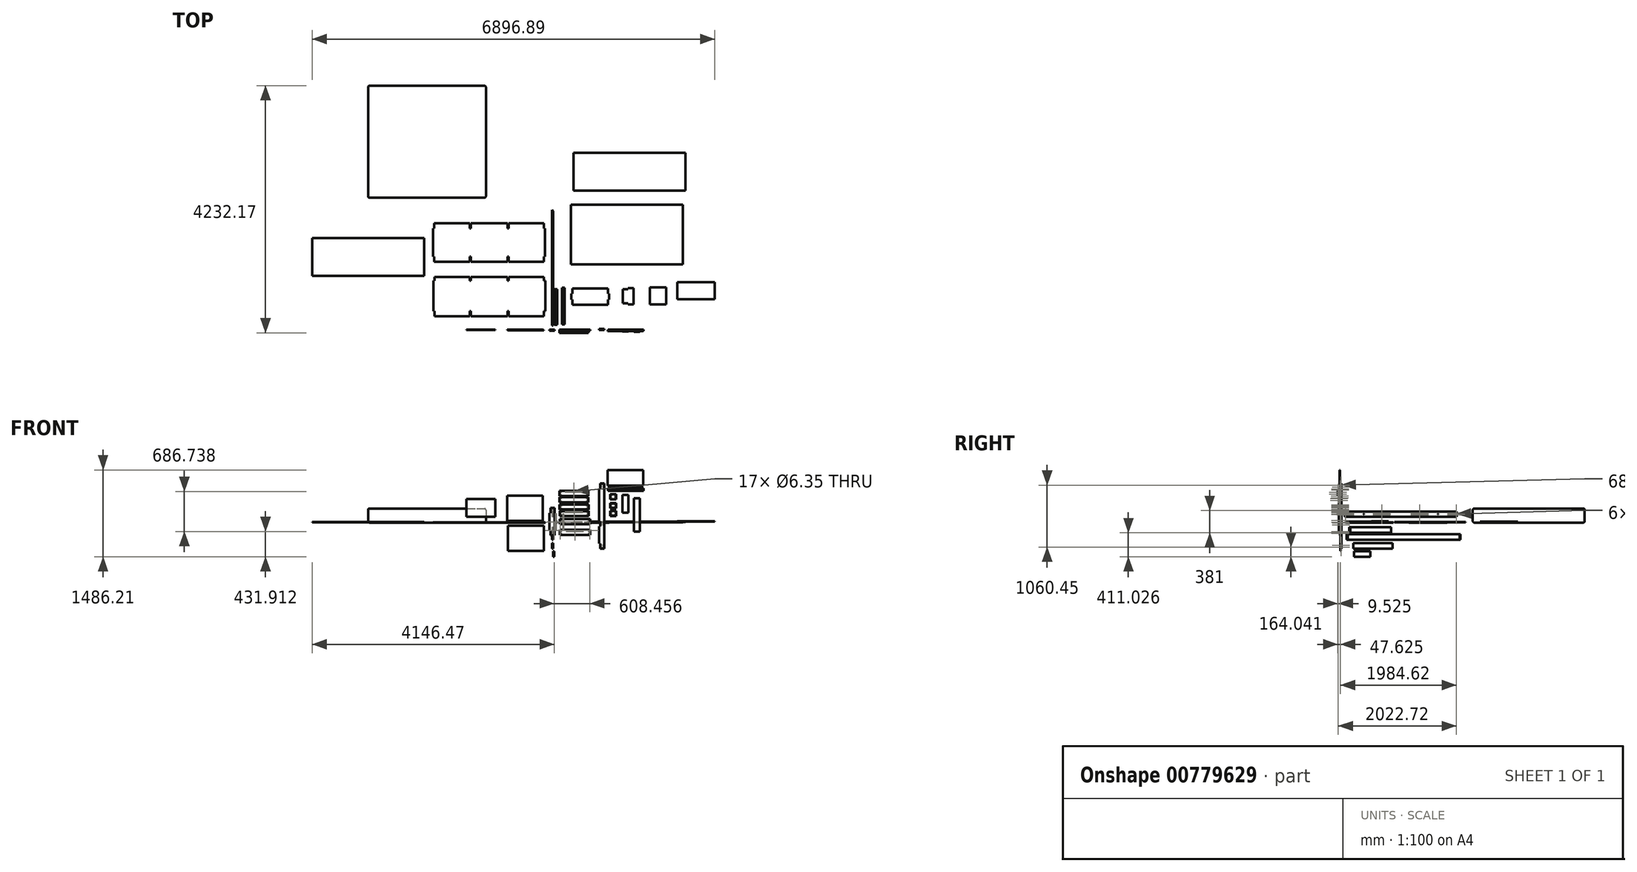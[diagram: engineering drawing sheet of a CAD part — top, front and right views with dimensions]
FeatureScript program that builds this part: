
annotation { "Feature Type Name" : "Feature", "Feature Type Description" : "" }
export const myFeature = defineFeature(function(context is Context, id is Id, definition is map)
    precondition{}
    {
        {
            var Q0;
            Q0=qCreatedBy(makeId("Front.planeOp"),FACE);
            var sketch = newSketch(context, id + "F0", { "sketchPlane" : qUnion([Q0])});
            skLineSegment(sketch, "E0", {"start": v(44.1, 252.24) * mm, "end": v(44.1, -217.66) * mm});
            skLineSegment(sketch, "E1", {"start": v(44.1, -217.66) * mm, "end": v(-25.75, -217.66) * mm});
            skLineSegment(sketch, "E2", {"start": v(-25.75, -217.66) * mm, "end": v(-25.75, -128.76) * mm});
            skLineSegment(sketch, "E3", {"start": v(-25.75, -128.76) * mm, "end": v(-44.8, -128.76) * mm});
            skLineSegment(sketch, "E4", {"start": v(-44.8, -128.76) * mm, "end": v(-44.8, 163.34) * mm});
            skLineSegment(sketch, "E5", {"start": v(-44.8, 163.34) * mm, "end": v(-25.75, 163.34) * mm});
            skLineSegment(sketch, "E6", {"start": v(-25.75, 163.34) * mm, "end": v(-25.75, 252.24) * mm});
            skLineSegment(sketch, "E7", {"start": v(-25.75, 252.24) * mm, "end": v(44.1, 252.24) * mm});
            skPoint(sketch, "E8", {"position": v(36.16, -138.29) * mm});
            skSolve(sketch);
        }
        {
            var Q0;
            Q0=makeQuery(id+"F0.imprint","IMPRINT",FACE,{"disambiguationData":[TD([[makeQuery(id+"F0.imprint","IMPRINT",EDGE,{"derivedFrom":sQuery(id+"F0.wireOp",EDGE,"E0")}),-1.0]])]});
            extrude(context, id + "F1", {"entities" : qUnion([Q0]), "depth" : 19.05 * mm, "offsetDistance" : 25.4 * mm});
        }
        {
            var Q0;
            Q0=sQuery(id+"F0.wireOp",VERTEX,"E8");
            var Q1;
            Q1=makeQuery(id+"F1.opExtrude","SWEPT_BODY",BODY,{"disambiguationData":[OSD([sQuery(id+"F0.wireOp",EDGE,"E0"),sQuery(id+"F0.wireOp",EDGE,"E1"),sQuery(id+"F0.wireOp",EDGE,"E2"),sQuery(id+"F0.wireOp",EDGE,"E3"),sQuery(id+"F0.wireOp",EDGE,"E4"),sQuery(id+"F0.wireOp",EDGE,"E5"),sQuery(id+"F0.wireOp",EDGE,"E6"),sQuery(id+"F0.wireOp",EDGE,"E7")])]});
            hole(context, id + "F2", {"style" : HoleStyle.SIMPLE, "endStyle" : HoleEndStyle.THROUGH, "oppositeDirection" : true, "holeDiameter" : 6.35 * mm, "majorDiameter" : 6.35 * mm, "isTappedThrough" : true, "tappedDepth" : 12.7 * mm, "tapClearance" : 3, "locations" : qUnion([Q0]), "scope" : qUnion([Q1])});
        }
        {
            var Q0;
            Q0=makeQuery(id+"F1.opExtrude","SWEPT_FACE",FACE,{"disambiguationData":[OSD([sQuery(id+"F0.wireOp",EDGE,"E0")])]});
            var sketch = newSketch(context, id + "F3", { "sketchPlane" : qUnion([Q0])});
            skLineSegment(sketch, "E9.0.0", {"start": v(0, -217.66) * mm, "end": v(0, 252.24) * mm});
            skLineSegment(sketch, "E9.0.1", {"start": v(0, 252.24) * mm, "end": v(-19.05, 252.24) * mm});
            skLineSegment(sketch, "E9.0.2", {"start": v(-19.05, 252.24) * mm, "end": v(-19.05, -217.66) * mm});
            skLineSegment(sketch, "E9.0.3", {"start": v(-19.05, -217.66) * mm, "end": v(0, -217.66) * mm});
            skPoint(sketch, "E10", {"position": v(-9.53, -189.09) * mm});
            skPoint(sketch, "E10.positionSnap0", {"position": v(-9.53, -217.66) * mm});
            skPoint(sketch, "E11", {"position": v(-9.53, -157.34) * mm});
            skPoint(sketch, "E12", {"position": v(-9.53, 223.66) * mm});
            skPoint(sketch, "E12.positionSnap0", {"position": v(-9.53, 252.24) * mm});
            skPoint(sketch, "E13", {"position": v(-9.53, 191.91) * mm});
            skSolve(sketch);
        }
        {
            var Q0;
            Q0=sQuery(id+"F3.wireOp",VERTEX,"E10");
            var Q1;
            Q1=makeQuery(id+"F1.opExtrude","SWEPT_BODY",BODY,{"disambiguationData":[OSD([sQuery(id+"F0.wireOp",EDGE,"E0"),sQuery(id+"F0.wireOp",EDGE,"E1"),sQuery(id+"F0.wireOp",EDGE,"E2"),sQuery(id+"F0.wireOp",EDGE,"E3"),sQuery(id+"F0.wireOp",EDGE,"E4"),sQuery(id+"F0.wireOp",EDGE,"E5"),sQuery(id+"F0.wireOp",EDGE,"E6"),sQuery(id+"F0.wireOp",EDGE,"E7")])]});
            hole(context, id + "F4", {"style" : HoleStyle.SIMPLE, "endStyle" : HoleEndStyle.BLIND, "holeDiameter" : 6.35 * mm, "majorDiameter" : 6.35 * mm, "holeDepth" : 25.4 * mm, "isTappedThrough" : true, "tappedDepth" : 12.7 * mm, "tapClearance" : 3, "locations" : qUnion([Q0]), "scope" : qUnion([Q1])});
        }
        {
            var Q0;
            Q0=sQuery(id+"F3.wireOp",VERTEX,"E11");
            var Q1;
            Q1=makeQuery(id+"F1.opExtrude","SWEPT_BODY",BODY,{"disambiguationData":[OSD([sQuery(id+"F0.wireOp",EDGE,"E0"),sQuery(id+"F0.wireOp",EDGE,"E1"),sQuery(id+"F0.wireOp",EDGE,"E2"),sQuery(id+"F0.wireOp",EDGE,"E3"),sQuery(id+"F0.wireOp",EDGE,"E4"),sQuery(id+"F0.wireOp",EDGE,"E5"),sQuery(id+"F0.wireOp",EDGE,"E6"),sQuery(id+"F0.wireOp",EDGE,"E7")])]});
            hole(context, id + "F5", {"style" : HoleStyle.SIMPLE, "endStyle" : HoleEndStyle.BLIND, "holeDiameter" : 6.35 * mm, "majorDiameter" : 6.35 * mm, "holeDepth" : 25.4 * mm, "isTappedThrough" : true, "tappedDepth" : 12.7 * mm, "tapClearance" : 3, "locations" : qUnion([Q0]), "scope" : qUnion([Q1])});
        }
        {
            var Q0;
            Q0=sQuery(id+"F3.wireOp",VERTEX,"E12");
            var Q1;
            Q1=makeQuery(id+"F1.opExtrude","SWEPT_BODY",BODY,{"disambiguationData":[OSD([sQuery(id+"F0.wireOp",EDGE,"E0"),sQuery(id+"F0.wireOp",EDGE,"E1"),sQuery(id+"F0.wireOp",EDGE,"E2"),sQuery(id+"F0.wireOp",EDGE,"E3"),sQuery(id+"F0.wireOp",EDGE,"E4"),sQuery(id+"F0.wireOp",EDGE,"E5"),sQuery(id+"F0.wireOp",EDGE,"E6"),sQuery(id+"F0.wireOp",EDGE,"E7")])]});
            hole(context, id + "F6", {"style" : HoleStyle.SIMPLE, "endStyle" : HoleEndStyle.BLIND, "holeDiameter" : 6.35 * mm, "majorDiameter" : 6.35 * mm, "holeDepth" : 25.4 * mm, "isTappedThrough" : true, "tappedDepth" : 12.7 * mm, "tapClearance" : 3, "locations" : qUnion([Q0]), "scope" : qUnion([Q1])});
        }
        {
            var Q0;
            Q0=sQuery(id+"F3.wireOp",VERTEX,"E13");
            var Q1;
            Q1=makeQuery(id+"F1.opExtrude","SWEPT_BODY",BODY,{"disambiguationData":[OSD([sQuery(id+"F0.wireOp",EDGE,"E0"),sQuery(id+"F0.wireOp",EDGE,"E1"),sQuery(id+"F0.wireOp",EDGE,"E2"),sQuery(id+"F0.wireOp",EDGE,"E3"),sQuery(id+"F0.wireOp",EDGE,"E4"),sQuery(id+"F0.wireOp",EDGE,"E5"),sQuery(id+"F0.wireOp",EDGE,"E6"),sQuery(id+"F0.wireOp",EDGE,"E7")])]});
            hole(context, id + "F7", {"style" : HoleStyle.SIMPLE, "endStyle" : HoleEndStyle.BLIND, "holeDiameter" : 6.35 * mm, "majorDiameter" : 6.35 * mm, "holeDepth" : 25.4 * mm, "isTappedThrough" : true, "tappedDepth" : 12.7 * mm, "tapClearance" : 3, "locations" : qUnion([Q0]), "scope" : qUnion([Q1])});
        }
        {
            var Q0;
            Q0=makeQuery(id+"F1.opExtrude","SWEPT_FACE",FACE,{"disambiguationData":[OSD([sQuery(id+"F0.wireOp",EDGE,"E6")])]});
            var sketch = newSketch(context, id + "F8", { "sketchPlane" : qUnion([Q0])});
            skLineSegment(sketch, "E14.0.0", {"start": v(0, 252.24) * mm, "end": v(0, 163.34) * mm});
            skLineSegment(sketch, "E14.0.1", {"start": v(0, 163.34) * mm, "end": v(19.05, 163.34) * mm});
            skLineSegment(sketch, "E14.0.2", {"start": v(19.05, 163.34) * mm, "end": v(19.05, 252.24) * mm});
            skLineSegment(sketch, "E14.0.3", {"start": v(19.05, 252.24) * mm, "end": v(0, 252.24) * mm});
            skPoint(sketch, "E15", {"position": v(9.53, 223.66) * mm});
            skPoint(sketch, "E15.positionSnap0", {"position": v(9.53, 252.24) * mm});
            skPoint(sketch, "E16", {"position": v(9.53, 191.91) * mm});
            skLineSegment(sketch, "E17.0.0", {"start": v(0, -128.76) * mm, "end": v(0, -217.66) * mm});
            skLineSegment(sketch, "E17.0.1", {"start": v(0, -217.66) * mm, "end": v(19.05, -217.66) * mm});
            skLineSegment(sketch, "E17.0.2", {"start": v(19.05, -217.66) * mm, "end": v(19.05, -128.76) * mm});
            skLineSegment(sketch, "E17.0.3", {"start": v(19.05, -128.76) * mm, "end": v(0, -128.76) * mm});
            skPoint(sketch, "E18", {"position": v(9.52, -189.09) * mm});
            skPoint(sketch, "E18.positionSnap0", {"position": v(9.53, -217.66) * mm});
            skPoint(sketch, "E19", {"position": v(9.52, -157.34) * mm});
            skPoint(sketch, "E20", {"position": v(9.53, 207.79) * mm});
            skPoint(sketch, "E21", {"position": v(9.52, -173.21) * mm});
            skSolve(sketch);
        }
        {
            var Q0;
            Q0=sQuery(id+"F8.wireOp",VERTEX,"E18");
            var Q1;
            Q1=makeQuery(id+"F1.opExtrude","SWEPT_BODY",BODY,{"disambiguationData":[OSD([sQuery(id+"F0.wireOp",EDGE,"E0"),sQuery(id+"F0.wireOp",EDGE,"E1"),sQuery(id+"F0.wireOp",EDGE,"E2"),sQuery(id+"F0.wireOp",EDGE,"E3"),sQuery(id+"F0.wireOp",EDGE,"E4"),sQuery(id+"F0.wireOp",EDGE,"E5"),sQuery(id+"F0.wireOp",EDGE,"E6"),sQuery(id+"F0.wireOp",EDGE,"E7")])]});
            hole(context, id + "F9", {"style" : HoleStyle.SIMPLE, "endStyle" : HoleEndStyle.BLIND, "holeDiameter" : 6.35 * mm, "majorDiameter" : 6.35 * mm, "holeDepth" : 25.4 * mm, "isTappedThrough" : true, "tappedDepth" : 12.7 * mm, "tapClearance" : 3, "locations" : qUnion([Q0]), "scope" : qUnion([Q1])});
        }
        {
            var Q0;
            Q0=sQuery(id+"F8.wireOp",VERTEX,"E19");
            var Q1;
            Q1=makeQuery(id+"F1.opExtrude","SWEPT_BODY",BODY,{"disambiguationData":[OSD([sQuery(id+"F0.wireOp",EDGE,"E0"),sQuery(id+"F0.wireOp",EDGE,"E1"),sQuery(id+"F0.wireOp",EDGE,"E2"),sQuery(id+"F0.wireOp",EDGE,"E3"),sQuery(id+"F0.wireOp",EDGE,"E4"),sQuery(id+"F0.wireOp",EDGE,"E5"),sQuery(id+"F0.wireOp",EDGE,"E6"),sQuery(id+"F0.wireOp",EDGE,"E7")])]});
            hole(context, id + "F10", {"style" : HoleStyle.SIMPLE, "endStyle" : HoleEndStyle.BLIND, "holeDiameter" : 6.35 * mm, "majorDiameter" : 6.35 * mm, "holeDepth" : 25.4 * mm, "isTappedThrough" : true, "tappedDepth" : 12.7 * mm, "tapClearance" : 3, "locations" : qUnion([Q0]), "scope" : qUnion([Q1])});
        }
        {
            var Q0;
            Q0=sQuery(id+"F8.wireOp",VERTEX,"E16");
            var Q1;
            Q1=makeQuery(id+"F1.opExtrude","SWEPT_BODY",BODY,{"disambiguationData":[OSD([sQuery(id+"F0.wireOp",EDGE,"E0"),sQuery(id+"F0.wireOp",EDGE,"E1"),sQuery(id+"F0.wireOp",EDGE,"E2"),sQuery(id+"F0.wireOp",EDGE,"E3"),sQuery(id+"F0.wireOp",EDGE,"E4"),sQuery(id+"F0.wireOp",EDGE,"E5"),sQuery(id+"F0.wireOp",EDGE,"E6"),sQuery(id+"F0.wireOp",EDGE,"E7")])]});
            hole(context, id + "F11", {"style" : HoleStyle.SIMPLE, "endStyle" : HoleEndStyle.BLIND, "holeDiameter" : 6.35 * mm, "majorDiameter" : 6.35 * mm, "holeDepth" : 25.4 * mm, "isTappedThrough" : true, "tappedDepth" : 12.7 * mm, "tapClearance" : 3, "locations" : qUnion([Q0]), "scope" : qUnion([Q1])});
        }
        {
            var Q0;
            Q0=sQuery(id+"F8.wireOp",VERTEX,"E15");
            var Q1;
            Q1=makeQuery(id+"F1.opExtrude","SWEPT_BODY",BODY,{"disambiguationData":[OSD([sQuery(id+"F0.wireOp",EDGE,"E0"),sQuery(id+"F0.wireOp",EDGE,"E1"),sQuery(id+"F0.wireOp",EDGE,"E2"),sQuery(id+"F0.wireOp",EDGE,"E3"),sQuery(id+"F0.wireOp",EDGE,"E4"),sQuery(id+"F0.wireOp",EDGE,"E5"),sQuery(id+"F0.wireOp",EDGE,"E6"),sQuery(id+"F0.wireOp",EDGE,"E7")])]});
            hole(context, id + "F12", {"style" : HoleStyle.SIMPLE, "endStyle" : HoleEndStyle.BLIND, "holeDiameter" : 6.35 * mm, "majorDiameter" : 6.35 * mm, "holeDepth" : 25.4 * mm, "isTappedThrough" : true, "tappedDepth" : 12.7 * mm, "tapClearance" : 3, "locations" : qUnion([Q0]), "scope" : qUnion([Q1])});
        }
        {
            var Q0;
            Q0=sQuery(id+"F8.wireOp",VERTEX,"E21");
            var Q1;
            Q1=makeQuery(id+"F1.opExtrude","SWEPT_BODY",BODY,{"disambiguationData":[OSD([sQuery(id+"F0.wireOp",EDGE,"E0"),sQuery(id+"F0.wireOp",EDGE,"E1"),sQuery(id+"F0.wireOp",EDGE,"E2"),sQuery(id+"F0.wireOp",EDGE,"E3"),sQuery(id+"F0.wireOp",EDGE,"E4"),sQuery(id+"F0.wireOp",EDGE,"E5"),sQuery(id+"F0.wireOp",EDGE,"E6"),sQuery(id+"F0.wireOp",EDGE,"E7")])]});
            hole(context, id + "F13", {"style" : HoleStyle.SIMPLE, "endStyle" : HoleEndStyle.BLIND, "holeDiameter" : 3.3 * mm, "majorDiameter" : 6.35 * mm, "holeDepth" : 25.4 * mm, "isTappedThrough" : true, "tappedDepth" : 12.7 * mm, "tapClearance" : 3, "locations" : qUnion([Q0]), "scope" : qUnion([Q1])});
        }
        {
            var Q0;
            Q0=sQuery(id+"F8.wireOp",VERTEX,"E20");
            var Q1;
            Q1=makeQuery(id+"F1.opExtrude","SWEPT_BODY",BODY,{"disambiguationData":[OSD([sQuery(id+"F0.wireOp",EDGE,"E0"),sQuery(id+"F0.wireOp",EDGE,"E1"),sQuery(id+"F0.wireOp",EDGE,"E2"),sQuery(id+"F0.wireOp",EDGE,"E3"),sQuery(id+"F0.wireOp",EDGE,"E4"),sQuery(id+"F0.wireOp",EDGE,"E5"),sQuery(id+"F0.wireOp",EDGE,"E6"),sQuery(id+"F0.wireOp",EDGE,"E7")])]});
            hole(context, id + "F14", {"style" : HoleStyle.SIMPLE, "endStyle" : HoleEndStyle.BLIND, "holeDiameter" : 3.3 * mm, "majorDiameter" : 6.35 * mm, "holeDepth" : 25.4 * mm, "isTappedThrough" : true, "tappedDepth" : 12.7 * mm, "tapClearance" : 3, "locations" : qUnion([Q0]), "scope" : qUnion([Q1])});
        }
        {
            var Q0;
            Q0=qCreatedBy(makeId("Front.planeOp"),FACE);
            var sketch = newSketch(context, id + "F15", { "sketchPlane" : qUnion([Q0])});
            skLineSegment(sketch, "E22.bottom", {"start": v(131.87, -123.75) * mm, "end": v(652.57, -123.75) * mm});
            skLineSegment(sketch, "E22.top", {"start": v(131.87, -212.65) * mm, "end": v(652.57, -212.65) * mm});
            skLineSegment(sketch, "E22.left", {"start": v(131.87, -123.75) * mm, "end": v(131.87, -212.65) * mm});
            skLineSegment(sketch, "E22.right", {"start": v(652.57, -123.75) * mm, "end": v(652.57, -212.65) * mm});
            skPoint(sketch, "E23", {"position": v(139.82, -133.28) * mm});
            skPoint(sketch, "E24", {"position": v(644.62, -133.28) * mm});
            skPoint(sketch, "E25", {"position": v(392.22, -136.45) * mm});
            skPoint(sketch, "E25.positionSnap0", {"position": v(392.22, -123.75) * mm});
            skPoint(sketch, "E26", {"position": v(392.22, -152.33) * mm});
            skSolve(sketch);
        }
        {
            var Q0;
            Q0=makeQuery(id+"F15.imprint","IMPRINT",FACE,{"disambiguationData":[TD([[makeQuery(id+"F15.imprint","IMPRINT",EDGE,{"derivedFrom":sQuery(id+"F15.wireOp",EDGE,"E22.bottom")}),-1.0]])]});
            extrude(context, id + "F16", {"entities" : qUnion([Q0]), "depth" : 19.05 * mm, "offsetDistance" : 25.4 * mm});
        }
        {
            var Q0;
            Q0=sQuery(id+"F15.wireOp",VERTEX,"E23");
            var Q1;
            Q1=makeQuery(id+"F16.opExtrude","SWEPT_BODY",BODY,{"disambiguationData":[OSD([sQuery(id+"F15.wireOp",EDGE,"E22.bottom"),sQuery(id+"F15.wireOp",EDGE,"E22.top"),sQuery(id+"F15.wireOp",EDGE,"E22.left"),sQuery(id+"F15.wireOp",EDGE,"E22.right")])]});
            hole(context, id + "F17", {"style" : HoleStyle.SIMPLE, "endStyle" : HoleEndStyle.THROUGH, "oppositeDirection" : true, "holeDiameter" : 6.35 * mm, "majorDiameter" : 6.35 * mm, "isTappedThrough" : true, "tappedDepth" : 12.7 * mm, "tapClearance" : 3, "locations" : qUnion([Q0]), "scope" : qUnion([Q1])});
        }
        {
            var Q0;
            Q0=sQuery(id+"F15.wireOp",VERTEX,"E24");
            var Q1;
            Q1=makeQuery(id+"F16.opExtrude","SWEPT_BODY",BODY,{"disambiguationData":[OSD([sQuery(id+"F15.wireOp",EDGE,"E22.bottom"),sQuery(id+"F15.wireOp",EDGE,"E22.top"),sQuery(id+"F15.wireOp",EDGE,"E22.left"),sQuery(id+"F15.wireOp",EDGE,"E22.right")])]});
            hole(context, id + "F18", {"style" : HoleStyle.SIMPLE, "endStyle" : HoleEndStyle.THROUGH, "oppositeDirection" : true, "holeDiameter" : 6.35 * mm, "majorDiameter" : 6.35 * mm, "isTappedThrough" : true, "tappedDepth" : 12.7 * mm, "tapClearance" : 3, "locations" : qUnion([Q0]), "scope" : qUnion([Q1])});
        }
        {
            var Q0;
            Q0=makeQuery(id+"F16.opExtrude","SWEPT_FACE",FACE,{"disambiguationData":[OSD([sQuery(id+"F15.wireOp",EDGE,"E22.right")])]});
            var sketch = newSketch(context, id + "F19", { "sketchPlane" : qUnion([Q0])});
            skLineSegment(sketch, "E27.0.0", {"start": v(0, -212.65) * mm, "end": v(0, -123.75) * mm});
            skLineSegment(sketch, "E27.0.1", {"start": v(0, -123.75) * mm, "end": v(-19.05, -123.75) * mm});
            skLineSegment(sketch, "E27.0.2", {"start": v(-19.05, -123.75) * mm, "end": v(-19.05, -212.65) * mm});
            skLineSegment(sketch, "E27.0.3", {"start": v(-19.05, -212.65) * mm, "end": v(0, -212.65) * mm});
            skPoint(sketch, "E28", {"position": v(-9.53, -152.33) * mm});
            skPoint(sketch, "E28.positionSnap0", {"position": v(-9.53, -123.75) * mm});
            skPoint(sketch, "E29", {"position": v(-9.53, -184.08) * mm});
            skSolve(sketch);
        }
        {
            var Q0;
            Q0=sQuery(id+"F19.wireOp",VERTEX,"E28");
            var Q1;
            Q1=makeQuery(id+"F16.opExtrude","SWEPT_BODY",BODY,{"disambiguationData":[OSD([sQuery(id+"F15.wireOp",EDGE,"E22.bottom"),sQuery(id+"F15.wireOp",EDGE,"E22.top"),sQuery(id+"F15.wireOp",EDGE,"E22.left"),sQuery(id+"F15.wireOp",EDGE,"E22.right")])]});
            hole(context, id + "F20", {"style" : HoleStyle.SIMPLE, "endStyle" : HoleEndStyle.BLIND, "holeDiameter" : 6.35 * mm, "majorDiameter" : 6.35 * mm, "holeDepth" : 25.4 * mm, "isTappedThrough" : true, "tappedDepth" : 12.7 * mm, "tapClearance" : 3, "locations" : qUnion([Q0]), "scope" : qUnion([Q1])});
        }
        {
            var Q0;
            Q0=sQuery(id+"F19.wireOp",VERTEX,"E29");
            var Q1;
            Q1=makeQuery(id+"F16.opExtrude","SWEPT_BODY",BODY,{"disambiguationData":[OSD([sQuery(id+"F15.wireOp",EDGE,"E22.bottom"),sQuery(id+"F15.wireOp",EDGE,"E22.top"),sQuery(id+"F15.wireOp",EDGE,"E22.left"),sQuery(id+"F15.wireOp",EDGE,"E22.right")])]});
            hole(context, id + "F21", {"style" : HoleStyle.SIMPLE, "endStyle" : HoleEndStyle.BLIND, "holeDiameter" : 6.35 * mm, "majorDiameter" : 6.35 * mm, "holeDepth" : 25.4 * mm, "isTappedThrough" : true, "tappedDepth" : 12.7 * mm, "tapClearance" : 3, "locations" : qUnion([Q0]), "scope" : qUnion([Q1])});
        }
        {
            var Q0;
            Q0=makeQuery(id+"F16.opExtrude","SWEPT_FACE",FACE,{"disambiguationData":[OSD([sQuery(id+"F15.wireOp",EDGE,"E22.left")])]});
            var sketch = newSketch(context, id + "F22", { "sketchPlane" : qUnion([Q0])});
            skLineSegment(sketch, "E30.0.0", {"start": v(0, -123.75) * mm, "end": v(0, -212.65) * mm});
            skLineSegment(sketch, "E30.0.1", {"start": v(0, -212.65) * mm, "end": v(19.05, -212.65) * mm});
            skLineSegment(sketch, "E30.0.2", {"start": v(19.05, -212.65) * mm, "end": v(19.05, -123.75) * mm});
            skLineSegment(sketch, "E30.0.3", {"start": v(19.05, -123.75) * mm, "end": v(0, -123.75) * mm});
            skPoint(sketch, "E31", {"position": v(9.53, -152.33) * mm});
            skPoint(sketch, "E31.positionSnap0", {"position": v(9.53, -123.75) * mm});
            skPoint(sketch, "E32", {"position": v(9.53, -184.08) * mm});
            skSolve(sketch);
        }
        {
            var Q0;
            Q0=sQuery(id+"F22.wireOp",VERTEX,"E31");
            var Q1;
            Q1=makeQuery(id+"F16.opExtrude","SWEPT_BODY",BODY,{"disambiguationData":[OSD([sQuery(id+"F15.wireOp",EDGE,"E22.bottom"),sQuery(id+"F15.wireOp",EDGE,"E22.top"),sQuery(id+"F15.wireOp",EDGE,"E22.left"),sQuery(id+"F15.wireOp",EDGE,"E22.right")])]});
            hole(context, id + "F23", {"style" : HoleStyle.SIMPLE, "endStyle" : HoleEndStyle.BLIND, "holeDiameter" : 6.35 * mm, "majorDiameter" : 6.35 * mm, "holeDepth" : 25.4 * mm, "isTappedThrough" : true, "tappedDepth" : 12.7 * mm, "tapClearance" : 3, "locations" : qUnion([Q0]), "scope" : qUnion([Q1])});
        }
        {
            var Q0;
            Q0=sQuery(id+"F22.wireOp",VERTEX,"E32");
            var Q1;
            Q1=makeQuery(id+"F16.opExtrude","SWEPT_BODY",BODY,{"disambiguationData":[OSD([sQuery(id+"F15.wireOp",EDGE,"E22.bottom"),sQuery(id+"F15.wireOp",EDGE,"E22.top"),sQuery(id+"F15.wireOp",EDGE,"E22.left"),sQuery(id+"F15.wireOp",EDGE,"E22.right")])]});
            hole(context, id + "F24", {"style" : HoleStyle.SIMPLE, "endStyle" : HoleEndStyle.BLIND, "holeDiameter" : 6.35 * mm, "majorDiameter" : 6.35 * mm, "holeDepth" : 25.4 * mm, "isTappedThrough" : true, "tappedDepth" : 12.7 * mm, "tapClearance" : 3, "locations" : qUnion([Q0]), "scope" : qUnion([Q1])});
        }
        {
            var Q0;
            Q0=sQuery(id+"F15.wireOp",VERTEX,"E25");
            var Q1;
            Q1=makeQuery(id+"F16.opExtrude","SWEPT_BODY",BODY,{"disambiguationData":[OSD([sQuery(id+"F15.wireOp",EDGE,"E22.bottom"),sQuery(id+"F15.wireOp",EDGE,"E22.top"),sQuery(id+"F15.wireOp",EDGE,"E22.left"),sQuery(id+"F15.wireOp",EDGE,"E22.right")])]});
            hole(context, id + "F25", {"style" : HoleStyle.SIMPLE, "endStyle" : HoleEndStyle.THROUGH, "oppositeDirection" : true, "holeDiameter" : 6.35 * mm, "majorDiameter" : 6.35 * mm, "isTappedThrough" : true, "tappedDepth" : 12.7 * mm, "tapClearance" : 3, "locations" : qUnion([Q0]), "scope" : qUnion([Q1])});
        }
        {
            var Q0;
            Q0=sQuery(id+"F15.wireOp",VERTEX,"E26");
            var Q1;
            Q1=makeQuery(id+"F16.opExtrude","SWEPT_BODY",BODY,{"disambiguationData":[OSD([sQuery(id+"F15.wireOp",EDGE,"E22.bottom"),sQuery(id+"F15.wireOp",EDGE,"E22.top"),sQuery(id+"F15.wireOp",EDGE,"E22.left"),sQuery(id+"F15.wireOp",EDGE,"E22.right")])]});
            hole(context, id + "F26", {"style" : HoleStyle.SIMPLE, "endStyle" : HoleEndStyle.THROUGH, "oppositeDirection" : true, "holeDiameter" : 6.35 * mm, "majorDiameter" : 6.35 * mm, "isTappedThrough" : true, "tappedDepth" : 12.7 * mm, "tapClearance" : 3, "locations" : qUnion([Q0]), "scope" : qUnion([Q1])});
        }
        {
            var Q0;
            Q0=qCreatedBy(makeId("Front.planeOp"),FACE);
            var sketch = newSketch(context, id + "F27", { "sketchPlane" : qUnion([Q0])});
            skLineSegment(sketch, "E33.bottom", {"start": v(129.69, 61.82) * mm, "end": v(650.39, 61.82) * mm});
            skLineSegment(sketch, "E33.top", {"start": v(129.69, -27.08) * mm, "end": v(650.39, -27.08) * mm});
            skLineSegment(sketch, "E33.left", {"start": v(129.69, 61.82) * mm, "end": v(129.69, -27.08) * mm});
            skLineSegment(sketch, "E33.right", {"start": v(650.39, 61.82) * mm, "end": v(650.39, -27.08) * mm});
            skSolve(sketch);
        }
        {
            var Q0;
            Q0=makeQuery(id+"F27.imprint","IMPRINT",FACE,{"disambiguationData":[TD([[makeQuery(id+"F27.imprint","IMPRINT",EDGE,{"derivedFrom":sQuery(id+"F27.wireOp",EDGE,"E33.bottom")}),-1.0]])]});
            extrude(context, id + "F28", {"entities" : qUnion([Q0]), "depth" : 19.05 * mm, "offsetDistance" : 25.4 * mm});
        }
        {
            var Q0;
            Q0=makeQuery(id+"F28.opExtrude","SWEPT_FACE",FACE,{"disambiguationData":[OSD([sQuery(id+"F27.wireOp",EDGE,"E33.right")])]});
            var sketch = newSketch(context, id + "F29", { "sketchPlane" : qUnion([Q0])});
            skLineSegment(sketch, "E34.0.0", {"start": v(0, -27.08) * mm, "end": v(0, 61.82) * mm});
            skLineSegment(sketch, "E34.0.1", {"start": v(0, 61.82) * mm, "end": v(-19.05, 61.82) * mm});
            skLineSegment(sketch, "E34.0.2", {"start": v(-19.05, 61.82) * mm, "end": v(-19.05, -27.08) * mm});
            skLineSegment(sketch, "E34.0.3", {"start": v(-19.05, -27.08) * mm, "end": v(0, -27.08) * mm});
            skPoint(sketch, "E35", {"position": v(-9.53, 33.24) * mm});
            skPoint(sketch, "E35.positionSnap0", {"position": v(-9.53, 61.82) * mm});
            skPoint(sketch, "E36", {"position": v(-9.53, 1.5) * mm});
            skSolve(sketch);
        }
        {
            var Q0;
            Q0=sQuery(id+"F29.wireOp",VERTEX,"E35");
            var Q1;
            Q1=makeQuery(id+"F28.opExtrude","SWEPT_BODY",BODY,{"disambiguationData":[OSD([sQuery(id+"F27.wireOp",EDGE,"E33.bottom"),sQuery(id+"F27.wireOp",EDGE,"E33.top"),sQuery(id+"F27.wireOp",EDGE,"E33.left"),sQuery(id+"F27.wireOp",EDGE,"E33.right")])]});
            hole(context, id + "F30", {"style" : HoleStyle.SIMPLE, "endStyle" : HoleEndStyle.BLIND, "holeDiameter" : 6.35 * mm, "majorDiameter" : 6.35 * mm, "holeDepth" : 25.4 * mm, "isTappedThrough" : true, "tappedDepth" : 12.7 * mm, "tapClearance" : 3, "locations" : qUnion([Q0]), "scope" : qUnion([Q1])});
        }
        {
            var Q0;
            Q0=sQuery(id+"F29.wireOp",VERTEX,"E36");
            var Q1;
            Q1=makeQuery(id+"F28.opExtrude","SWEPT_BODY",BODY,{"disambiguationData":[OSD([sQuery(id+"F27.wireOp",EDGE,"E33.bottom"),sQuery(id+"F27.wireOp",EDGE,"E33.top"),sQuery(id+"F27.wireOp",EDGE,"E33.left"),sQuery(id+"F27.wireOp",EDGE,"E33.right")])]});
            hole(context, id + "F31", {"style" : HoleStyle.SIMPLE, "endStyle" : HoleEndStyle.BLIND, "holeDiameter" : 6.35 * mm, "majorDiameter" : 6.35 * mm, "holeDepth" : 25.4 * mm, "isTappedThrough" : true, "tappedDepth" : 12.7 * mm, "tapClearance" : 3, "locations" : qUnion([Q0]), "scope" : qUnion([Q1])});
        }
        {
            var Q0;
            Q0=makeQuery(id+"F28.opExtrude","SWEPT_FACE",FACE,{"disambiguationData":[OSD([sQuery(id+"F27.wireOp",EDGE,"E33.left")])]});
            var sketch = newSketch(context, id + "F32", { "sketchPlane" : qUnion([Q0])});
            skPoint(sketch, "E37", {"position": v(9.53, 33.24) * mm});
            skPoint(sketch, "E37.positionSnap0", {"position": v(9.53, 61.82) * mm});
            skPoint(sketch, "E38", {"position": v(9.53, 1.5) * mm});
            skSolve(sketch);
        }
        {
            var Q0;
            Q0=sQuery(id+"F32.wireOp",VERTEX,"E37");
            var Q1;
            Q1=makeQuery(id+"F28.opExtrude","SWEPT_BODY",BODY,{"disambiguationData":[OSD([sQuery(id+"F27.wireOp",EDGE,"E33.bottom"),sQuery(id+"F27.wireOp",EDGE,"E33.top"),sQuery(id+"F27.wireOp",EDGE,"E33.left"),sQuery(id+"F27.wireOp",EDGE,"E33.right")])]});
            hole(context, id + "F33", {"style" : HoleStyle.SIMPLE, "endStyle" : HoleEndStyle.BLIND, "holeDiameter" : 6.35 * mm, "majorDiameter" : 6.35 * mm, "holeDepth" : 25.4 * mm, "isTappedThrough" : true, "tappedDepth" : 12.7 * mm, "tapClearance" : 3, "locations" : qUnion([Q0]), "scope" : qUnion([Q1])});
        }
        {
            var Q0;
            Q0=sQuery(id+"F32.wireOp",VERTEX,"E38");
            var Q1;
            Q1=makeQuery(id+"F28.opExtrude","SWEPT_BODY",BODY,{"disambiguationData":[OSD([sQuery(id+"F27.wireOp",EDGE,"E33.bottom"),sQuery(id+"F27.wireOp",EDGE,"E33.top"),sQuery(id+"F27.wireOp",EDGE,"E33.left"),sQuery(id+"F27.wireOp",EDGE,"E33.right")])]});
            hole(context, id + "F34", {"style" : HoleStyle.SIMPLE, "endStyle" : HoleEndStyle.BLIND, "holeDiameter" : 6.35 * mm, "majorDiameter" : 6.35 * mm, "holeDepth" : 25.4 * mm, "isTappedThrough" : true, "tappedDepth" : 12.7 * mm, "tapClearance" : 3, "locations" : qUnion([Q0]), "scope" : qUnion([Q1])});
        }
        {
            var Q0;
            Q0=qCreatedBy(makeId("Top.planeOp"),FACE);
            var sketch = newSketch(context, id + "F35", { "sketchPlane" : qUnion([Q0])});
            skLineSegment(sketch, "E39.bottom", {"start": v(44.59, 80.67) * mm, "end": v(85.86, 80.67) * mm});
            skLineSegment(sketch, "E39.top", {"start": v(44.59, 687.1) * mm, "end": v(85.86, 687.1) * mm});
            skLineSegment(sketch, "E39.left", {"start": v(44.59, 80.67) * mm, "end": v(44.59, 687.1) * mm});
            skLineSegment(sketch, "E39.right", {"start": v(85.86, 80.67) * mm, "end": v(85.86, 687.1) * mm});
            skSolve(sketch);
        }
        {
            var Q0;
            Q0=makeQuery(id+"F35.imprint","IMPRINT",FACE,{"disambiguationData":[TD([[makeQuery(id+"F35.imprint","IMPRINT",EDGE,{"derivedFrom":sQuery(id+"F35.wireOp",EDGE,"E39.bottom")}),1.0]])]});
            var sketch = newSketch(context, id + "F36", { "sketchPlane" : qUnion([Q0])});
            skLineSegment(sketch, "E40.bottom", {"start": v(170.58, 712.28) * mm, "end": v(211.85, 712.28) * mm});
            skLineSegment(sketch, "E40.top", {"start": v(170.58, 83.63) * mm, "end": v(211.85, 83.63) * mm});
            skLineSegment(sketch, "E40.left", {"start": v(170.58, 712.28) * mm, "end": v(170.58, 83.63) * mm});
            skLineSegment(sketch, "E40.right", {"start": v(211.85, 712.28) * mm, "end": v(211.85, 83.63) * mm});
            skSolve(sketch);
        }
        {
            var Q0;
            Q0=makeQuery(id+"F36.imprint","IMPRINT",FACE,{"disambiguationData":[TD([[makeQuery(id+"F36.imprint","IMPRINT",EDGE,{"derivedFrom":makeQuery(id+"F35.imprint","IMPRINT",EDGE,{"derivedFrom":sQuery(id+"F35.wireOp",EDGE,"E39.bottom")})}),1.0]])]});
            extrude(context, id + "F37", {"entities" : qUnion([Q0]), "depth" : 19.05 * mm, "offsetDistance" : 25.4 * mm});
        }
        {
            var Q0;
            Q0=makeQuery(id+"F36.imprint","IMPRINT",FACE,{"disambiguationData":[TD([[makeQuery(id+"F36.imprint","IMPRINT",EDGE,{"derivedFrom":sQuery(id+"F36.wireOp",EDGE,"E40.bottom")}),-1.0]])]});
            extrude(context, id + "F38", {"entities" : qUnion([Q0]), "depth" : 19.05 * mm, "offsetDistance" : 25.4 * mm});
        }
        {
            var Q0;
            Q0=makeQuery(id+"F38.opExtrude","SWEPT_FACE",FACE,{"disambiguationData":[OSD([sQuery(id+"F36.wireOp",EDGE,"E40.top")])]});
            var sketch = newSketch(context, id + "F39", { "sketchPlane" : qUnion([Q0])});
            skLineSegment(sketch, "E41.0.0", {"start": v(170.58, 0) * mm, "end": v(211.85, 0) * mm});
            skLineSegment(sketch, "E41.0.1", {"start": v(211.85, 0) * mm, "end": v(211.85, 19.05) * mm});
            skLineSegment(sketch, "E41.0.2", {"start": v(211.85, 19.05) * mm, "end": v(170.58, 19.05) * mm});
            skLineSegment(sketch, "E41.0.3", {"start": v(170.58, 19.05) * mm, "end": v(170.58, 0) * mm});
            skPoint(sketch, "E42", {"position": v(183.28, 9.53) * mm});
            skPoint(sketch, "E42.positionSnap0", {"position": v(170.58, 9.53) * mm});
            skPoint(sketch, "E43", {"position": v(199.15, 9.53) * mm});
            skPoint(sketch, "E43.positionSnap0", {"position": v(211.85, 9.53) * mm});
            skSolve(sketch);
        }
        {
            var Q0;
            Q0=sQuery(id+"F39.wireOp",VERTEX,"E42");
            var Q1;
            Q1=makeQuery(id+"F38.opExtrude","SWEPT_BODY",BODY,{"disambiguationData":[OSD([sQuery(id+"F36.wireOp",EDGE,"E40.bottom"),sQuery(id+"F36.wireOp",EDGE,"E40.top"),sQuery(id+"F36.wireOp",EDGE,"E40.left"),sQuery(id+"F36.wireOp",EDGE,"E40.right")])]});
            hole(context, id + "F40", {"style" : HoleStyle.SIMPLE, "endStyle" : HoleEndStyle.BLIND, "holeDiameter" : 6.35 * mm, "majorDiameter" : 6.35 * mm, "holeDepth" : 25.4 * mm, "isTappedThrough" : true, "tappedDepth" : 12.7 * mm, "tapClearance" : 3, "locations" : qUnion([Q0]), "scope" : qUnion([Q1])});
        }
        {
            var Q0;
            Q0=sQuery(id+"F39.wireOp",VERTEX,"E43");
            var Q1;
            Q1=makeQuery(id+"F38.opExtrude","SWEPT_BODY",BODY,{"disambiguationData":[OSD([sQuery(id+"F36.wireOp",EDGE,"E40.bottom"),sQuery(id+"F36.wireOp",EDGE,"E40.top"),sQuery(id+"F36.wireOp",EDGE,"E40.left"),sQuery(id+"F36.wireOp",EDGE,"E40.right")])]});
            hole(context, id + "F41", {"style" : HoleStyle.SIMPLE, "endStyle" : HoleEndStyle.BLIND, "holeDiameter" : 6.35 * mm, "majorDiameter" : 6.35 * mm, "holeDepth" : 25.4 * mm, "isTappedThrough" : true, "tappedDepth" : 12.7 * mm, "tapClearance" : 3, "locations" : qUnion([Q0]), "scope" : qUnion([Q1])});
        }
        {
            var Q0;
            Q0=makeQuery(id+"F37.opExtrude","SWEPT_FACE",FACE,{"disambiguationData":[OSD([sQuery(id+"F35.wireOp",EDGE,"E39.bottom")])]});
            var sketch = newSketch(context, id + "F42", { "sketchPlane" : qUnion([Q0])});
            skLineSegment(sketch, "E44.0.0", {"start": v(44.59, 0) * mm, "end": v(85.86, 0) * mm});
            skLineSegment(sketch, "E44.0.1", {"start": v(85.86, 0) * mm, "end": v(85.86, 19.05) * mm});
            skLineSegment(sketch, "E44.0.2", {"start": v(85.86, 19.05) * mm, "end": v(44.59, 19.05) * mm});
            skLineSegment(sketch, "E44.0.3", {"start": v(44.59, 19.05) * mm, "end": v(44.59, 0) * mm});
            skPoint(sketch, "E45", {"position": v(57.29, 9.53) * mm});
            skPoint(sketch, "E45.positionSnap0", {"position": v(44.59, 9.53) * mm});
            skPoint(sketch, "E46", {"position": v(73.16, 9.53) * mm});
            skPoint(sketch, "E46.positionSnap0", {"position": v(85.86, 9.53) * mm});
            skSolve(sketch);
        }
        {
            var Q0;
            Q0=sQuery(id+"F42.wireOp",VERTEX,"E46");
            var Q1;
            Q1=makeQuery(id+"F37.opExtrude","SWEPT_BODY",BODY,{"disambiguationData":[OSD([sQuery(id+"F35.wireOp",EDGE,"E39.bottom"),sQuery(id+"F35.wireOp",EDGE,"E39.top"),sQuery(id+"F35.wireOp",EDGE,"E39.left"),sQuery(id+"F35.wireOp",EDGE,"E39.right")])]});
            hole(context, id + "F43", {"style" : HoleStyle.SIMPLE, "endStyle" : HoleEndStyle.BLIND, "holeDiameter" : 6.35 * mm, "majorDiameter" : 6.35 * mm, "holeDepth" : 25.4 * mm, "isTappedThrough" : true, "tappedDepth" : 12.7 * mm, "tapClearance" : 3, "locations" : qUnion([Q0]), "scope" : qUnion([Q1])});
        }
        {
            var Q0;
            Q0=sQuery(id+"F42.wireOp",VERTEX,"E45");
            var Q1;
            Q1=makeQuery(id+"F37.opExtrude","SWEPT_BODY",BODY,{"disambiguationData":[OSD([sQuery(id+"F35.wireOp",EDGE,"E39.bottom"),sQuery(id+"F35.wireOp",EDGE,"E39.top"),sQuery(id+"F35.wireOp",EDGE,"E39.left"),sQuery(id+"F35.wireOp",EDGE,"E39.right")])]});
            hole(context, id + "F44", {"style" : HoleStyle.SIMPLE, "endStyle" : HoleEndStyle.BLIND, "holeDiameter" : 6.35 * mm, "majorDiameter" : 6.35 * mm, "holeDepth" : 25.4 * mm, "isTappedThrough" : true, "tappedDepth" : 12.7 * mm, "tapClearance" : 3, "locations" : qUnion([Q0]), "scope" : qUnion([Q1])});
        }
        {
            var Q0;
            Q0=makeQuery(id+"F37.opExtrude","SWEPT_FACE",FACE,{"disambiguationData":[OSD([sQuery(id+"F35.wireOp",EDGE,"E39.top")])]});
            var sketch = newSketch(context, id + "F45", { "sketchPlane" : qUnion([Q0])});
            skLineSegment(sketch, "E47.0.0", {"start": v(-85.86, 0) * mm, "end": v(-44.59, 0) * mm});
            skLineSegment(sketch, "E47.0.1", {"start": v(-44.59, 0) * mm, "end": v(-44.59, 19.05) * mm});
            skLineSegment(sketch, "E47.0.2", {"start": v(-44.59, 19.05) * mm, "end": v(-85.86, 19.05) * mm});
            skLineSegment(sketch, "E47.0.3", {"start": v(-85.86, 19.05) * mm, "end": v(-85.86, 0) * mm});
            skPoint(sketch, "E48", {"position": v(-73.16, 9.53) * mm});
            skPoint(sketch, "E48.positionSnap0", {"position": v(-85.86, 9.53) * mm});
            skPoint(sketch, "E49", {"position": v(-57.29, 9.53) * mm});
            skPoint(sketch, "E49.positionSnap0", {"position": v(-44.59, 9.53) * mm});
            skSolve(sketch);
        }
        {
            var Q0;
            Q0=sQuery(id+"F45.wireOp",VERTEX,"E48");
            var Q1;
            Q1=makeQuery(id+"F37.opExtrude","SWEPT_BODY",BODY,{"disambiguationData":[OSD([sQuery(id+"F35.wireOp",EDGE,"E39.bottom"),sQuery(id+"F35.wireOp",EDGE,"E39.top"),sQuery(id+"F35.wireOp",EDGE,"E39.left"),sQuery(id+"F35.wireOp",EDGE,"E39.right")])]});
            hole(context, id + "F46", {"style" : HoleStyle.SIMPLE, "endStyle" : HoleEndStyle.BLIND, "holeDiameter" : 6.35 * mm, "majorDiameter" : 6.35 * mm, "holeDepth" : 25.4 * mm, "isTappedThrough" : true, "tappedDepth" : 12.7 * mm, "tapClearance" : 3, "locations" : qUnion([Q0]), "scope" : qUnion([Q1])});
        }
        {
            var Q0;
            Q0=sQuery(id+"F45.wireOp",VERTEX,"E49");
            var Q1;
            Q1=makeQuery(id+"F37.opExtrude","SWEPT_BODY",BODY,{"disambiguationData":[OSD([sQuery(id+"F35.wireOp",EDGE,"E39.bottom"),sQuery(id+"F35.wireOp",EDGE,"E39.top"),sQuery(id+"F35.wireOp",EDGE,"E39.left"),sQuery(id+"F35.wireOp",EDGE,"E39.right")])]});
            hole(context, id + "F47", {"style" : HoleStyle.SIMPLE, "endStyle" : HoleEndStyle.BLIND, "holeDiameter" : 6.35 * mm, "majorDiameter" : 6.35 * mm, "holeDepth" : 25.4 * mm, "isTappedThrough" : true, "tappedDepth" : 12.7 * mm, "tapClearance" : 3, "locations" : qUnion([Q0]), "scope" : qUnion([Q1])});
        }
        {
            var Q0;
            Q0=makeQuery(id+"F38.opExtrude","SWEPT_FACE",FACE,{"disambiguationData":[OSD([sQuery(id+"F36.wireOp",EDGE,"E40.bottom")])]});
            var sketch = newSketch(context, id + "F48", { "sketchPlane" : qUnion([Q0])});
            skLineSegment(sketch, "E50.0.0", {"start": v(-211.85, 0) * mm, "end": v(-170.58, 0) * mm});
            skLineSegment(sketch, "E50.0.1", {"start": v(-170.58, 0) * mm, "end": v(-170.58, 19.05) * mm});
            skLineSegment(sketch, "E50.0.2", {"start": v(-170.58, 19.05) * mm, "end": v(-211.85, 19.05) * mm});
            skLineSegment(sketch, "E50.0.3", {"start": v(-211.85, 19.05) * mm, "end": v(-211.85, 0) * mm});
            skPoint(sketch, "E51", {"position": v(-199.15, 9.53) * mm});
            skPoint(sketch, "E51.positionSnap0", {"position": v(-211.85, 9.53) * mm});
            skPoint(sketch, "E52", {"position": v(-170.58, 9.53) * mm});
            skPoint(sketch, "E53", {"position": v(-183.28, 10) * mm});
            skSolve(sketch);
        }
        {
            var Q0;
            Q0=sQuery(id+"F48.wireOp",VERTEX,"E53");
            var Q1;
            Q1=makeQuery(id+"F38.opExtrude","SWEPT_BODY",BODY,{"disambiguationData":[OSD([sQuery(id+"F36.wireOp",EDGE,"E40.bottom"),sQuery(id+"F36.wireOp",EDGE,"E40.top"),sQuery(id+"F36.wireOp",EDGE,"E40.left"),sQuery(id+"F36.wireOp",EDGE,"E40.right")])]});
            hole(context, id + "F49", {"style" : HoleStyle.SIMPLE, "endStyle" : HoleEndStyle.BLIND, "holeDiameter" : 6.35 * mm, "majorDiameter" : 6.35 * mm, "holeDepth" : 25.4 * mm, "isTappedThrough" : true, "tappedDepth" : 12.7 * mm, "tapClearance" : 3, "locations" : qUnion([Q0]), "scope" : qUnion([Q1])});
        }
        {
            var Q0;
            Q0=sQuery(id+"F48.wireOp",VERTEX,"E51");
            var Q1;
            Q1=makeQuery(id+"F38.opExtrude","SWEPT_BODY",BODY,{"disambiguationData":[OSD([sQuery(id+"F36.wireOp",EDGE,"E40.bottom"),sQuery(id+"F36.wireOp",EDGE,"E40.top"),sQuery(id+"F36.wireOp",EDGE,"E40.left"),sQuery(id+"F36.wireOp",EDGE,"E40.right")])]});
            hole(context, id + "F50", {"style" : HoleStyle.SIMPLE, "endStyle" : HoleEndStyle.BLIND, "holeDiameter" : 6.35 * mm, "majorDiameter" : 6.35 * mm, "holeDepth" : 25.4 * mm, "isTappedThrough" : true, "tappedDepth" : 12.7 * mm, "tapClearance" : 3, "locations" : qUnion([Q0]), "scope" : qUnion([Q1])});
        }
        {
            var Q0;
            Q0=qCreatedBy(makeId("Right.planeOp"),FACE);
            var sketch = newSketch(context, id + "F51", { "sketchPlane" : qUnion([Q0])});
            skLineSegment(sketch, "E54.bottom", {"start": v(66.92, 191.14) * mm, "end": v(1984.62, 191.14) * mm});
            skLineSegment(sketch, "E54.top", {"start": v(66.92, 102.24) * mm, "end": v(1984.62, 102.24) * mm});
            skLineSegment(sketch, "E54.left", {"start": v(66.92, 191.14) * mm, "end": v(66.92, 102.24) * mm});
            skLineSegment(sketch, "E54.right", {"start": v(1984.62, 191.14) * mm, "end": v(1984.62, 102.24) * mm});
            skPoint(sketch, "E55", {"position": v(76.44, 162.57) * mm});
            skPoint(sketch, "E56", {"position": v(76.44, 146.7) * mm});
            skPoint(sketch, "E57", {"position": v(76.44, 130.82) * mm});
            skPoint(sketch, "E58", {"position": v(1975.1, 162.57) * mm});
            skPoint(sketch, "E59", {"position": v(1975.1, 146.7) * mm});
            skPoint(sketch, "E60", {"position": v(1975.1, 130.82) * mm});
            skPoint(sketch, "E61", {"position": v(701.92, 162.57) * mm});
            skPoint(sketch, "E62", {"position": v(701.92, 146.7) * mm});
            skPoint(sketch, "E63", {"position": v(701.92, 130.82) * mm});
            skPoint(sketch, "E64", {"position": v(1349.62, 162.57) * mm});
            skPoint(sketch, "E65", {"position": v(1349.62, 146.7) * mm});
            skPoint(sketch, "E66", {"position": v(1349.62, 130.82) * mm});
            skPoint(sketch, "E67", {"position": v(389.18, 146.7) * mm});
            skPoint(sketch, "E68", {"position": v(1662.34, 146.7) * mm});
            skSolve(sketch);
        }
        {
            var Q0;
            Q0=makeQuery(id+"F51.imprint","IMPRINT",FACE,{"disambiguationData":[TD([[makeQuery(id+"F51.imprint","IMPRINT",EDGE,{"derivedFrom":sQuery(id+"F51.wireOp",EDGE,"E54.bottom")}),-1.0]])]});
            extrude(context, id + "F52", {"entities" : qUnion([Q0]), "depth" : 19.05 * mm, "offsetDistance" : 25.4 * mm});
        }
        {
            var Q0;
            Q0=sQuery(id+"F51.wireOp",VERTEX,"E55");
            var Q1;
            Q1=makeQuery(id+"F52.opExtrude","SWEPT_BODY",BODY,{"disambiguationData":[OSD([sQuery(id+"F51.wireOp",EDGE,"E54.bottom"),sQuery(id+"F51.wireOp",EDGE,"E54.top"),sQuery(id+"F51.wireOp",EDGE,"E54.left"),sQuery(id+"F51.wireOp",EDGE,"E54.right")])]});
            hole(context, id + "F53", {"style" : HoleStyle.SIMPLE, "endStyle" : HoleEndStyle.THROUGH, "oppositeDirection" : true, "holeDiameter" : 6.35 * mm, "majorDiameter" : 6.35 * mm, "isTappedThrough" : true, "tappedDepth" : 12.7 * mm, "tapClearance" : 3, "locations" : qUnion([Q0]), "scope" : qUnion([Q1])});
        }
        {
            var Q0;
            Q0=sQuery(id+"F51.wireOp",VERTEX,"E57");
            var Q1;
            Q1=makeQuery(id+"F52.opExtrude","SWEPT_BODY",BODY,{"disambiguationData":[OSD([sQuery(id+"F51.wireOp",EDGE,"E54.bottom"),sQuery(id+"F51.wireOp",EDGE,"E54.top"),sQuery(id+"F51.wireOp",EDGE,"E54.left"),sQuery(id+"F51.wireOp",EDGE,"E54.right")])]});
            hole(context, id + "F54", {"style" : HoleStyle.SIMPLE, "endStyle" : HoleEndStyle.THROUGH, "oppositeDirection" : true, "holeDiameter" : 6.35 * mm, "majorDiameter" : 6.35 * mm, "isTappedThrough" : true, "tappedDepth" : 12.7 * mm, "tapClearance" : 3, "locations" : qUnion([Q0]), "scope" : qUnion([Q1])});
        }
        {
            var Q0;
            Q0=sQuery(id+"F51.wireOp",VERTEX,"E56");
            var Q1;
            Q1=makeQuery(id+"F52.opExtrude","SWEPT_BODY",BODY,{"disambiguationData":[OSD([sQuery(id+"F51.wireOp",EDGE,"E54.bottom"),sQuery(id+"F51.wireOp",EDGE,"E54.top"),sQuery(id+"F51.wireOp",EDGE,"E54.left"),sQuery(id+"F51.wireOp",EDGE,"E54.right")])]});
            hole(context, id + "F55", {"style" : HoleStyle.SIMPLE, "endStyle" : HoleEndStyle.THROUGH, "oppositeDirection" : true, "holeDiameter" : 3.3 * mm, "majorDiameter" : 6.35 * mm, "isTappedThrough" : true, "tappedDepth" : 12.7 * mm, "tapClearance" : 3, "locations" : qUnion([Q0]), "scope" : qUnion([Q1])});
        }
        {
            var Q0;
            Q0=sQuery(id+"F51.wireOp",VERTEX,"E59");
            var Q1;
            Q1=makeQuery(id+"F52.opExtrude","SWEPT_BODY",BODY,{"disambiguationData":[OSD([sQuery(id+"F51.wireOp",EDGE,"E54.bottom"),sQuery(id+"F51.wireOp",EDGE,"E54.top"),sQuery(id+"F51.wireOp",EDGE,"E54.left"),sQuery(id+"F51.wireOp",EDGE,"E54.right")])]});
            hole(context, id + "F56", {"style" : HoleStyle.SIMPLE, "endStyle" : HoleEndStyle.THROUGH, "oppositeDirection" : true, "holeDiameter" : 3.3 * mm, "majorDiameter" : 6.35 * mm, "isTappedThrough" : true, "tappedDepth" : 12.7 * mm, "tapClearance" : 3, "locations" : qUnion([Q0]), "scope" : qUnion([Q1])});
        }
        {
            var Q0;
            Q0=sQuery(id+"F51.wireOp",VERTEX,"E58");
            var Q1;
            Q1=makeQuery(id+"F52.opExtrude","SWEPT_BODY",BODY,{"disambiguationData":[OSD([sQuery(id+"F51.wireOp",EDGE,"E54.bottom"),sQuery(id+"F51.wireOp",EDGE,"E54.top"),sQuery(id+"F51.wireOp",EDGE,"E54.left"),sQuery(id+"F51.wireOp",EDGE,"E54.right")])]});
            hole(context, id + "F57", {"style" : HoleStyle.SIMPLE, "endStyle" : HoleEndStyle.THROUGH, "oppositeDirection" : true, "holeDiameter" : 6.35 * mm, "majorDiameter" : 6.35 * mm, "isTappedThrough" : true, "tappedDepth" : 12.7 * mm, "tapClearance" : 3, "locations" : qUnion([Q0]), "scope" : qUnion([Q1])});
        }
        {
            var Q0;
            Q0=sQuery(id+"F51.wireOp",VERTEX,"E60");
            var Q1;
            Q1=makeQuery(id+"F52.opExtrude","SWEPT_BODY",BODY,{"disambiguationData":[OSD([sQuery(id+"F51.wireOp",EDGE,"E54.bottom"),sQuery(id+"F51.wireOp",EDGE,"E54.top"),sQuery(id+"F51.wireOp",EDGE,"E54.left"),sQuery(id+"F51.wireOp",EDGE,"E54.right")])]});
            hole(context, id + "F58", {"style" : HoleStyle.SIMPLE, "endStyle" : HoleEndStyle.THROUGH, "oppositeDirection" : true, "holeDiameter" : 6.35 * mm, "majorDiameter" : 6.35 * mm, "isTappedThrough" : true, "tappedDepth" : 12.7 * mm, "tapClearance" : 3, "locations" : qUnion([Q0]), "scope" : qUnion([Q1])});
        }
        {
            var Q0;
            Q0=sQuery(id+"F51.wireOp",VERTEX,"E64");
            var Q1;
            Q1=makeQuery(id+"F52.opExtrude","SWEPT_BODY",BODY,{"disambiguationData":[OSD([sQuery(id+"F51.wireOp",EDGE,"E54.bottom"),sQuery(id+"F51.wireOp",EDGE,"E54.top"),sQuery(id+"F51.wireOp",EDGE,"E54.left"),sQuery(id+"F51.wireOp",EDGE,"E54.right")])]});
            hole(context, id + "F59", {"style" : HoleStyle.SIMPLE, "endStyle" : HoleEndStyle.THROUGH, "oppositeDirection" : true, "holeDiameter" : 6.35 * mm, "majorDiameter" : 6.35 * mm, "isTappedThrough" : true, "tappedDepth" : 12.7 * mm, "tapClearance" : 3, "locations" : qUnion([Q0]), "scope" : qUnion([Q1])});
        }
        {
            var Q0;
            Q0=sQuery(id+"F51.wireOp",VERTEX,"E66");
            var Q1;
            Q1=makeQuery(id+"F52.opExtrude","SWEPT_BODY",BODY,{"disambiguationData":[OSD([sQuery(id+"F51.wireOp",EDGE,"E54.bottom"),sQuery(id+"F51.wireOp",EDGE,"E54.top"),sQuery(id+"F51.wireOp",EDGE,"E54.left"),sQuery(id+"F51.wireOp",EDGE,"E54.right")])]});
            hole(context, id + "F60", {"style" : HoleStyle.SIMPLE, "endStyle" : HoleEndStyle.THROUGH, "oppositeDirection" : true, "holeDiameter" : 6.35 * mm, "majorDiameter" : 6.35 * mm, "isTappedThrough" : true, "tappedDepth" : 12.7 * mm, "tapClearance" : 3, "locations" : qUnion([Q0]), "scope" : qUnion([Q1])});
        }
        {
            var Q0;
            Q0=sQuery(id+"F51.wireOp",VERTEX,"E61");
            var Q1;
            Q1=makeQuery(id+"F52.opExtrude","SWEPT_BODY",BODY,{"disambiguationData":[OSD([sQuery(id+"F51.wireOp",EDGE,"E54.bottom"),sQuery(id+"F51.wireOp",EDGE,"E54.top"),sQuery(id+"F51.wireOp",EDGE,"E54.left"),sQuery(id+"F51.wireOp",EDGE,"E54.right")])]});
            hole(context, id + "F61", {"style" : HoleStyle.SIMPLE, "endStyle" : HoleEndStyle.THROUGH, "oppositeDirection" : true, "holeDiameter" : 6.35 * mm, "majorDiameter" : 6.35 * mm, "isTappedThrough" : true, "tappedDepth" : 12.7 * mm, "tapClearance" : 3, "locations" : qUnion([Q0]), "scope" : qUnion([Q1])});
        }
        {
            var Q0;
            Q0=sQuery(id+"F51.wireOp",VERTEX,"E63");
            var Q1;
            Q1=makeQuery(id+"F52.opExtrude","SWEPT_BODY",BODY,{"disambiguationData":[OSD([sQuery(id+"F51.wireOp",EDGE,"E54.bottom"),sQuery(id+"F51.wireOp",EDGE,"E54.top"),sQuery(id+"F51.wireOp",EDGE,"E54.left"),sQuery(id+"F51.wireOp",EDGE,"E54.right")])]});
            hole(context, id + "F62", {"style" : HoleStyle.SIMPLE, "endStyle" : HoleEndStyle.THROUGH, "oppositeDirection" : true, "holeDiameter" : 6.35 * mm, "majorDiameter" : 6.35 * mm, "isTappedThrough" : true, "tappedDepth" : 12.7 * mm, "tapClearance" : 3, "locations" : qUnion([Q0]), "scope" : qUnion([Q1])});
        }
        {
            var Q0;
            Q0=sQuery(id+"F51.wireOp",VERTEX,"E62");
            var Q1;
            Q1=makeQuery(id+"F52.opExtrude","SWEPT_BODY",BODY,{"disambiguationData":[OSD([sQuery(id+"F51.wireOp",EDGE,"E54.bottom"),sQuery(id+"F51.wireOp",EDGE,"E54.top"),sQuery(id+"F51.wireOp",EDGE,"E54.left"),sQuery(id+"F51.wireOp",EDGE,"E54.right")])]});
            hole(context, id + "F63", {"style" : HoleStyle.SIMPLE, "endStyle" : HoleEndStyle.THROUGH, "oppositeDirection" : true, "holeDiameter" : 3.3 * mm, "majorDiameter" : 6.35 * mm, "isTappedThrough" : true, "tappedDepth" : 12.7 * mm, "tapClearance" : 3, "locations" : qUnion([Q0]), "scope" : qUnion([Q1])});
        }
        {
            var Q0;
            Q0=sQuery(id+"F51.wireOp",VERTEX,"E65");
            var Q1;
            Q1=makeQuery(id+"F52.opExtrude","SWEPT_BODY",BODY,{"disambiguationData":[OSD([sQuery(id+"F51.wireOp",EDGE,"E54.bottom"),sQuery(id+"F51.wireOp",EDGE,"E54.top"),sQuery(id+"F51.wireOp",EDGE,"E54.left"),sQuery(id+"F51.wireOp",EDGE,"E54.right")])]});
            hole(context, id + "F64", {"style" : HoleStyle.SIMPLE, "endStyle" : HoleEndStyle.THROUGH, "oppositeDirection" : true, "holeDiameter" : 3.3 * mm, "majorDiameter" : 6.35 * mm, "isTappedThrough" : true, "tappedDepth" : 12.7 * mm, "tapClearance" : 3, "locations" : qUnion([Q0]), "scope" : qUnion([Q1])});
        }
        {
            var Q0;
            Q0=qCreatedBy(makeId("Front.planeOp"),FACE);
            var sketch = newSketch(context, id + "F65", { "sketchPlane" : qUnion([Q0])});
            skLineSegment(sketch, "E69.bottom", {"start": v(-769.9, 464.25) * mm, "end": v(-163.48, 464.25) * mm});
            skLineSegment(sketch, "E69.top", {"start": v(-769.9, 32.45) * mm, "end": v(-163.48, 32.45) * mm});
            skLineSegment(sketch, "E69.left", {"start": v(-769.9, 464.25) * mm, "end": v(-769.9, 32.45) * mm});
            skLineSegment(sketch, "E69.right", {"start": v(-163.48, 464.25) * mm, "end": v(-163.48, 32.45) * mm});
            skSolve(sketch);
        }
        {
            var Q0;
            Q0=makeQuery(id+"F65.imprint","IMPRINT",FACE,{"disambiguationData":[TD([[makeQuery(id+"F65.imprint","IMPRINT",EDGE,{"derivedFrom":sQuery(id+"F65.wireOp",EDGE,"E69.bottom")}),-1.0]])]});
            extrude(context, id + "F66", {"entities" : qUnion([Q0]), "depth" : 6.35 * mm, "offsetDistance" : 25.4 * mm});
        }
        {
            var Q0;
            Q0=makeQuery(id+"F66.opExtrude","CAP_FACE",FACE,{"disambiguationData":[OSD([sQuery(id+"F65.wireOp",EDGE,"E69.bottom"),sQuery(id+"F65.wireOp",EDGE,"E69.top"),sQuery(id+"F65.wireOp",EDGE,"E69.left"),sQuery(id+"F65.wireOp",EDGE,"E69.right")])],"isStart":false});
            var sketch = newSketch(context, id + "F67", { "sketchPlane" : qUnion([Q0])});
            skLineSegment(sketch, "E70.bottom", {"start": v(-761.23, -52.93) * mm, "end": v(-138.93, -52.93) * mm});
            skLineSegment(sketch, "E70.top", {"start": v(-761.23, -484.73) * mm, "end": v(-138.93, -484.73) * mm});
            skLineSegment(sketch, "E70.left", {"start": v(-761.23, -52.93) * mm, "end": v(-761.23, -484.73) * mm});
            skLineSegment(sketch, "E70.right", {"start": v(-138.93, -52.93) * mm, "end": v(-138.93, -484.73) * mm});
            skSolve(sketch);
        }
        {
            var Q0;
            Q0=makeQuery(id+"F67.imprint","IMPRINT",FACE,{"disambiguationData":[TD([[makeQuery(id+"F67.imprint","IMPRINT",EDGE,{"derivedFrom":sQuery(id+"F67.wireOp",EDGE,"E70.bottom")}),-1.0]])]});
            extrude(context, id + "F68", {"entities" : qUnion([Q0]), "depth" : 6.35 * mm, "offsetDistance" : 25.4 * mm});
        }
        {
            var Q0;
            Q0=qCreatedBy(makeId("Top.planeOp"),FACE);
            var sketch = newSketch(context, id + "F69", { "sketchPlane" : qUnion([Q0])});
            skLineSegment(sketch, "E71.bottom", {"start": v(-2018.55, 898.82) * mm, "end": v(-1412.12, 898.82) * mm});
            skLineSegment(sketch, "E71.top", {"start": v(-2018.55, 225.72) * mm, "end": v(-1412.12, 225.72) * mm});
            skLineSegment(sketch, "E71.left", {"start": v(-2037.6, 835.32) * mm, "end": v(-2037.6, 314.62) * mm});
            skLineSegment(sketch, "E71.right", {"start": v(-119.9, 835.32) * mm, "end": v(-119.9, 314.62) * mm});
            skLineSegment(sketch, "E72", {"start": v(-2018.55, 898.82) * mm, "end": v(-2018.55, 835.32) * mm});
            skLineSegment(sketch, "E73", {"start": v(-2018.55, 835.32) * mm, "end": v(-2037.6, 835.32) * mm});
            skLineSegment(sketch, "E74", {"start": v(-138.95, 898.82) * mm, "end": v(-138.95, 835.32) * mm});
            skLineSegment(sketch, "E75", {"start": v(-138.95, 835.32) * mm, "end": v(-119.9, 835.32) * mm});
            skLineSegment(sketch, "E76", {"start": v(-1412.12, 835.32) * mm, "end": v(-1393.07, 835.32) * mm});
            skLineSegment(sketch, "E77", {"start": v(-1393.07, 898.82) * mm, "end": v(-1393.07, 835.32) * mm});
            skLineSegment(sketch, "E78", {"start": v(-1412.12, 835.32) * mm, "end": v(-1412.12, 898.82) * mm});
            skLineSegment(sketch, "E79.trimOffspring", {"start": v(-1393.07, 898.82) * mm, "end": v(-764.42, 898.82) * mm});
            skLineSegment(sketch, "E80.trimOffspring", {"start": v(-1393.07, 225.72) * mm, "end": v(-764.42, 225.72) * mm});
            skLineSegment(sketch, "E81", {"start": v(-745.37, 835.32) * mm, "end": v(-745.37, 898.82) * mm});
            skLineSegment(sketch, "E82", {"start": v(-745.37, 898.82) * mm, "end": v(-745.37, 835.32) * mm});
            skLineSegment(sketch, "E83", {"start": v(-745.37, 835.32) * mm, "end": v(-764.42, 835.32) * mm});
            skLineSegment(sketch, "E84", {"start": v(-764.42, 898.82) * mm, "end": v(-764.42, 835.32) * mm});
            skLineSegment(sketch, "E85.trimOffspring", {"start": v(-745.37, 898.82) * mm, "end": v(-138.95, 898.82) * mm});
            skLineSegment(sketch, "E86.trimOffspring", {"start": v(-745.37, 225.72) * mm, "end": v(-138.95, 225.72) * mm});
            skLineSegment(sketch, "E87", {"start": v(-138.95, 225.72) * mm, "end": v(-138.95, 314.62) * mm});
            skLineSegment(sketch, "E88", {"start": v(-119.9, 314.62) * mm, "end": v(-138.95, 314.62) * mm});
            skLineSegment(sketch, "E89", {"start": v(-764.42, 225.72) * mm, "end": v(-764.42, 314.62) * mm});
            skLineSegment(sketch, "E90", {"start": v(-764.42, 314.62) * mm, "end": v(-745.37, 314.62) * mm});
            skLineSegment(sketch, "E91", {"start": v(-745.37, 225.72) * mm, "end": v(-745.37, 314.62) * mm});
            skLineSegment(sketch, "E92", {"start": v(-1412.12, 225.72) * mm, "end": v(-1412.12, 314.62) * mm});
            skLineSegment(sketch, "E93", {"start": v(-1412.12, 314.62) * mm, "end": v(-1393.07, 314.62) * mm});
            skLineSegment(sketch, "E94", {"start": v(-1393.07, 314.62) * mm, "end": v(-1393.07, 225.72) * mm});
            skLineSegment(sketch, "E95", {"start": v(-2018.55, 225.72) * mm, "end": v(-2018.55, 314.62) * mm});
            skLineSegment(sketch, "E96", {"start": v(-2018.55, 314.62) * mm, "end": v(-2037.6, 314.62) * mm});
            skSolve(sketch);
        }
        {
            var Q0;
            Q0=makeQuery(id+"F69.imprint","IMPRINT",FACE,{"disambiguationData":[TD([[makeQuery(id+"F69.imprint","IMPRINT",EDGE,{"derivedFrom":sQuery(id+"F69.wireOp",EDGE,"E71.bottom")}),-1.0]])]});
            extrude(context, id + "F70", {"entities" : qUnion([Q0]), "depth" : 6.35 * mm, "offsetDistance" : 25.4 * mm});
        }
        {
            var Q0;
            Q0=qCreatedBy(makeId("Right.planeOp"),FACE);
            var sketch = newSketch(context, id + "F71", { "sketchPlane" : qUnion([Q0])});
            skLineSegment(sketch, "E97.bottom", {"start": v(143.95, -75.1) * mm, "end": v(859.92, -75.1) * mm});
            skLineSegment(sketch, "E97.top", {"start": v(143.95, -170.35) * mm, "end": v(859.92, -170.35) * mm});
            skLineSegment(sketch, "E97.left", {"start": v(143.95, -75.1) * mm, "end": v(143.95, -170.35) * mm});
            skLineSegment(sketch, "E97.right", {"start": v(859.92, -75.1) * mm, "end": v(859.92, -170.35) * mm});
            skSolve(sketch);
        }
        {
            var Q0;
            Q0=makeQuery(id+"F71.imprint","IMPRINT",FACE,{"disambiguationData":[TD([[makeQuery(id+"F71.imprint","IMPRINT",EDGE,{"derivedFrom":sQuery(id+"F71.wireOp",EDGE,"E97.bottom")}),-1.0]])]});
            extrude(context, id + "F72", {"entities" : qUnion([Q0]), "depth" : 17.48 * mm, "offsetDistance" : 25.4 * mm});
        }
        {
            var Q0;
            Q0=makeQuery(id+"F72.opExtrude","CAP_EDGE",EDGE,{"disambiguationData":[OSD([sQuery(id+"F71.wireOp",EDGE,"E97.left")])],"isStart":false});
            chamfer(context, id + "F73", {"entities" : qUnion([Q0]), "width" : 17.48 * mm, "tangentPropagation" : true});
        }
        {
            var Q0;
            Q0=qCreatedBy(makeId("Right.planeOp"),FACE);
            var sketch = newSketch(context, id + "F74", { "sketchPlane" : qUnion([Q0])});
            skLineSegment(sketch, "E98.bottom", {"start": v(95.55, -196.36) * mm, "end": v(2048.2, -196.36) * mm});
            skLineSegment(sketch, "E98.top", {"start": v(95.55, -291.6) * mm, "end": v(2048.2, -291.6) * mm});
            skLineSegment(sketch, "E98.left", {"start": v(95.55, -196.36) * mm, "end": v(95.55, -291.6) * mm});
            skLineSegment(sketch, "E98.right", {"start": v(2048.2, -196.36) * mm, "end": v(2048.2, -291.6) * mm});
            skSolve(sketch);
        }
        {
            var Q0;
            Q0=makeQuery(id+"F74.imprint","IMPRINT",FACE,{"disambiguationData":[TD([[makeQuery(id+"F74.imprint","IMPRINT",EDGE,{"derivedFrom":sQuery(id+"F74.wireOp",EDGE,"E98.bottom")}),-1.0]])]});
            extrude(context, id + "F75", {"entities" : qUnion([Q0]), "depth" : 17.48 * mm, "offsetDistance" : 25.4 * mm});
        }
        {
            var Q0;
            Q0=makeQuery(id+"F75.opExtrude","CAP_EDGE",EDGE,{"disambiguationData":[OSD([sQuery(id+"F74.wireOp",EDGE,"E98.left")])],"isStart":false});
            chamfer(context, id + "F76", {"entities" : qUnion([Q0]), "width" : 17.48 * mm, "tangentPropagation" : true});
        }
        {
            var Q0;
            Q0=makeQuery(id+"F75.opExtrude","CAP_EDGE",EDGE,{"disambiguationData":[OSD([sQuery(id+"F74.wireOp",EDGE,"E98.right")])],"isStart":false});
            chamfer(context, id + "F77", {"entities" : qUnion([Q0]), "width" : 17.48 * mm, "tangentPropagation" : true});
        }
        {
            var Q0;
            Q0=qCreatedBy(makeId("Front.planeOp"),FACE);
            var sketch = newSketch(context, id + "F78", { "sketchPlane" : qUnion([Q0])});
            skLineSegment(sketch, "E99.bottom", {"start": v(127.94, 200.63) * mm, "end": v(623.24, 200.63) * mm});
            skLineSegment(sketch, "E99.top", {"start": v(127.94, 111.73) * mm, "end": v(623.24, 111.73) * mm});
            skLineSegment(sketch, "E99.left", {"start": v(127.94, 200.63) * mm, "end": v(127.94, 111.73) * mm});
            skLineSegment(sketch, "E99.right", {"start": v(623.24, 200.63) * mm, "end": v(623.24, 111.73) * mm});
            skPoint(sketch, "E100", {"position": v(375.6, 187.93) * mm});
            skPoint(sketch, "E100.positionSnap0", {"position": v(375.6, 200.63) * mm});
            skPoint(sketch, "E101", {"position": v(375.6, 172.06) * mm});
            skLineSegment(sketch, "E102", {"start": v(127.94, 200.63) * mm, "end": v(127.94, 194.28) * mm});
            skLineSegment(sketch, "E103", {"start": v(127.94, 194.28) * mm, "end": v(623.24, 194.28) * mm});
            skSolve(sketch);
        }
        {
            var Q0;
            Q0=makeQuery(id+"F78.imprint","IMPRINT",FACE,{"disambiguationData":[TD([[makeQuery(id+"F78.imprint","IMPRINT",EDGE,{"derivedFrom":sQuery(id+"F78.wireOp",EDGE,"E99.bottom")}),-1.0]])]});
            extrude(context, id + "F79", {"entities" : qUnion([Q0]), "depth" : 12.7 * mm, "offsetDistance" : 25.4 * mm});
        }
        {
            var Q0;
            Q0=qCreatedBy(makeId("Front.planeOp"),FACE);
            var sketch = newSketch(context, id + "F80", { "sketchPlane" : qUnion([Q0])});
            skLineSegment(sketch, "E104.bottom", {"start": v(127.7, 311.4) * mm, "end": v(623, 311.4) * mm});
            skLineSegment(sketch, "E104.top", {"start": v(127.7, 222.5) * mm, "end": v(623, 222.5) * mm});
            skLineSegment(sketch, "E104.left", {"start": v(127.7, 311.4) * mm, "end": v(127.7, 222.5) * mm});
            skLineSegment(sketch, "E104.right", {"start": v(623, 311.4) * mm, "end": v(623, 222.5) * mm});
            skLineSegment(sketch, "E105", {"start": v(127.7, 222.5) * mm, "end": v(127.7, 228.86) * mm});
            skLineSegment(sketch, "E106", {"start": v(127.7, 228.86) * mm, "end": v(623, 228.86) * mm});
            skSolve(sketch);
        }
        {
            var Q0;
            {var subQ0=sQuery(id+"F80.wireOp",EDGE,"E104.bottom");Q0=makeQuery(id+"F80.imprint","IMPRINT",FACE,{"disambiguationData":[TD([[makeQuery(id+"F80.imprint","IMPRINT",EDGE,{"derivedFrom":subQ0}),-1.0]])]});}
            extrude(context, id + "F81", {"entities" : qUnion([Q0]), "depth" : 19.05 * mm, "offsetDistance" : 25.4 * mm});
        }
        {
            var Q0;
            Q0=makeQuery(id+"F81.opExtrude","SWEPT_FACE",FACE,{"disambiguationData":[OSD([sQuery(id+"F80.wireOp",EDGE,"E104.left")])]});
            var sketch = newSketch(context, id + "F82", { "sketchPlane" : qUnion([Q0])});
            skLineSegment(sketch, "E107.0.0", {"start": v(0, 311.4) * mm, "end": v(0, 311.4) * mm});
            skLineSegment(sketch, "E107.0.1", {"start": v(19.05, 311.4) * mm, "end": v(0, 311.4) * mm});
            skLineSegment(sketch, "E107.0.2", {"start": v(19.05, 311.4) * mm, "end": v(19.05, 311.4) * mm});
            skLineSegment(sketch, "E107.0.3", {"start": v(19.05, 311.4) * mm, "end": v(0, 311.4) * mm});
            skPoint(sketch, "E108", {"position": v(9.53, 282.83) * mm});
            skPoint(sketch, "E108.positionSnap0", {"position": v(9.53, 311.4) * mm});
            skPoint(sketch, "E109", {"position": v(9.53, 251.08) * mm});
            skSolve(sketch);
        }
        {
            var Q0;
            Q0=sQuery(id+"F82.wireOp",VERTEX,"E108");
            var Q1;
            Q1=makeQuery(id+"F81.opExtrude","SWEPT_BODY",BODY,{"disambiguationData":[OSD([sQuery(id+"F80.wireOp",EDGE,"E104.bottom"),sQuery(id+"F80.wireOp",EDGE,"E104.top"),sQuery(id+"F80.wireOp",EDGE,"E104.left"),sQuery(id+"F80.wireOp",EDGE,"E104.right")])]});
            hole(context, id + "F83", {"style" : HoleStyle.SIMPLE, "endStyle" : HoleEndStyle.BLIND, "holeDiameter" : 6.35 * mm, "majorDiameter" : 6.35 * mm, "holeDepth" : 25.4 * mm, "isTappedThrough" : true, "tappedDepth" : 12.7 * mm, "tapClearance" : 3, "locations" : qUnion([Q0]), "scope" : qUnion([Q1])});
        }
        {
            var Q0;
            Q0=sQuery(id+"F82.wireOp",VERTEX,"E109");
            var Q1;
            Q1=makeQuery(id+"F81.opExtrude","SWEPT_BODY",BODY,{"disambiguationData":[OSD([sQuery(id+"F80.wireOp",EDGE,"E104.bottom"),sQuery(id+"F80.wireOp",EDGE,"E104.left"),sQuery(id+"F80.wireOp",EDGE,"E104.right"),sQuery(id+"F80.wireOp",EDGE,"E106")])]});
            hole(context, id + "F84", {"style" : HoleStyle.SIMPLE, "endStyle" : HoleEndStyle.BLIND, "holeDiameter" : 6.35 * mm, "majorDiameter" : 6.35 * mm, "holeDepth" : 25.4 * mm, "isTappedThrough" : true, "tappedDepth" : 12.7 * mm, "tapClearance" : 3, "locations" : qUnion([Q0]), "scope" : qUnion([Q1])});
        }
        {
            var Q0;
            Q0=makeQuery(id+"F81.opExtrude","SWEPT_FACE",FACE,{"disambiguationData":[OSD([sQuery(id+"F80.wireOp",EDGE,"E104.right")])]});
            var sketch = newSketch(context, id + "F85", { "sketchPlane" : qUnion([Q0])});
            skLineSegment(sketch, "E110.0.0", {"start": v(0, 311.4) * mm, "end": v(0, 311.4) * mm});
            skLineSegment(sketch, "E110.0.1", {"start": v(0, 311.4) * mm, "end": v(-19.05, 311.4) * mm});
            skLineSegment(sketch, "E110.0.2", {"start": v(-19.05, 311.4) * mm, "end": v(-19.05, 311.4) * mm});
            skLineSegment(sketch, "E110.0.3", {"start": v(0, 311.4) * mm, "end": v(-19.05, 311.4) * mm});
            skPoint(sketch, "E111", {"position": v(-9.53, 282.83) * mm});
            skPoint(sketch, "E111.positionSnap0", {"position": v(-9.53, 311.4) * mm});
            skPoint(sketch, "E112", {"position": v(-9.53, 251.08) * mm});
            skSolve(sketch);
        }
        {
            var Q0;
            Q0=sQuery(id+"F85.wireOp",VERTEX,"E111");
            var Q1;
            Q1=makeQuery(id+"F81.opExtrude","SWEPT_BODY",BODY,{"disambiguationData":[OSD([sQuery(id+"F80.wireOp",EDGE,"E104.bottom"),sQuery(id+"F80.wireOp",EDGE,"E104.top"),sQuery(id+"F80.wireOp",EDGE,"E104.left"),sQuery(id+"F80.wireOp",EDGE,"E104.right")])]});
            hole(context, id + "F86", {"style" : HoleStyle.SIMPLE, "endStyle" : HoleEndStyle.BLIND, "holeDiameter" : 6.35 * mm, "majorDiameter" : 6.35 * mm, "holeDepth" : 25.4 * mm, "isTappedThrough" : true, "tappedDepth" : 12.7 * mm, "tapClearance" : 3, "locations" : qUnion([Q0]), "scope" : qUnion([Q1])});
        }
        {
            var Q0;
            Q0=sQuery(id+"F51.wireOp",VERTEX,"E68");
            var Q1;
            Q1=makeQuery(id+"F52.opExtrude","SWEPT_BODY",BODY,{"disambiguationData":[OSD([sQuery(id+"F51.wireOp",EDGE,"E54.bottom"),sQuery(id+"F51.wireOp",EDGE,"E54.top"),sQuery(id+"F51.wireOp",EDGE,"E54.left"),sQuery(id+"F51.wireOp",EDGE,"E54.right")])]});
            hole(context, id + "F87", {"style" : HoleStyle.SIMPLE, "endStyle" : HoleEndStyle.THROUGH, "oppositeDirection" : true, "holeDiameter" : 5.33 * mm, "majorDiameter" : 6.35 * mm, "isTappedThrough" : true, "tappedDepth" : 12.7 * mm, "tapClearance" : 3, "locations" : qUnion([Q0]), "scope" : qUnion([Q1])});
        }
        {
            var Q0;
            Q0=sQuery(id+"F51.wireOp",VERTEX,"E67");
            var Q1;
            Q1=makeQuery(id+"F52.opExtrude","SWEPT_BODY",BODY,{"disambiguationData":[OSD([sQuery(id+"F51.wireOp",EDGE,"E54.bottom"),sQuery(id+"F51.wireOp",EDGE,"E54.top"),sQuery(id+"F51.wireOp",EDGE,"E54.left"),sQuery(id+"F51.wireOp",EDGE,"E54.right")])]});
            hole(context, id + "F88", {"style" : HoleStyle.SIMPLE, "endStyle" : HoleEndStyle.THROUGH, "oppositeDirection" : true, "holeDiameter" : 5.33 * mm, "majorDiameter" : 6.35 * mm, "isTappedThrough" : true, "tappedDepth" : 12.7 * mm, "tapClearance" : 3, "locations" : qUnion([Q0]), "scope" : qUnion([Q1])});
        }
        {
            var Q0;
            Q0=qCreatedBy(makeId("Top.planeOp"),FACE);
            var sketch = newSketch(context, id + "F89", { "sketchPlane" : qUnion([Q0])});
            skLineSegment(sketch, "E113.bottom", {"start": v(-2019.33, 1820.1) * mm, "end": v(-1412.9, 1820.1) * mm});
            skLineSegment(sketch, "E113.top", {"start": v(-2019.33, 1159.7) * mm, "end": v(-1412.9, 1159.7) * mm});
            skLineSegment(sketch, "E113.left", {"start": v(-2038.38, 1731.2) * mm, "end": v(-2038.38, 1248.6) * mm});
            skLineSegment(sketch, "E113.right", {"start": v(-120.68, 1731.2) * mm, "end": v(-120.68, 1248.6) * mm});
            skLineSegment(sketch, "E114", {"start": v(-2019.33, 1820.1) * mm, "end": v(-2019.33, 1731.2) * mm});
            skLineSegment(sketch, "E115", {"start": v(-2019.33, 1731.2) * mm, "end": v(-2038.38, 1731.2) * mm});
            skLineSegment(sketch, "E116", {"start": v(-139.73, 1820.1) * mm, "end": v(-139.73, 1731.2) * mm});
            skLineSegment(sketch, "E117", {"start": v(-139.73, 1731.2) * mm, "end": v(-120.68, 1731.2) * mm});
            skLineSegment(sketch, "E118", {"start": v(-1412.9, 1731.2) * mm, "end": v(-1393.86, 1731.2) * mm});
            skLineSegment(sketch, "E119", {"start": v(-1393.86, 1820.1) * mm, "end": v(-1393.86, 1731.2) * mm});
            skLineSegment(sketch, "E120", {"start": v(-1412.9, 1731.2) * mm, "end": v(-1412.9, 1820.1) * mm});
            skLineSegment(sketch, "E121.trimOffspring", {"start": v(-1393.86, 1820.1) * mm, "end": v(-765.2, 1820.1) * mm});
            skLineSegment(sketch, "E122.trimOffspring", {"start": v(-1393.86, 1159.7) * mm, "end": v(-765.2, 1159.7) * mm});
            skLineSegment(sketch, "E123", {"start": v(-746.16, 1731.2) * mm, "end": v(-746.16, 1820.1) * mm});
            skLineSegment(sketch, "E124", {"start": v(-746.16, 1820.1) * mm, "end": v(-746.16, 1731.2) * mm});
            skLineSegment(sketch, "E125", {"start": v(-746.16, 1731.2) * mm, "end": v(-765.2, 1731.2) * mm});
            skLineSegment(sketch, "E126", {"start": v(-765.2, 1820.1) * mm, "end": v(-765.2, 1731.2) * mm});
            skLineSegment(sketch, "E127.trimOffspring", {"start": v(-746.16, 1820.1) * mm, "end": v(-139.73, 1820.1) * mm});
            skLineSegment(sketch, "E128.trimOffspring", {"start": v(-746.16, 1159.7) * mm, "end": v(-139.73, 1159.7) * mm});
            skLineSegment(sketch, "E129", {"start": v(-139.73, 1159.7) * mm, "end": v(-139.73, 1248.6) * mm});
            skLineSegment(sketch, "E130", {"start": v(-120.68, 1248.6) * mm, "end": v(-139.73, 1248.6) * mm});
            skLineSegment(sketch, "E131", {"start": v(-765.2, 1159.7) * mm, "end": v(-765.2, 1248.6) * mm});
            skLineSegment(sketch, "E132", {"start": v(-765.2, 1248.6) * mm, "end": v(-746.16, 1248.6) * mm});
            skLineSegment(sketch, "E133", {"start": v(-746.16, 1159.7) * mm, "end": v(-746.16, 1248.6) * mm});
            skLineSegment(sketch, "E134", {"start": v(-1412.9, 1159.7) * mm, "end": v(-1412.9, 1248.6) * mm});
            skLineSegment(sketch, "E135", {"start": v(-1412.9, 1248.6) * mm, "end": v(-1393.86, 1248.6) * mm});
            skLineSegment(sketch, "E136", {"start": v(-1393.86, 1248.6) * mm, "end": v(-1393.86, 1159.7) * mm});
            skLineSegment(sketch, "E137", {"start": v(-2019.33, 1159.7) * mm, "end": v(-2019.33, 1248.6) * mm});
            skLineSegment(sketch, "E138", {"start": v(-2019.33, 1248.6) * mm, "end": v(-2038.38, 1248.6) * mm});
            skSolve(sketch);
        }
        {
            var Q0;
            Q0=makeQuery(id+"F89.imprint","IMPRINT",FACE,{"disambiguationData":[TD([[makeQuery(id+"F89.imprint","IMPRINT",EDGE,{"derivedFrom":sQuery(id+"F89.wireOp",EDGE,"E113.bottom")}),-1.0]])]});
            extrude(context, id + "F90", {"entities" : qUnion([Q0]), "depth" : 6.35 * mm, "offsetDistance" : 25.4 * mm});
        }
        {
            var Q0;
            Q0=qCreatedBy(makeId("Right.planeOp"),FACE);
            var sketch = newSketch(context, id + "F91", { "sketchPlane" : qUnion([Q0])});
            skLineSegment(sketch, "E139.bottom", {"start": v(210.68, -350.51) * mm, "end": v(883.78, -350.51) * mm});
            skLineSegment(sketch, "E139.top", {"start": v(210.68, -445.76) * mm, "end": v(883.78, -445.76) * mm});
            skLineSegment(sketch, "E139.left", {"start": v(210.68, -350.51) * mm, "end": v(210.68, -445.76) * mm});
            skLineSegment(sketch, "E139.right", {"start": v(883.78, -350.51) * mm, "end": v(883.78, -445.76) * mm});
            skSolve(sketch);
        }
        {
            var Q0;
            Q0=makeQuery(id+"F91.imprint","IMPRINT",FACE,{"disambiguationData":[TD([[makeQuery(id+"F91.imprint","IMPRINT",EDGE,{"derivedFrom":sQuery(id+"F91.wireOp",EDGE,"E139.bottom")}),-1.0]])]});
            extrude(context, id + "F92", {"entities" : qUnion([Q0]), "depth" : 17.48 * mm, "offsetDistance" : 25.4 * mm});
        }
        {
            var Q0;
            Q0=qCreatedBy(makeId("Front.planeOp"),FACE);
            var sketch = newSketch(context, id + "F93", { "sketchPlane" : qUnion([Q0])});
            skLineSegment(sketch, "E140.bottom", {"start": v(-1466.59, 407) * mm, "end": v(-971.29, 407) * mm});
            skLineSegment(sketch, "E140.top", {"start": v(-1466.59, 102.2) * mm, "end": v(-971.29, 102.2) * mm});
            skLineSegment(sketch, "E140.left", {"start": v(-1466.59, 407) * mm, "end": v(-1466.59, 102.2) * mm});
            skLineSegment(sketch, "E140.right", {"start": v(-971.29, 407) * mm, "end": v(-971.29, 102.2) * mm});
            skSolve(sketch);
        }
        {
            var Q0;
            Q0=makeQuery(id+"F93.imprint","IMPRINT",FACE,{"disambiguationData":[TD([[makeQuery(id+"F93.imprint","IMPRINT",EDGE,{"derivedFrom":sQuery(id+"F93.wireOp",EDGE,"E140.bottom")}),-1.0]])]});
            extrude(context, id + "F94", {"entities" : qUnion([Q0]), "depth" : 6.35 * mm, "offsetDistance" : 25.4 * mm});
        }
        {
            var Q0;
            Q0=makeQuery(id+"F90.opExtrude","CAP_FACE",FACE,{"disambiguationData":[OSD([sQuery(id+"F89.wireOp",EDGE,"E113.bottom"),sQuery(id+"F89.wireOp",EDGE,"E113.top"),sQuery(id+"F89.wireOp",EDGE,"E113.left"),sQuery(id+"F89.wireOp",EDGE,"E113.right"),sQuery(id+"F89.wireOp",EDGE,"E114"),sQuery(id+"F89.wireOp",EDGE,"E115"),sQuery(id+"F89.wireOp",EDGE,"E116"),sQuery(id+"F89.wireOp",EDGE,"E117"),sQuery(id+"F89.wireOp",EDGE,"E118"),sQuery(id+"F89.wireOp",EDGE,"E119"),sQuery(id+"F89.wireOp",EDGE,"E120"),sQuery(id+"F89.wireOp",EDGE,"E121.trimOffspring"),sQuery(id+"F89.wireOp",EDGE,"E122.trimOffspring"),sQuery(id+"F89.wireOp",EDGE,"E124"),sQuery(id+"F89.wireOp",EDGE,"E125"),sQuery(id+"F89.wireOp",EDGE,"E126"),sQuery(id+"F89.wireOp",EDGE,"E127.trimOffspring"),sQuery(id+"F89.wireOp",EDGE,"E128.trimOffspring"),sQuery(id+"F89.wireOp",EDGE,"E129"),sQuery(id+"F89.wireOp",EDGE,"E130"),sQuery(id+"F89.wireOp",EDGE,"E131"),sQuery(id+"F89.wireOp",EDGE,"E132"),sQuery(id+"F89.wireOp",EDGE,"E133"),sQuery(id+"F89.wireOp",EDGE,"E134"),sQuery(id+"F89.wireOp",EDGE,"E135"),sQuery(id+"F89.wireOp",EDGE,"E136"),sQuery(id+"F89.wireOp",EDGE,"E137"),sQuery(id+"F89.wireOp",EDGE,"E138")])],"isStart":false});
            var sketch = newSketch(context, id + "F95", { "sketchPlane" : qUnion([Q0])});
            skLineSegment(sketch, "E141.bottom", {"start": v(321.8, 2135.97) * mm, "end": v(2239.5, 2135.97) * mm});
            skLineSegment(sketch, "E141.top", {"start": v(321.8, 1113.62) * mm, "end": v(2239.5, 1113.62) * mm});
            skLineSegment(sketch, "E141.left", {"start": v(321.8, 2135.97) * mm, "end": v(321.8, 1113.62) * mm});
            skLineSegment(sketch, "E141.right", {"start": v(2239.5, 2135.97) * mm, "end": v(2239.5, 1113.62) * mm});
            skSolve(sketch);
        }
        {
            var Q0;
            Q0=makeQuery(id+"F95.imprint","IMPRINT",FACE,{"disambiguationData":[TD([[makeQuery(id+"F95.imprint","IMPRINT",EDGE,{"derivedFrom":sQuery(id+"F95.wireOp",EDGE,"E141.bottom")}),-1.0]])]});
            extrude(context, id + "F96", {"entities" : qUnion([Q0]), "depth" : 6.35 * mm, "offsetDistance" : 25.4 * mm});
        }
        {
            var Q0;
            Q0=qCreatedBy(makeId("Front.planeOp"),FACE);
            var sketch = newSketch(context, id + "F97", { "sketchPlane" : qUnion([Q0])});
            skLineSegment(sketch, "E142.bottom", {"start": v(823.05, -448.77) * mm, "end": v(892.9, -448.77) * mm});
            skLineSegment(sketch, "E142.left", {"start": v(804, -359.87) * mm, "end": v(804, -67.77) * mm});
            skLineSegment(sketch, "E142.right", {"start": v(892.9, -448.77) * mm, "end": v(892.9, 668.83) * mm});
            skLineSegment(sketch, "E143", {"start": v(823.05, -448.77) * mm, "end": v(823.05, -359.87) * mm});
            skLineSegment(sketch, "E144", {"start": v(823.05, -359.87) * mm, "end": v(804, -359.87) * mm});
            skLineSegment(sketch, "E145", {"start": v(823.05, -67.77) * mm, "end": v(804, -67.77) * mm});
            skLineSegment(sketch, "E146", {"start": v(823.05, -67.77) * mm, "end": v(823.05, 21.13) * mm});
            skLineSegment(sketch, "E147", {"start": v(823.05, 21.13) * mm, "end": v(804, 21.13) * mm});
            skLineSegment(sketch, "E148.trimOffspring", {"start": v(804, 21.13) * mm, "end": v(804, 389.43) * mm});
            skLineSegment(sketch, "E149.trimOffspring", {"start": v(804, 478.33) * mm, "end": v(804, 579.93) * mm});
            skLineSegment(sketch, "E150", {"start": v(804, 579.93) * mm, "end": v(823.05, 579.93) * mm});
            skLineSegment(sketch, "E151", {"start": v(823.05, 579.93) * mm, "end": v(823.05, 668.83) * mm});
            skLineSegment(sketch, "E152", {"start": v(823.05, 668.83) * mm, "end": v(892.9, 668.83) * mm});
            skLineSegment(sketch, "E153", {"start": v(804, 389.43) * mm, "end": v(804, 478.33) * mm});
            skSolve(sketch);
        }
        {
            var Q0;
            Q0=makeQuery(id+"F97.imprint","IMPRINT",FACE,{"disambiguationData":[TD([[makeQuery(id+"F97.imprint","IMPRINT",EDGE,{"derivedFrom":sQuery(id+"F97.wireOp",EDGE,"E142.bottom")}),1.0]])]});
            extrude(context, id + "F98", {"entities" : qUnion([Q0]), "endBound" : BoundingType.SYMMETRIC, "depth" : 19.05 * mm, "offsetDistance" : 25.4 * mm});
        }
        {
            var Q0;
            Q0=makeQuery(id+"F98.opExtrude","SWEPT_FACE",FACE,{"disambiguationData":[OSD([sQuery(id+"F97.wireOp",EDGE,"E142.right")])]});
            var sketch = newSketch(context, id + "F99", { "sketchPlane" : qUnion([Q0])});
            skLineSegment(sketch, "E154.0.0", {"start": v(9.53, -448.77) * mm, "end": v(9.53, -448.77) * mm});
            skLineSegment(sketch, "E154.0.1", {"start": v(-9.53, -448.77) * mm, "end": v(9.52, -448.77) * mm});
            skLineSegment(sketch, "E154.0.2", {"start": v(-9.53, -448.77) * mm, "end": v(-9.53, -448.77) * mm});
            skLineSegment(sketch, "E154.0.3", {"start": v(-9.53, -448.77) * mm, "end": v(9.52, -448.77) * mm});
            skPoint(sketch, "E155", {"position": v(0, -420.2) * mm});
            skPoint(sketch, "E155.positionSnap0", {"position": v(0, -448.77) * mm});
            skPoint(sketch, "E156", {"position": v(0, -388.45) * mm});
            skPoint(sketch, "E157", {"position": v(0, -39.2) * mm});
            skPoint(sketch, "E158", {"position": v(0, -7.45) * mm});
            skPoint(sketch, "E159", {"position": v(0, 640.25) * mm});
            skPoint(sketch, "E159.positionSnap0", {"position": v(0, 668.83) * mm});
            skPoint(sketch, "E160", {"position": v(0, 608.5) * mm});
            skSolve(sketch);
        }
        {
            var Q0;
            Q0=sQuery(id+"F99.wireOp",VERTEX,"E155");
            var Q1;
            Q1=makeQuery(id+"F98.opExtrude","SWEPT_BODY",BODY,{"disambiguationData":[OSD([sQuery(id+"F97.wireOp",EDGE,"E142.bottom"),sQuery(id+"F97.wireOp",EDGE,"E142.top"),sQuery(id+"F97.wireOp",EDGE,"E142.left"),sQuery(id+"F97.wireOp",EDGE,"E142.right"),sQuery(id+"F97.wireOp",EDGE,"E143"),sQuery(id+"F97.wireOp",EDGE,"E144"),sQuery(id+"F97.wireOp",EDGE,"E145"),sQuery(id+"F97.wireOp",EDGE,"E146"),sQuery(id+"F97.wireOp",EDGE,"E147"),sQuery(id+"F97.wireOp",EDGE,"E148.trimOffspring"),sQuery(id+"F97.wireOp",EDGE,"xzlXD9Uc-zntg-19ul-ZDs3-clXaPwfaJ8oG"),sQuery(id+"F97.wireOp",EDGE,"9509TwrL-qA23-4FMz-0eCz-VKt3BfyenOdl"),sQuery(id+"F97.wireOp",EDGE,"6oP95qg5-mBpY-Sm6Q-dXcN-RjPaqLq57M9H"),sQuery(id+"F97.wireOp",EDGE,"E149.trimOffspring"),sQuery(id+"F97.wireOp",EDGE,"tSUXJUD3-FyRw-fAfU-02JN-fgyFVIaL92aU"),sQuery(id+"F97.wireOp",EDGE,"iDVflDJI-pnAs-KQYt-8swf-mvtkYDpaG4Ws"),sQuery(id+"F97.wireOp",EDGE,"LdyIaMQR-zD5l-0WwF-STrR-elAvo1ggceAe"),sQuery(id+"F97.wireOp",EDGE,"pb9ndDva-6bUM-uIpz-MKsT-bSv5z0lPxj9r"),sQuery(id+"F97.wireOp",EDGE,"M6L3ovHu-wxFM-09rO-hudK-8UJthFq0l5m1"),sQuery(id+"F97.wireOp",EDGE,"78a3d17d-5802-40ae-9b7e-a7fa1afc7e56.trimOffspring")])]});
            hole(context, id + "F100", {"style" : HoleStyle.SIMPLE, "endStyle" : HoleEndStyle.BLIND, "holeDiameter" : 6.35 * mm, "majorDiameter" : 6.35 * mm, "holeDepth" : 25.4 * mm, "isTappedThrough" : true, "tappedDepth" : 12.7 * mm, "tapClearance" : 3, "locations" : qUnion([Q0]), "scope" : qUnion([Q1])});
        }
        {
            var Q0;
            Q0=sQuery(id+"F99.wireOp",VERTEX,"E156");
            var Q1;
            Q1=makeQuery(id+"F98.opExtrude","SWEPT_BODY",BODY,{"disambiguationData":[OSD([sQuery(id+"F97.wireOp",EDGE,"E142.bottom"),sQuery(id+"F97.wireOp",EDGE,"E142.top"),sQuery(id+"F97.wireOp",EDGE,"E142.left"),sQuery(id+"F97.wireOp",EDGE,"E142.right"),sQuery(id+"F97.wireOp",EDGE,"E143"),sQuery(id+"F97.wireOp",EDGE,"E144"),sQuery(id+"F97.wireOp",EDGE,"E145"),sQuery(id+"F97.wireOp",EDGE,"E146"),sQuery(id+"F97.wireOp",EDGE,"E147"),sQuery(id+"F97.wireOp",EDGE,"E148.trimOffspring"),sQuery(id+"F97.wireOp",EDGE,"xzlXD9Uc-zntg-19ul-ZDs3-clXaPwfaJ8oG"),sQuery(id+"F97.wireOp",EDGE,"9509TwrL-qA23-4FMz-0eCz-VKt3BfyenOdl"),sQuery(id+"F97.wireOp",EDGE,"6oP95qg5-mBpY-Sm6Q-dXcN-RjPaqLq57M9H"),sQuery(id+"F97.wireOp",EDGE,"E149.trimOffspring"),sQuery(id+"F97.wireOp",EDGE,"tSUXJUD3-FyRw-fAfU-02JN-fgyFVIaL92aU"),sQuery(id+"F97.wireOp",EDGE,"iDVflDJI-pnAs-KQYt-8swf-mvtkYDpaG4Ws"),sQuery(id+"F97.wireOp",EDGE,"LdyIaMQR-zD5l-0WwF-STrR-elAvo1ggceAe"),sQuery(id+"F97.wireOp",EDGE,"pb9ndDva-6bUM-uIpz-MKsT-bSv5z0lPxj9r"),sQuery(id+"F97.wireOp",EDGE,"M6L3ovHu-wxFM-09rO-hudK-8UJthFq0l5m1"),sQuery(id+"F97.wireOp",EDGE,"78a3d17d-5802-40ae-9b7e-a7fa1afc7e56.trimOffspring")])]});
            hole(context, id + "F101", {"style" : HoleStyle.SIMPLE, "endStyle" : HoleEndStyle.BLIND, "holeDiameter" : 6.35 * mm, "majorDiameter" : 6.35 * mm, "holeDepth" : 25.4 * mm, "isTappedThrough" : true, "tappedDepth" : 12.7 * mm, "tapClearance" : 3, "locations" : qUnion([Q0]), "scope" : qUnion([Q1])});
        }
        {
            var Q0;
            Q0=sQuery(id+"F99.wireOp",VERTEX,"E158");
            var Q1;
            Q1=sQuery(id+"F99.wireOp",VERTEX,"E157");
            var Q2;
            Q2=sQuery(id+"F99.wireOp",VERTEX,"652dc356-8beb-4057-947e-6c245722714f");
            var Q3;
            Q3=sQuery(id+"F99.wireOp",VERTEX,"1a8ab31c-8b8a-4ee4-9016-32992395cb1c");
            var Q4;
            Q4=makeQuery(id+"F98.opExtrude","SWEPT_BODY",BODY,{"disambiguationData":[OSD([sQuery(id+"F97.wireOp",EDGE,"E142.bottom"),sQuery(id+"F97.wireOp",EDGE,"E142.top"),sQuery(id+"F97.wireOp",EDGE,"E142.left"),sQuery(id+"F97.wireOp",EDGE,"E142.right"),sQuery(id+"F97.wireOp",EDGE,"E143"),sQuery(id+"F97.wireOp",EDGE,"E144"),sQuery(id+"F97.wireOp",EDGE,"E145"),sQuery(id+"F97.wireOp",EDGE,"E146"),sQuery(id+"F97.wireOp",EDGE,"E147"),sQuery(id+"F97.wireOp",EDGE,"E148.trimOffspring"),sQuery(id+"F97.wireOp",EDGE,"xzlXD9Uc-zntg-19ul-ZDs3-clXaPwfaJ8oG"),sQuery(id+"F97.wireOp",EDGE,"9509TwrL-qA23-4FMz-0eCz-VKt3BfyenOdl"),sQuery(id+"F97.wireOp",EDGE,"6oP95qg5-mBpY-Sm6Q-dXcN-RjPaqLq57M9H"),sQuery(id+"F97.wireOp",EDGE,"E149.trimOffspring"),sQuery(id+"F97.wireOp",EDGE,"tSUXJUD3-FyRw-fAfU-02JN-fgyFVIaL92aU"),sQuery(id+"F97.wireOp",EDGE,"iDVflDJI-pnAs-KQYt-8swf-mvtkYDpaG4Ws"),sQuery(id+"F97.wireOp",EDGE,"LdyIaMQR-zD5l-0WwF-STrR-elAvo1ggceAe"),sQuery(id+"F97.wireOp",EDGE,"pb9ndDva-6bUM-uIpz-MKsT-bSv5z0lPxj9r"),sQuery(id+"F97.wireOp",EDGE,"M6L3ovHu-wxFM-09rO-hudK-8UJthFq0l5m1"),sQuery(id+"F97.wireOp",EDGE,"78a3d17d-5802-40ae-9b7e-a7fa1afc7e56.trimOffspring")])]});
            hole(context, id + "F102", {"style" : HoleStyle.SIMPLE, "endStyle" : HoleEndStyle.BLIND, "holeDiameter" : 6.35 * mm, "majorDiameter" : 6.35 * mm, "holeDepth" : 25.4 * mm, "isTappedThrough" : true, "tappedDepth" : 12.7 * mm, "tapClearance" : 3, "locations" : qUnion([Q0, Q1, Q2, Q3]), "scope" : qUnion([Q4])});
        }
        {
            var Q0;
            Q0=makeQuery(id+"F98.opExtrude","CAP_FACE",FACE,{"disambiguationData":[OSD([sQuery(id+"F97.wireOp",EDGE,"E142.bottom"),sQuery(id+"F97.wireOp",EDGE,"E142.top"),sQuery(id+"F97.wireOp",EDGE,"E142.left"),sQuery(id+"F97.wireOp",EDGE,"E142.right"),sQuery(id+"F97.wireOp",EDGE,"E143"),sQuery(id+"F97.wireOp",EDGE,"E144"),sQuery(id+"F97.wireOp",EDGE,"E145"),sQuery(id+"F97.wireOp",EDGE,"E146"),sQuery(id+"F97.wireOp",EDGE,"E147"),sQuery(id+"F97.wireOp",EDGE,"E148.trimOffspring"),sQuery(id+"F97.wireOp",EDGE,"xzlXD9Uc-zntg-19ul-ZDs3-clXaPwfaJ8oG"),sQuery(id+"F97.wireOp",EDGE,"9509TwrL-qA23-4FMz-0eCz-VKt3BfyenOdl"),sQuery(id+"F97.wireOp",EDGE,"6oP95qg5-mBpY-Sm6Q-dXcN-RjPaqLq57M9H"),sQuery(id+"F97.wireOp",EDGE,"E149.trimOffspring"),sQuery(id+"F97.wireOp",EDGE,"tSUXJUD3-FyRw-fAfU-02JN-fgyFVIaL92aU"),sQuery(id+"F97.wireOp",EDGE,"iDVflDJI-pnAs-KQYt-8swf-mvtkYDpaG4Ws"),sQuery(id+"F97.wireOp",EDGE,"LdyIaMQR-zD5l-0WwF-STrR-elAvo1ggceAe"),sQuery(id+"F97.wireOp",EDGE,"pb9ndDva-6bUM-uIpz-MKsT-bSv5z0lPxj9r"),sQuery(id+"F97.wireOp",EDGE,"M6L3ovHu-wxFM-09rO-hudK-8UJthFq0l5m1"),sQuery(id+"F97.wireOp",EDGE,"78a3d17d-5802-40ae-9b7e-a7fa1afc7e56.trimOffspring")])],"isStart":false});
            var sketch = newSketch(context, id + "F103", { "sketchPlane" : qUnion([Q0])});
            skLineSegment(sketch, "E161.bottom", {"start": v(992.7, 483.74) * mm, "end": v(1094.3, 483.74) * mm});
            skLineSegment(sketch, "E161.top", {"start": v(992.7, 394.84) * mm, "end": v(1094.3, 394.84) * mm});
            skLineSegment(sketch, "E161.left", {"start": v(992.7, 483.74) * mm, "end": v(992.7, 394.84) * mm});
            skLineSegment(sketch, "E161.right", {"start": v(1094.3, 483.74) * mm, "end": v(1094.3, 394.84) * mm});
            skSolve(sketch);
        }
        {
            var Q0;
            Q0=makeQuery(id+"F103.imprint","IMPRINT",FACE,{"disambiguationData":[TD([[makeQuery(id+"F103.imprint","IMPRINT",EDGE,{"derivedFrom":sQuery(id+"F103.wireOp",EDGE,"E161.bottom")}),-1.0]])]});
            extrude(context, id + "F104", {"entities" : qUnion([Q0]), "depth" : 19.05 * mm, "offsetDistance" : 25.4 * mm});
        }
        {
            var Q0;
            Q0=makeQuery(id+"F104.opExtrude","SWEPT_FACE",FACE,{"disambiguationData":[OSD([sQuery(id+"F103.wireOp",EDGE,"E161.right")])]});
            var sketch = newSketch(context, id + "F105", { "sketchPlane" : qUnion([Q0])});
            skLineSegment(sketch, "E162.0.0", {"start": v(-9.53, 394.84) * mm, "end": v(-9.53, 483.74) * mm});
            skLineSegment(sketch, "E162.0.1", {"start": v(-9.53, 483.74) * mm, "end": v(-28.58, 483.74) * mm});
            skLineSegment(sketch, "E162.0.2", {"start": v(-28.58, 483.74) * mm, "end": v(-28.58, 394.84) * mm});
            skLineSegment(sketch, "E162.0.3", {"start": v(-28.58, 394.84) * mm, "end": v(-9.53, 394.84) * mm});
            skPoint(sketch, "E163", {"position": v(-19.05, 423.41) * mm});
            skPoint(sketch, "E163.positionSnap0", {"position": v(-19.05, 394.84) * mm});
            skPoint(sketch, "E164", {"position": v(-19.05, 455.16) * mm});
            skPoint(sketch, "E164.positionSnap0", {"position": v(-19.05, 483.74) * mm});
            skSolve(sketch);
        }
        {
            var Q0;
            Q0=sQuery(id+"F105.wireOp",VERTEX,"E164");
            var Q1;
            Q1=sQuery(id+"F105.wireOp",VERTEX,"E163");
            var Q2;
            Q2=makeQuery(id+"F104.opExtrude","SWEPT_BODY",BODY,{"disambiguationData":[OSD([sQuery(id+"F103.wireOp",EDGE,"E161.bottom"),sQuery(id+"F103.wireOp",EDGE,"E161.top"),sQuery(id+"F103.wireOp",EDGE,"E161.left"),sQuery(id+"F103.wireOp",EDGE,"E161.right")])]});
            hole(context, id + "F106", {"style" : HoleStyle.SIMPLE, "endStyle" : HoleEndStyle.BLIND, "holeDiameter" : 6.35 * mm, "majorDiameter" : 6.35 * mm, "holeDepth" : 25.4 * mm, "isTappedThrough" : true, "tappedDepth" : 12.7 * mm, "tapClearance" : 3, "locations" : qUnion([Q0, Q1]), "scope" : qUnion([Q2])});
        }
        {
            var Q0;
            Q0=makeQuery(id+"F104.opExtrude","SWEPT_FACE",FACE,{"disambiguationData":[OSD([sQuery(id+"F103.wireOp",EDGE,"E161.left")])]});
            var sketch = newSketch(context, id + "F107", { "sketchPlane" : qUnion([Q0])});
            skLineSegment(sketch, "E165.0.0", {"start": v(9.53, 483.74) * mm, "end": v(9.53, 394.84) * mm});
            skLineSegment(sketch, "E165.0.1", {"start": v(9.53, 394.84) * mm, "end": v(28.58, 394.84) * mm});
            skLineSegment(sketch, "E165.0.2", {"start": v(28.58, 394.84) * mm, "end": v(28.58, 483.74) * mm});
            skLineSegment(sketch, "E165.0.3", {"start": v(28.58, 483.74) * mm, "end": v(9.53, 483.74) * mm});
            skPoint(sketch, "E166", {"position": v(19.05, 455.16) * mm});
            skPoint(sketch, "E166.positionSnap0", {"position": v(19.05, 483.74) * mm});
            skPoint(sketch, "E167", {"position": v(19.05, 423.41) * mm});
            skPoint(sketch, "E167.positionSnap0", {"position": v(19.05, 394.84) * mm});
            skSolve(sketch);
        }
        {
            var Q0;
            Q0=sQuery(id+"F107.wireOp",VERTEX,"E166");
            var Q1;
            Q1=sQuery(id+"F107.wireOp",VERTEX,"E167");
            var Q2;
            Q2=makeQuery(id+"F104.opExtrude","SWEPT_BODY",BODY,{"disambiguationData":[OSD([sQuery(id+"F103.wireOp",EDGE,"E161.bottom"),sQuery(id+"F103.wireOp",EDGE,"E161.top"),sQuery(id+"F103.wireOp",EDGE,"E161.left"),sQuery(id+"F103.wireOp",EDGE,"E161.right")])]});
            hole(context, id + "F108", {"style" : HoleStyle.SIMPLE, "endStyle" : HoleEndStyle.BLIND, "holeDiameter" : 6.35 * mm, "majorDiameter" : 6.35 * mm, "holeDepth" : 25.4 * mm, "isTappedThrough" : true, "tappedDepth" : 12.7 * mm, "tapClearance" : 3, "locations" : qUnion([Q0, Q1]), "scope" : qUnion([Q2])});
        }
        {
            var Q0;
            Q0=qCreatedBy(makeId("Top.planeOp"),FACE);
            var sketch = newSketch(context, id + "F109", { "sketchPlane" : qUnion([Q0])});
            skLineSegment(sketch, "E168.bottom", {"start": v(-3154.83, 4175.02) * mm, "end": v(-1135.53, 4175.02) * mm});
            skLineSegment(sketch, "E168.top", {"start": v(-3154.83, 2257.32) * mm, "end": v(-1135.53, 2257.32) * mm});
            skLineSegment(sketch, "E168.left", {"start": v(-3154.83, 4175.02) * mm, "end": v(-3154.83, 2257.32) * mm});
            skLineSegment(sketch, "E168.right", {"start": v(-1135.53, 4175.02) * mm, "end": v(-1135.53, 2257.32) * mm});
            skSolve(sketch);
        }
        {
            var Q0;
            Q0=makeQuery(id+"F109.imprint","IMPRINT",FACE,{"disambiguationData":[TD([[makeQuery(id+"F109.imprint","IMPRINT",EDGE,{"derivedFrom":sQuery(id+"F109.wireOp",EDGE,"E168.bottom")}),-1.0]])]});
            extrude(context, id + "F110", {"entities" : qUnion([Q0]), "depth" : 241.3 * mm, "offsetDistance" : 25.4 * mm});
        }
        {
            var Q0;
            Q0=makeQuery(id+"F110.opExtrude","CAP_EDGE",EDGE,{"disambiguationData":[OSD([sQuery(id+"F109.wireOp",EDGE,"E168.top")])],"isStart":false});
            var Q1;
            Q1=makeQuery(id+"F110.opExtrude","SWEPT_EDGE",EDGE,{"disambiguationData":[OSD([sQuery(id+"F109.wireOp",EDGE,"E168.top"),sQuery(id+"F109.wireOp",EDGE,"E168.left")])]});
            var Q2;
            Q2=makeQuery(id+"F110.opExtrude","CAP_EDGE",EDGE,{"disambiguationData":[OSD([sQuery(id+"F109.wireOp",EDGE,"E168.left")])],"isStart":false});
            var Q3;
            Q3=makeQuery(id+"F110.opExtrude","CAP_EDGE",EDGE,{"disambiguationData":[OSD([sQuery(id+"F109.wireOp",EDGE,"E168.top")])],"isStart":true});
            var Q4;
            Q4=makeQuery(id+"F110.opExtrude","CAP_EDGE",EDGE,{"disambiguationData":[OSD([sQuery(id+"F109.wireOp",EDGE,"E168.left")])],"isStart":true});
            var Q5;
            Q5=makeQuery(id+"F110.opExtrude","SWEPT_EDGE",EDGE,{"disambiguationData":[OSD([sQuery(id+"F109.wireOp",EDGE,"E168.top"),sQuery(id+"F109.wireOp",EDGE,"E168.right")])]});
            var Q6;
            Q6=makeQuery(id+"F110.opExtrude","CAP_EDGE",EDGE,{"disambiguationData":[OSD([sQuery(id+"F109.wireOp",EDGE,"E168.right")])],"isStart":false});
            var Q7;
            Q7=makeQuery(id+"F110.opExtrude","CAP_EDGE",EDGE,{"disambiguationData":[OSD([sQuery(id+"F109.wireOp",EDGE,"E168.right")])],"isStart":true});
            var Q8;
            Q8=makeQuery(id+"F110.opExtrude","SWEPT_EDGE",EDGE,{"disambiguationData":[OSD([sQuery(id+"F109.wireOp",EDGE,"E168.bottom"),sQuery(id+"F109.wireOp",EDGE,"E168.right")])]});
            var Q9;
            Q9=makeQuery(id+"F110.opExtrude","CAP_EDGE",EDGE,{"disambiguationData":[OSD([sQuery(id+"F109.wireOp",EDGE,"E168.bottom")])],"isStart":false});
            var Q10;
            Q10=makeQuery(id+"F110.opExtrude","SWEPT_EDGE",EDGE,{"disambiguationData":[OSD([sQuery(id+"F109.wireOp",EDGE,"E168.bottom"),sQuery(id+"F109.wireOp",EDGE,"E168.left")])]});
            var Q11;
            Q11=makeQuery(id+"F110.opExtrude","CAP_EDGE",EDGE,{"disambiguationData":[OSD([sQuery(id+"F109.wireOp",EDGE,"E168.bottom")])],"isStart":true});
            fillet(context, id + "F111", {"entities" : qUnion([Q0, Q1, Q2, Q3, Q4, Q5, Q6, Q7, Q8, Q9, Q10, Q11]), "radius" : 25.4 * mm, "tangentPropagation" : true, "allowEdgeOverflow" : false});
        }
        {
            var Q0;
            Q0=makeQuery(id+"F98.opExtrude","SWEPT_FACE",FACE,{"disambiguationData":[OSD([sQuery(id+"F97.wireOp",EDGE,"E151")])]});
            var sketch = newSketch(context, id + "F112", { "sketchPlane" : qUnion([Q0])});
            skLineSegment(sketch, "E169.0.0", {"start": v(-9.53, 668.83) * mm, "end": v(-9.53, 579.93) * mm});
            skLineSegment(sketch, "E169.0.1", {"start": v(-9.52, 579.93) * mm, "end": v(9.53, 579.93) * mm});
            skLineSegment(sketch, "E169.0.2", {"start": v(9.53, 579.93) * mm, "end": v(9.53, 668.83) * mm});
            skLineSegment(sketch, "E169.0.3", {"start": v(9.53, 668.83) * mm, "end": v(-9.52, 668.83) * mm});
            skPoint(sketch, "E170", {"position": v(0, 640.25) * mm});
            skPoint(sketch, "E170.positionSnap0", {"position": v(0, 668.83) * mm});
            skPoint(sketch, "E171", {"position": v(0, 608.5) * mm});
            skPoint(sketch, "E171.positionSnap0", {"position": v(0, 579.93) * mm});
            skSolve(sketch);
        }
        {
            var Q0;
            Q0=sQuery(id+"F112.wireOp",VERTEX,"E170");
            var Q1;
            Q1=sQuery(id+"F112.wireOp",VERTEX,"E171");
            var Q2;
            Q2=makeQuery(id+"F98.opExtrude","SWEPT_BODY",BODY,{"disambiguationData":[OSD([sQuery(id+"F97.wireOp",EDGE,"E142.bottom"),sQuery(id+"F97.wireOp",EDGE,"E142.left"),sQuery(id+"F97.wireOp",EDGE,"E142.right"),sQuery(id+"F97.wireOp",EDGE,"E143"),sQuery(id+"F97.wireOp",EDGE,"E144"),sQuery(id+"F97.wireOp",EDGE,"E145"),sQuery(id+"F97.wireOp",EDGE,"E146"),sQuery(id+"F97.wireOp",EDGE,"E147"),sQuery(id+"F97.wireOp",EDGE,"E148.trimOffspring"),sQuery(id+"F97.wireOp",EDGE,"xzlXD9Uc-zntg-19ul-ZDs3-clXaPwfaJ8oG"),sQuery(id+"F97.wireOp",EDGE,"9509TwrL-qA23-4FMz-0eCz-VKt3BfyenOdl"),sQuery(id+"F97.wireOp",EDGE,"6oP95qg5-mBpY-Sm6Q-dXcN-RjPaqLq57M9H"),sQuery(id+"F97.wireOp",EDGE,"E149.trimOffspring"),sQuery(id+"F97.wireOp",EDGE,"E150"),sQuery(id+"F97.wireOp",EDGE,"E151"),sQuery(id+"F97.wireOp",EDGE,"E152")])]});
            hole(context, id + "F113", {"style" : HoleStyle.SIMPLE, "endStyle" : HoleEndStyle.BLIND, "holeDiameter" : 6.35 * mm, "majorDiameter" : 6.35 * mm, "holeDepth" : 25.4 * mm, "isTappedThrough" : true, "tappedDepth" : 12.7 * mm, "tapClearance" : 3, "locations" : qUnion([Q0, Q1]), "scope" : qUnion([Q2])});
        }
        {
            var Q0;
            Q0=sQuery(id+"F99.wireOp",VERTEX,"E159");
            var Q1;
            Q1=sQuery(id+"F99.wireOp",VERTEX,"E160");
            var Q2;
            Q2=makeQuery(id+"F98.opExtrude","SWEPT_BODY",BODY,{"disambiguationData":[OSD([sQuery(id+"F97.wireOp",EDGE,"E142.bottom"),sQuery(id+"F97.wireOp",EDGE,"E142.left"),sQuery(id+"F97.wireOp",EDGE,"E142.right"),sQuery(id+"F97.wireOp",EDGE,"E143"),sQuery(id+"F97.wireOp",EDGE,"E144"),sQuery(id+"F97.wireOp",EDGE,"E145"),sQuery(id+"F97.wireOp",EDGE,"E146"),sQuery(id+"F97.wireOp",EDGE,"E147"),sQuery(id+"F97.wireOp",EDGE,"E148.trimOffspring"),sQuery(id+"F97.wireOp",EDGE,"xzlXD9Uc-zntg-19ul-ZDs3-clXaPwfaJ8oG"),sQuery(id+"F97.wireOp",EDGE,"9509TwrL-qA23-4FMz-0eCz-VKt3BfyenOdl"),sQuery(id+"F97.wireOp",EDGE,"6oP95qg5-mBpY-Sm6Q-dXcN-RjPaqLq57M9H"),sQuery(id+"F97.wireOp",EDGE,"E149.trimOffspring"),sQuery(id+"F97.wireOp",EDGE,"E150"),sQuery(id+"F97.wireOp",EDGE,"E151"),sQuery(id+"F97.wireOp",EDGE,"E152")])]});
            hole(context, id + "F114", {"style" : HoleStyle.SIMPLE, "endStyle" : HoleEndStyle.BLIND, "holeDiameter" : 6.35 * mm, "majorDiameter" : 6.35 * mm, "holeDepth" : 25.4 * mm, "isTappedThrough" : true, "tappedDepth" : 12.7 * mm, "tapClearance" : 3, "locations" : qUnion([Q0, Q1]), "scope" : qUnion([Q2])});
        }
        {
            var Q0;
            Q0=makeQuery(id+"F96.opExtrude","CAP_FACE",FACE,{"disambiguationData":[OSD([sQuery(id+"F95.wireOp",EDGE,"E141.bottom"),sQuery(id+"F95.wireOp",EDGE,"E141.top"),sQuery(id+"F95.wireOp",EDGE,"E141.left"),sQuery(id+"F95.wireOp",EDGE,"E141.right")])],"isStart":false});
            var sketch = newSketch(context, id + "F115", { "sketchPlane" : qUnion([Q0])});
            skLineSegment(sketch, "E172.bottom", {"start": v(365.53, 3028.24) * mm, "end": v(2283.23, 3028.24) * mm});
            skLineSegment(sketch, "E172.top", {"start": v(365.53, 2380.54) * mm, "end": v(2283.23, 2380.54) * mm});
            skLineSegment(sketch, "E172.left", {"start": v(365.53, 3028.24) * mm, "end": v(365.53, 2380.54) * mm});
            skLineSegment(sketch, "E172.right", {"start": v(2283.23, 3028.24) * mm, "end": v(2283.23, 2380.54) * mm});
            skSolve(sketch);
        }
        {
            var Q0;
            Q0=makeQuery(id+"F115.imprint","IMPRINT",FACE,{"disambiguationData":[TD([[makeQuery(id+"F115.imprint","IMPRINT",EDGE,{"derivedFrom":sQuery(id+"F115.wireOp",EDGE,"E172.bottom")}),-1.0]])]});
            extrude(context, id + "F116", {"entities" : qUnion([Q0]), "depth" : 6.35 * mm, "offsetDistance" : 25.4 * mm});
        }
        {
            var Q0;
            Q0=qCreatedBy(makeId("Top.planeOp"),FACE);
            var sketch = newSketch(context, id + "F117", { "sketchPlane" : qUnion([Q0])});
            skLineSegment(sketch, "E173.bottom", {"start": v(348.24, 701.16) * mm, "end": v(954.67, 701.16) * mm});
            skLineSegment(sketch, "E173.top", {"start": v(348.24, 421.76) * mm, "end": v(954.67, 421.76) * mm});
            skLineSegment(sketch, "E173.left", {"start": v(348.24, 701.16) * mm, "end": v(348.24, 612.26) * mm});
            skLineSegment(sketch, "E173.right", {"start": v(954.67, 701.16) * mm, "end": v(954.67, 612.26) * mm});
            skLineSegment(sketch, "E174", {"start": v(954.67, 421.76) * mm, "end": v(954.67, 510.66) * mm});
            skLineSegment(sketch, "E175", {"start": v(954.67, 510.66) * mm, "end": v(973.72, 510.66) * mm});
            skLineSegment(sketch, "E176", {"start": v(973.72, 510.66) * mm, "end": v(973.72, 612.26) * mm});
            skLineSegment(sketch, "E177", {"start": v(973.72, 612.26) * mm, "end": v(954.67, 612.26) * mm});
            skLineSegment(sketch, "E178.trimOffspring", {"start": v(954.67, 510.66) * mm, "end": v(954.67, 421.76) * mm});
            skLineSegment(sketch, "E179", {"start": v(348.24, 421.76) * mm, "end": v(348.24, 510.66) * mm});
            skLineSegment(sketch, "E180", {"start": v(348.24, 510.66) * mm, "end": v(329.2, 510.66) * mm});
            skLineSegment(sketch, "E181", {"start": v(329.2, 510.66) * mm, "end": v(329.2, 612.26) * mm});
            skLineSegment(sketch, "E182", {"start": v(329.2, 612.26) * mm, "end": v(348.24, 612.26) * mm});
            skLineSegment(sketch, "E183.trimOffspring", {"start": v(348.24, 510.66) * mm, "end": v(348.24, 421.76) * mm});
            skSolve(sketch);
        }
        {
            var Q0;
            Q0=makeQuery(id+"F117.imprint","IMPRINT",FACE,{"disambiguationData":[TD([[makeQuery(id+"F117.imprint","IMPRINT",EDGE,{"derivedFrom":sQuery(id+"F117.wireOp",EDGE,"E173.bottom")}),-1.0]])]});
            extrude(context, id + "F118", {"entities" : qUnion([Q0]), "depth" : 6.35 * mm, "offsetDistance" : 25.4 * mm});
        }
        {
            var Q0;
            Q0=makeQuery(id+"F118.opExtrude","CAP_FACE",FACE,{"disambiguationData":[OSD([sQuery(id+"F117.wireOp",EDGE,"E173.bottom"),sQuery(id+"F117.wireOp",EDGE,"E173.top"),sQuery(id+"F117.wireOp",EDGE,"E173.right"),sQuery(id+"F117.wireOp",EDGE,"E175"),sQuery(id+"F117.wireOp",EDGE,"E176"),sQuery(id+"F117.wireOp",EDGE,"E177"),sQuery(id+"F117.wireOp",EDGE,"E178.trimOffspring"),sQuery(id+"F117.wireOp",EDGE,"E173.left"),sQuery(id+"F117.wireOp",EDGE,"E180"),sQuery(id+"F117.wireOp",EDGE,"E181"),sQuery(id+"F117.wireOp",EDGE,"E182"),sQuery(id+"F117.wireOp",EDGE,"E183.trimOffspring")])],"isStart":false});
            var sketch = newSketch(context, id + "F119", { "sketchPlane" : qUnion([Q0])});
            skLineSegment(sketch, "E184.bottom", {"start": v(1299.73, 707.98) * mm, "end": v(1394.98, 707.98) * mm});
            skLineSegment(sketch, "E184.top", {"start": v(1299.73, 428.58) * mm, "end": v(1394.98, 428.58) * mm});
            skLineSegment(sketch, "E184.left", {"start": v(1210.83, 688.93) * mm, "end": v(1210.83, 447.63) * mm});
            skLineSegment(sketch, "E184.right", {"start": v(1394.98, 707.98) * mm, "end": v(1394.98, 428.58) * mm});
            skLineSegment(sketch, "E185", {"start": v(1210.83, 688.93) * mm, "end": v(1299.73, 688.93) * mm});
            skLineSegment(sketch, "E186", {"start": v(1299.73, 688.93) * mm, "end": v(1299.73, 707.98) * mm});
            skLineSegment(sketch, "E187", {"start": v(1210.83, 447.63) * mm, "end": v(1299.73, 447.63) * mm});
            skLineSegment(sketch, "E188", {"start": v(1299.73, 447.63) * mm, "end": v(1299.73, 428.58) * mm});
            skSolve(sketch);
        }
        {
            var Q0;
            Q0 = qSketchRegion(id + "F119", true);
            var Q1;
            Q1=makeQuery(id+"F119.imprint","IMPRINT",FACE,{"disambiguationData":[TD([[makeQuery(id+"F119.imprint","IMPRINT",EDGE,{"derivedFrom":sQuery(id+"F119.wireOp",EDGE,"E184.bottom")}),-1.0]])]});
            extrude(context, id + "F120", {"entities" : qUnion([Q0, Q1]), "depth" : 6.35 * mm, "offsetDistance" : 25.4 * mm});
        }
        {
            var Q0;
            Q0=makeQuery(id+"F92.opExtrude","CAP_FACE",FACE,{"disambiguationData":[OSD([sQuery(id+"F91.wireOp",EDGE,"E139.bottom"),sQuery(id+"F91.wireOp",EDGE,"E139.top"),sQuery(id+"F91.wireOp",EDGE,"E139.left"),sQuery(id+"F91.wireOp",EDGE,"E139.right")])],"isStart":false});
            var sketch = newSketch(context, id + "F121", { "sketchPlane" : qUnion([Q0])});
            skLineSegment(sketch, "E189.bottom", {"start": v(223, -489) * mm, "end": v(502.4, -489) * mm});
            skLineSegment(sketch, "E189.top", {"start": v(223, -584.24) * mm, "end": v(502.4, -584.24) * mm});
            skLineSegment(sketch, "E189.left", {"start": v(223, -489) * mm, "end": v(223, -584.24) * mm});
            skLineSegment(sketch, "E189.right", {"start": v(502.4, -489) * mm, "end": v(502.4, -584.24) * mm});
            skSolve(sketch);
        }
        {
            var Q0;
            Q0=makeQuery(id+"F121.imprint","IMPRINT",FACE,{"disambiguationData":[TD([[makeQuery(id+"F121.imprint","IMPRINT",EDGE,{"derivedFrom":sQuery(id+"F121.wireOp",EDGE,"E189.bottom")}),-1.0]])]});
            extrude(context, id + "F122", {"entities" : qUnion([Q0]), "depth" : 17.48 * mm, "offsetDistance" : 25.4 * mm});
        }
        {
            var Q0;
            Q0=makeQuery(id+"F120.opExtrude","CAP_FACE",FACE,{"disambiguationData":[OSD([sQuery(id+"F119.wireOp",EDGE,"E184.bottom"),sQuery(id+"F119.wireOp",EDGE,"E184.top"),sQuery(id+"F119.wireOp",EDGE,"E184.left"),sQuery(id+"F119.wireOp",EDGE,"E184.right"),sQuery(id+"F119.wireOp",EDGE,"E185"),sQuery(id+"F119.wireOp",EDGE,"E186"),sQuery(id+"F119.wireOp",EDGE,"E187"),sQuery(id+"F119.wireOp",EDGE,"E188")])],"isStart":false});
            var sketch = newSketch(context, id + "F123", { "sketchPlane" : qUnion([Q0])});
            skLineSegment(sketch, "E190.bottom", {"start": v(1674.1, 719.44) * mm, "end": v(1953.5, 719.44) * mm});
            skLineSegment(sketch, "E190.top", {"start": v(1674.1, 427.34) * mm, "end": v(1953.5, 427.34) * mm});
            skLineSegment(sketch, "E190.left", {"start": v(1674.1, 719.44) * mm, "end": v(1674.1, 427.34) * mm});
            skLineSegment(sketch, "E190.right", {"start": v(1953.5, 719.44) * mm, "end": v(1953.5, 427.34) * mm});
            skSolve(sketch);
        }
        {
            var Q0;
            Q0=makeQuery(id+"F123.imprint","IMPRINT",FACE,{"disambiguationData":[TD([[makeQuery(id+"F123.imprint","IMPRINT",EDGE,{"derivedFrom":sQuery(id+"F123.wireOp",EDGE,"E190.bottom")}),-1.0]])]});
            extrude(context, id + "F124", {"entities" : qUnion([Q0]), "depth" : 6.35 * mm, "offsetDistance" : 25.4 * mm});
        }
        {
            var Q0;
            Q0=makeQuery(id+"F124.opExtrude","CAP_FACE",FACE,{"disambiguationData":[OSD([sQuery(id+"F123.wireOp",EDGE,"E190.bottom"),sQuery(id+"F123.wireOp",EDGE,"E190.top"),sQuery(id+"F123.wireOp",EDGE,"E190.left"),sQuery(id+"F123.wireOp",EDGE,"E190.right")])],"isStart":false});
            var sketch = newSketch(context, id + "F125", { "sketchPlane" : qUnion([Q0])});
            skLineSegment(sketch, "E191.bottom", {"start": v(2145.23, 811.39) * mm, "end": v(2786.58, 811.39) * mm});
            skLineSegment(sketch, "E191.top", {"start": v(2145.23, 519.29) * mm, "end": v(2786.58, 519.29) * mm});
            skLineSegment(sketch, "E191.left", {"start": v(2145.23, 811.39) * mm, "end": v(2145.23, 519.29) * mm});
            skLineSegment(sketch, "E191.right", {"start": v(2786.58, 811.39) * mm, "end": v(2786.58, 519.29) * mm});
            skSolve(sketch);
        }
        {
            var Q0;
            Q0=makeQuery(id+"F125.imprint","IMPRINT",FACE,{"disambiguationData":[TD([[makeQuery(id+"F125.imprint","IMPRINT",EDGE,{"derivedFrom":sQuery(id+"F125.wireOp",EDGE,"E191.bottom")}),-1.0]])]});
            extrude(context, id + "F126", {"entities" : qUnion([Q0]), "depth" : 6.35 * mm, "offsetDistance" : 25.4 * mm});
        }
        {
            var Q0;
            {var subQ0=sQuery(id+"F80.wireOp",EDGE,"E104.top");Q0=makeQuery(id+"F80.imprint","IMPRINT",FACE,{"disambiguationData":[TD([[makeQuery(id+"F80.imprint","IMPRINT",EDGE,{"derivedFrom":subQ0}),1.0]])]});}
            extrude(context, id + "F127", {"entities" : qUnion([Q0]), "operationType" : NewBodyOperationType.ADD, "depth" : 12.7 * mm, "offsetDistance" : 25.4 * mm});
        }
        {
            var Q0;
            {var subQ0=sQuery(id+"F78.wireOp",EDGE,"E99.top");Q0=makeQuery(id+"F78.imprint","IMPRINT",FACE,{"disambiguationData":[TD([[makeQuery(id+"F78.imprint","IMPRINT",EDGE,{"derivedFrom":subQ0}),1.0]])]});}
            extrude(context, id + "F128", {"entities" : qUnion([Q0]), "operationType" : NewBodyOperationType.ADD, "depth" : 19.05 * mm, "offsetDistance" : 25.4 * mm});
        }
        {
            var Q0;
            Q0=sQuery(id+"F78.wireOp",VERTEX,"E100");
            var Q1;
            Q1=makeQuery(id+"F79.opExtrude","SWEPT_BODY",BODY,{"disambiguationData":[OSD([sQuery(id+"F78.wireOp",EDGE,"E99.bottom"),sQuery(id+"F78.wireOp",EDGE,"E99.right"),sQuery(id+"F78.wireOp",EDGE,"E102"),sQuery(id+"F78.wireOp",EDGE,"E103")])]});
            hole(context, id + "F129", {"style" : HoleStyle.SIMPLE, "endStyle" : HoleEndStyle.THROUGH, "oppositeDirection" : true, "holeDiameter" : 6.35 * mm, "majorDiameter" : 6.35 * mm, "isTappedThrough" : true, "tappedDepth" : 12.7 * mm, "tapClearance" : 3, "locations" : qUnion([Q0]), "scope" : qUnion([Q1])});
        }
        {
            var Q0;
            Q0=sQuery(id+"F78.wireOp",VERTEX,"E101");
            var Q1;
            Q1=makeQuery(id+"F79.opExtrude","SWEPT_BODY",BODY,{"disambiguationData":[OSD([sQuery(id+"F78.wireOp",EDGE,"E99.bottom"),sQuery(id+"F78.wireOp",EDGE,"E99.right"),sQuery(id+"F78.wireOp",EDGE,"E102"),sQuery(id+"F78.wireOp",EDGE,"E103")])]});
            hole(context, id + "F130", {"style" : HoleStyle.SIMPLE, "endStyle" : HoleEndStyle.THROUGH, "oppositeDirection" : true, "holeDiameter" : 6.35 * mm, "majorDiameter" : 6.35 * mm, "isTappedThrough" : true, "tappedDepth" : 12.7 * mm, "tapClearance" : 3, "locations" : qUnion([Q0]), "scope" : qUnion([Q1])});
        }
        {
            var Q0;
            Q0=makeQuery(id+"F128.boolean.opBoolean","MERGE",FACE,{"derivedFrom":[makeQuery(id+"F79.opExtrude","SWEPT_FACE",FACE,{"disambiguationData":[OSD([sQuery(id+"F78.wireOp",EDGE,"E102")])]}),makeQuery(id+"F128.opExtrude","SWEPT_FACE",FACE,{"disambiguationData":[OSD([sQuery(id+"F78.wireOp",EDGE,"E99.left")])]})]});
            var sketch = newSketch(context, id + "F131", { "sketchPlane" : qUnion([Q0])});
            skLineSegment(sketch, "E192.0.0", {"start": v(0, 200.63) * mm, "end": v(0, 111.73) * mm});
            skLineSegment(sketch, "E192.0.1", {"start": v(0, 111.73) * mm, "end": v(19.05, 111.73) * mm});
            skLineSegment(sketch, "E192.0.2", {"start": v(19.05, 111.73) * mm, "end": v(19.05, 194.28) * mm});
            skLineSegment(sketch, "E192.0.3", {"start": v(19.05, 194.28) * mm, "end": v(12.7, 194.28) * mm});
            skLineSegment(sketch, "E192.0.4", {"start": v(12.7, 194.28) * mm, "end": v(12.7, 200.63) * mm});
            skLineSegment(sketch, "E192.0.5", {"start": v(12.7, 200.63) * mm, "end": v(0, 200.63) * mm});
            skPoint(sketch, "E193", {"position": v(9.52, 140.3) * mm});
            skPoint(sketch, "E193.positionSnap0", {"position": v(9.53, 111.73) * mm});
            skPoint(sketch, "E194", {"position": v(9.52, 172.06) * mm});
            skSolve(sketch);
        }
        {
            var Q0;
            Q0=sQuery(id+"F131.wireOp",VERTEX,"E194");
            var Q1;
            Q1=sQuery(id+"F131.wireOp",VERTEX,"E193");
            var Q2;
            Q2=makeQuery(id+"F79.opExtrude","SWEPT_BODY",BODY,{"disambiguationData":[OSD([sQuery(id+"F78.wireOp",EDGE,"E99.bottom"),sQuery(id+"F78.wireOp",EDGE,"E99.right"),sQuery(id+"F78.wireOp",EDGE,"E102"),sQuery(id+"F78.wireOp",EDGE,"E103")])]});
            hole(context, id + "F132", {"style" : HoleStyle.SIMPLE, "endStyle" : HoleEndStyle.BLIND, "holeDiameter" : 6.35 * mm, "majorDiameter" : 6.35 * mm, "holeDepth" : 25.4 * mm, "isTappedThrough" : true, "tappedDepth" : 12.7 * mm, "tapClearance" : 3, "locations" : qUnion([Q0, Q1]), "scope" : qUnion([Q2])});
        }
        {
            var Q0;
            {var subQ0=sQuery(id+"F78.wireOp",EDGE,"E99.right");Q0=makeQuery(id+"F128.boolean.opBoolean","MERGE",FACE,{"derivedFrom":[makeQuery(id+"F79.opExtrude","SWEPT_FACE",FACE,{"disambiguationData":[OSD([subQ0])]}),makeQuery(id+"F128.opExtrude","SWEPT_FACE",FACE,{"disambiguationData":[OSD([subQ0])]})]});}
            var sketch = newSketch(context, id + "F133", { "sketchPlane" : qUnion([Q0])});
            skLineSegment(sketch, "E195.0.0", {"start": v(0, 111.73) * mm, "end": v(0, 200.63) * mm});
            skLineSegment(sketch, "E195.0.1", {"start": v(0, 200.63) * mm, "end": v(-12.7, 200.63) * mm});
            skLineSegment(sketch, "E195.0.2", {"start": v(-12.7, 200.63) * mm, "end": v(-12.7, 194.28) * mm});
            skLineSegment(sketch, "E195.0.3", {"start": v(-12.7, 194.28) * mm, "end": v(-19.05, 194.28) * mm});
            skLineSegment(sketch, "E195.0.4", {"start": v(-19.05, 194.28) * mm, "end": v(-19.05, 111.73) * mm});
            skLineSegment(sketch, "E195.0.5", {"start": v(-19.05, 111.73) * mm, "end": v(0, 111.73) * mm});
            skPoint(sketch, "E196", {"position": v(-9.53, 140.3) * mm});
            skPoint(sketch, "E196.positionSnap0", {"position": v(-9.53, 111.73) * mm});
            skPoint(sketch, "E197", {"position": v(-9.53, 172.06) * mm});
            skSolve(sketch);
        }
        {
            var Q0;
            Q0=sQuery(id+"F133.wireOp",VERTEX,"E197");
            var Q1;
            Q1=sQuery(id+"F133.wireOp",VERTEX,"E196");
            var Q2;
            Q2=makeQuery(id+"F79.opExtrude","SWEPT_BODY",BODY,{"disambiguationData":[OSD([sQuery(id+"F78.wireOp",EDGE,"E99.bottom"),sQuery(id+"F78.wireOp",EDGE,"E99.right"),sQuery(id+"F78.wireOp",EDGE,"E102"),sQuery(id+"F78.wireOp",EDGE,"E103")])]});
            hole(context, id + "F134", {"style" : HoleStyle.SIMPLE, "endStyle" : HoleEndStyle.BLIND, "holeDiameter" : 6.35 * mm, "majorDiameter" : 6.35 * mm, "holeDepth" : 25.4 * mm, "isTappedThrough" : true, "tappedDepth" : 12.7 * mm, "tapClearance" : 3, "locations" : qUnion([Q0, Q1]), "scope" : qUnion([Q2])});
        }
        {
            var Q0;
            Q0=makeQuery(id+"F81.opExtrude","CAP_FACE",FACE,{"disambiguationData":[OSD([sQuery(id+"F80.wireOp",EDGE,"E104.bottom"),sQuery(id+"F80.wireOp",EDGE,"E104.left"),sQuery(id+"F80.wireOp",EDGE,"E104.right"),sQuery(id+"F80.wireOp",EDGE,"E106")])],"isStart":false});
            var sketch = newSketch(context, id + "F135", { "sketchPlane" : qUnion([Q0])});
            skLineSegment(sketch, "E198.bottom", {"start": v(125.02, 437.87) * mm, "end": v(620.32, 437.87) * mm});
            skLineSegment(sketch, "E198.top", {"start": v(125.02, 348.97) * mm, "end": v(620.32, 348.97) * mm});
            skLineSegment(sketch, "E198.left", {"start": v(125.02, 437.87) * mm, "end": v(125.02, 348.97) * mm});
            skLineSegment(sketch, "E198.right", {"start": v(620.32, 437.87) * mm, "end": v(620.32, 348.97) * mm});
            skSolve(sketch);
        }
        {
            var Q0;
            Q0=makeQuery(id+"F135.imprint","IMPRINT",FACE,{"disambiguationData":[TD([[makeQuery(id+"F135.imprint","IMPRINT",EDGE,{"derivedFrom":sQuery(id+"F135.wireOp",EDGE,"E198.bottom")}),-1.0]])]});
            extrude(context, id + "F136", {"entities" : qUnion([Q0]), "depth" : 19.05 * mm, "offsetDistance" : 25.4 * mm});
        }
        {
            var Q0;
            Q0=makeQuery(id+"F136.opExtrude","SWEPT_FACE",FACE,{"disambiguationData":[OSD([sQuery(id+"F135.wireOp",EDGE,"E198.left")])]});
            var sketch = newSketch(context, id + "F137", { "sketchPlane" : qUnion([Q0])});
            skLineSegment(sketch, "E199.0.0", {"start": v(19.05, 437.87) * mm, "end": v(19.05, 348.97) * mm});
            skLineSegment(sketch, "E199.0.1", {"start": v(19.05, 348.97) * mm, "end": v(38.1, 348.97) * mm});
            skLineSegment(sketch, "E199.0.2", {"start": v(38.1, 348.97) * mm, "end": v(38.1, 437.87) * mm});
            skLineSegment(sketch, "E199.0.3", {"start": v(38.1, 437.87) * mm, "end": v(19.05, 437.87) * mm});
            skPoint(sketch, "E200", {"position": v(28.57, 377.55) * mm});
            skPoint(sketch, "E200.positionSnap0", {"position": v(28.58, 348.97) * mm});
            skPoint(sketch, "E201", {"position": v(28.57, 409.3) * mm});
            skSolve(sketch);
        }
        {
            var Q0;
            Q0=sQuery(id+"F137.wireOp",VERTEX,"E201");
            var Q1;
            Q1=sQuery(id+"F137.wireOp",VERTEX,"E200");
            var Q2;
            Q2=makeQuery(id+"F136.opExtrude","SWEPT_BODY",BODY,{"disambiguationData":[OSD([sQuery(id+"F135.wireOp",EDGE,"E198.bottom"),sQuery(id+"F135.wireOp",EDGE,"E198.top"),sQuery(id+"F135.wireOp",EDGE,"E198.left"),sQuery(id+"F135.wireOp",EDGE,"E198.right")])]});
            hole(context, id + "F138", {"style" : HoleStyle.SIMPLE, "endStyle" : HoleEndStyle.BLIND, "holeDiameter" : 6.35 * mm, "majorDiameter" : 6.35 * mm, "holeDepth" : 25.4 * mm, "isTappedThrough" : true, "tappedDepth" : 12.7 * mm, "tapClearance" : 3, "locations" : qUnion([Q0, Q1]), "scope" : qUnion([Q2])});
        }
        {
            var Q0;
            Q0=makeQuery(id+"F136.opExtrude","SWEPT_FACE",FACE,{"disambiguationData":[OSD([sQuery(id+"F135.wireOp",EDGE,"E198.right")])]});
            var sketch = newSketch(context, id + "F139", { "sketchPlane" : qUnion([Q0])});
            skLineSegment(sketch, "E202.0.0", {"start": v(-19.05, 348.97) * mm, "end": v(-19.05, 437.87) * mm});
            skLineSegment(sketch, "E202.0.1", {"start": v(-19.05, 437.87) * mm, "end": v(-38.1, 437.87) * mm});
            skLineSegment(sketch, "E202.0.2", {"start": v(-38.1, 437.87) * mm, "end": v(-38.1, 348.97) * mm});
            skLineSegment(sketch, "E202.0.3", {"start": v(-38.1, 348.97) * mm, "end": v(-19.05, 348.97) * mm});
            skPoint(sketch, "E203", {"position": v(-28.58, 348.97) * mm});
            skPoint(sketch, "E204", {"position": v(-28.58, 377.55) * mm});
            skPoint(sketch, "E205", {"position": v(-28.58, 409.3) * mm});
            skSolve(sketch);
        }
        {
            var Q0;
            Q0=sQuery(id+"F139.wireOp",VERTEX,"E205");
            var Q1;
            Q1=sQuery(id+"F139.wireOp",VERTEX,"E204");
            var Q2;
            Q2=makeQuery(id+"F136.opExtrude","SWEPT_BODY",BODY,{"disambiguationData":[OSD([sQuery(id+"F135.wireOp",EDGE,"E198.bottom"),sQuery(id+"F135.wireOp",EDGE,"E198.top"),sQuery(id+"F135.wireOp",EDGE,"E198.left"),sQuery(id+"F135.wireOp",EDGE,"E198.right")])]});
            hole(context, id + "F140", {"style" : HoleStyle.SIMPLE, "endStyle" : HoleEndStyle.BLIND, "holeDiameter" : 6.35 * mm, "majorDiameter" : 6.35 * mm, "holeDepth" : 25.4 * mm, "isTappedThrough" : true, "tappedDepth" : 12.7 * mm, "tapClearance" : 3, "locations" : qUnion([Q0, Q1]), "scope" : qUnion([Q2])});
        }
        {
            var Q0;
            Q0=makeQuery(id+"F136.opExtrude","CAP_FACE",FACE,{"disambiguationData":[OSD([sQuery(id+"F135.wireOp",EDGE,"E198.bottom"),sQuery(id+"F135.wireOp",EDGE,"E198.top"),sQuery(id+"F135.wireOp",EDGE,"E198.left"),sQuery(id+"F135.wireOp",EDGE,"E198.right")])],"isStart":false});
            var sketch = newSketch(context, id + "F141", { "sketchPlane" : qUnion([Q0])});
            skLineSegment(sketch, "E206.bottom", {"start": v(124.1, 547.1) * mm, "end": v(619.4, 547.1) * mm});
            skLineSegment(sketch, "E206.top", {"start": v(124.1, 458.2) * mm, "end": v(619.4, 458.2) * mm});
            skLineSegment(sketch, "E206.left", {"start": v(124.1, 547.1) * mm, "end": v(124.1, 458.2) * mm});
            skLineSegment(sketch, "E206.right", {"start": v(619.4, 547.1) * mm, "end": v(619.4, 458.2) * mm});
            skPoint(sketch, "E207", {"position": v(371.76, 534.4) * mm});
            skPoint(sketch, "E207.positionSnap0", {"position": v(371.76, 547.1) * mm});
            skPoint(sketch, "E208", {"position": v(371.76, 518.53) * mm});
            skSolve(sketch);
        }
        {
            var Q0;
            Q0=makeQuery(id+"F141.imprint","IMPRINT",FACE,{"disambiguationData":[TD([[makeQuery(id+"F141.imprint","IMPRINT",EDGE,{"derivedFrom":sQuery(id+"F141.wireOp",EDGE,"E206.bottom")}),-1.0]])]});
            extrude(context, id + "F142", {"entities" : qUnion([Q0]), "depth" : 19.05 * mm, "offsetDistance" : 25.4 * mm});
        }
        {
            var Q0;
            Q0=sQuery(id+"F141.wireOp",VERTEX,"E207");
            var Q1;
            Q1=makeQuery(id+"F142.opExtrude","SWEPT_BODY",BODY,{"disambiguationData":[OSD([sQuery(id+"F141.wireOp",EDGE,"E206.bottom"),sQuery(id+"F141.wireOp",EDGE,"E206.top"),sQuery(id+"F141.wireOp",EDGE,"E206.left"),sQuery(id+"F141.wireOp",EDGE,"E206.right")])]});
            hole(context, id + "F143", {"style" : HoleStyle.SIMPLE, "endStyle" : HoleEndStyle.THROUGH, "oppositeDirection" : true, "holeDiameter" : 6.35 * mm, "majorDiameter" : 6.35 * mm, "isTappedThrough" : true, "tappedDepth" : 12.7 * mm, "tapClearance" : 3, "locations" : qUnion([Q0]), "scope" : qUnion([Q1])});
        }
        {
            var Q0;
            Q0=sQuery(id+"F141.wireOp",VERTEX,"E208");
            var Q1;
            Q1=makeQuery(id+"F142.opExtrude","SWEPT_BODY",BODY,{"disambiguationData":[OSD([sQuery(id+"F141.wireOp",EDGE,"E206.bottom"),sQuery(id+"F141.wireOp",EDGE,"E206.top"),sQuery(id+"F141.wireOp",EDGE,"E206.left"),sQuery(id+"F141.wireOp",EDGE,"E206.right")])]});
            hole(context, id + "F144", {"style" : HoleStyle.SIMPLE, "endStyle" : HoleEndStyle.THROUGH, "oppositeDirection" : true, "holeDiameter" : 6.35 * mm, "majorDiameter" : 6.35 * mm, "isTappedThrough" : true, "tappedDepth" : 12.7 * mm, "tapClearance" : 3, "locations" : qUnion([Q0]), "scope" : qUnion([Q1])});
        }
        {
            var Q0;
            Q0=sQuery(id+"F85.wireOp",VERTEX,"E112");
            var Q1;
            Q1=makeQuery(id+"F81.opExtrude","SWEPT_BODY",BODY,{"disambiguationData":[OSD([sQuery(id+"F80.wireOp",EDGE,"E104.bottom"),sQuery(id+"F80.wireOp",EDGE,"E104.left"),sQuery(id+"F80.wireOp",EDGE,"E104.right"),sQuery(id+"F80.wireOp",EDGE,"E106")])]});
            hole(context, id + "F145", {"style" : HoleStyle.SIMPLE, "endStyle" : HoleEndStyle.BLIND, "holeDiameter" : 6.35 * mm, "majorDiameter" : 6.35 * mm, "holeDepth" : 25.4 * mm, "isTappedThrough" : true, "tappedDepth" : 12.7 * mm, "tapClearance" : 3, "locations" : qUnion([Q0]), "scope" : qUnion([Q1])});
        }
        {
            var Q0;
            Q0=makeQuery(id+"F142.opExtrude","SWEPT_FACE",FACE,{"disambiguationData":[OSD([sQuery(id+"F141.wireOp",EDGE,"E206.right")])]});
            var sketch = newSketch(context, id + "F146", { "sketchPlane" : qUnion([Q0])});
            skLineSegment(sketch, "E209.0.0", {"start": v(-38.1, 458.2) * mm, "end": v(-38.1, 547.1) * mm});
            skLineSegment(sketch, "E209.0.1", {"start": v(-38.1, 547.1) * mm, "end": v(-57.15, 547.1) * mm});
            skLineSegment(sketch, "E209.0.2", {"start": v(-57.15, 547.1) * mm, "end": v(-57.15, 458.2) * mm});
            skLineSegment(sketch, "E209.0.3", {"start": v(-57.15, 458.2) * mm, "end": v(-38.1, 458.2) * mm});
            skPoint(sketch, "E210", {"position": v(-47.62, 518.53) * mm});
            skPoint(sketch, "E210.positionSnap0", {"position": v(-47.63, 547.1) * mm});
            skPoint(sketch, "E211", {"position": v(-47.62, 486.78) * mm});
            skSolve(sketch);
        }
        {
            var Q0;
            Q0=sQuery(id+"F146.wireOp",VERTEX,"E210");
            var Q1;
            Q1=sQuery(id+"F146.wireOp",VERTEX,"E211");
            var Q2;
            Q2=makeQuery(id+"F142.opExtrude","SWEPT_BODY",BODY,{"disambiguationData":[OSD([sQuery(id+"F141.wireOp",EDGE,"E206.bottom"),sQuery(id+"F141.wireOp",EDGE,"E206.top"),sQuery(id+"F141.wireOp",EDGE,"E206.left"),sQuery(id+"F141.wireOp",EDGE,"E206.right")])]});
            hole(context, id + "F147", {"style" : HoleStyle.SIMPLE, "endStyle" : HoleEndStyle.BLIND, "holeDiameter" : 6.35 * mm, "majorDiameter" : 6.35 * mm, "holeDepth" : 25.4 * mm, "isTappedThrough" : true, "tappedDepth" : 12.7 * mm, "tapClearance" : 3, "locations" : qUnion([Q0, Q1]), "scope" : qUnion([Q2])});
        }
        {
            var Q0;
            Q0=makeQuery(id+"F142.opExtrude","SWEPT_FACE",FACE,{"disambiguationData":[OSD([sQuery(id+"F141.wireOp",EDGE,"E206.left")])]});
            var sketch = newSketch(context, id + "F148", { "sketchPlane" : qUnion([Q0])});
            skLineSegment(sketch, "E212.0.0", {"start": v(38.1, 547.1) * mm, "end": v(38.1, 458.2) * mm});
            skLineSegment(sketch, "E212.0.1", {"start": v(38.1, 458.2) * mm, "end": v(57.15, 458.2) * mm});
            skLineSegment(sketch, "E212.0.2", {"start": v(57.15, 458.2) * mm, "end": v(57.15, 547.1) * mm});
            skLineSegment(sketch, "E212.0.3", {"start": v(57.15, 547.1) * mm, "end": v(38.1, 547.1) * mm});
            skPoint(sketch, "E213", {"position": v(47.63, 486.78) * mm});
            skPoint(sketch, "E213.positionSnap0", {"position": v(47.63, 458.2) * mm});
            skPoint(sketch, "E214", {"position": v(47.62, 518.53) * mm});
            skSolve(sketch);
        }
        {
            var Q0;
            Q0=sQuery(id+"F148.wireOp",VERTEX,"E214");
            var Q1;
            Q1=sQuery(id+"F148.wireOp",VERTEX,"E213");
            var Q2;
            Q2=makeQuery(id+"F142.opExtrude","SWEPT_BODY",BODY,{"disambiguationData":[OSD([sQuery(id+"F141.wireOp",EDGE,"E206.bottom"),sQuery(id+"F141.wireOp",EDGE,"E206.top"),sQuery(id+"F141.wireOp",EDGE,"E206.left"),sQuery(id+"F141.wireOp",EDGE,"E206.right")])]});
            hole(context, id + "F149", {"style" : HoleStyle.SIMPLE, "endStyle" : HoleEndStyle.BLIND, "holeDiameter" : 6.35 * mm, "majorDiameter" : 6.35 * mm, "holeDepth" : 25.4 * mm, "isTappedThrough" : true, "tappedDepth" : 12.7 * mm, "tapClearance" : 3, "locations" : qUnion([Q0, Q1]), "scope" : qUnion([Q2])});
        }
        {
            var Q0;
            Q0=qCreatedBy(makeId("Front.planeOp"),FACE);
            var sketch = newSketch(context, id + "F150", { "sketchPlane" : qUnion([Q0])});
            skLineSegment(sketch, "E215.bottom", {"start": v(993.7, 327.14) * mm, "end": v(1095.3, 327.14) * mm});
            skLineSegment(sketch, "E215.top", {"start": v(993.7, 250.94) * mm, "end": v(1095.3, 250.94) * mm});
            skLineSegment(sketch, "E215.left", {"start": v(993.7, 327.14) * mm, "end": v(993.7, 250.94) * mm});
            skLineSegment(sketch, "E215.right", {"start": v(1095.3, 327.14) * mm, "end": v(1095.3, 250.94) * mm});
            skLineSegment(sketch, "E216", {"start": v(993.7, 327.14) * mm, "end": v(993.7, 333.5) * mm});
            skLineSegment(sketch, "E217", {"start": v(993.7, 333.5) * mm, "end": v(1095.3, 333.5) * mm});
            skLineSegment(sketch, "E218", {"start": v(1095.3, 327.14) * mm, "end": v(1095.3, 333.5) * mm});
            skLineSegment(sketch, "E219", {"start": v(993.7, 250.94) * mm, "end": v(993.7, 244.6) * mm});
            skLineSegment(sketch, "E220", {"start": v(993.7, 244.6) * mm, "end": v(1095.3, 244.6) * mm});
            skLineSegment(sketch, "E221", {"start": v(1095.3, 244.6) * mm, "end": v(1095.3, 250.94) * mm});
            skSolve(sketch);
        }
        {
            var Q0;
            Q0=makeQuery(id+"F150.imprint","IMPRINT",FACE,{"disambiguationData":[TD([[makeQuery(id+"F150.imprint","IMPRINT",EDGE,{"derivedFrom":sQuery(id+"F150.wireOp",EDGE,"E215.bottom")}),-1.0]])]});
            extrude(context, id + "F151", {"entities" : qUnion([Q0]), "depth" : 19.05 * mm, "offsetDistance" : 25.4 * mm});
        }
        {
            var Q0;
            Q0=makeQuery(id+"F150.imprint","IMPRINT",FACE,{"disambiguationData":[TD([[makeQuery(id+"F150.imprint","IMPRINT",EDGE,{"derivedFrom":sQuery(id+"F150.wireOp",EDGE,"E215.bottom")}),1.0]])]});
            extrude(context, id + "F152", {"entities" : qUnion([Q0]), "operationType" : NewBodyOperationType.ADD, "depth" : 12.7 * mm, "offsetDistance" : 25.4 * mm});
        }
        {
            var Q0;
            Q0=makeQuery(id+"F150.imprint","IMPRINT",FACE,{"disambiguationData":[TD([[makeQuery(id+"F150.imprint","IMPRINT",EDGE,{"derivedFrom":sQuery(id+"F150.wireOp",EDGE,"E215.top")}),-1.0]])]});
            extrude(context, id + "F153", {"entities" : qUnion([Q0]), "operationType" : NewBodyOperationType.ADD, "depth" : 12.7 * mm, "offsetDistance" : 25.4 * mm});
        }
        {
            var Q0;
            Q0=makeQuery(id+"F153.boolean.opBoolean","MERGE",FACE,{"derivedFrom":[makeQuery(id+"F152.boolean.opBoolean","MERGE",FACE,{"derivedFrom":[makeQuery(id+"F151.opExtrude","SWEPT_FACE",FACE,{"disambiguationData":[OSD([sQuery(id+"F150.wireOp",EDGE,"E215.right")])]}),makeQuery(id+"F152.opExtrude","SWEPT_FACE",FACE,{"disambiguationData":[OSD([sQuery(id+"F150.wireOp",EDGE,"E218")])]})]}),makeQuery(id+"F153.opExtrude","SWEPT_FACE",FACE,{"disambiguationData":[OSD([sQuery(id+"F150.wireOp",EDGE,"E221")])]})]});
            var sketch = newSketch(context, id + "F154", { "sketchPlane" : qUnion([Q0])});
            skLineSegment(sketch, "E222.0.0", {"start": v(0, 244.6) * mm, "end": v(0, 333.5) * mm});
            skLineSegment(sketch, "E222.0.1", {"start": v(0, 333.5) * mm, "end": v(-12.7, 333.5) * mm});
            skLineSegment(sketch, "E222.0.2", {"start": v(-12.7, 333.5) * mm, "end": v(-12.7, 327.14) * mm});
            skLineSegment(sketch, "E222.0.3", {"start": v(-12.7, 327.14) * mm, "end": v(-19.05, 327.14) * mm});
            skLineSegment(sketch, "E222.0.4", {"start": v(-19.05, 327.14) * mm, "end": v(-19.05, 250.94) * mm});
            skLineSegment(sketch, "E222.0.5", {"start": v(-19.05, 250.94) * mm, "end": v(-12.7, 250.94) * mm});
            skLineSegment(sketch, "E222.0.6", {"start": v(-12.7, 250.94) * mm, "end": v(-12.7, 244.6) * mm});
            skLineSegment(sketch, "E222.0.7", {"start": v(-12.7, 244.6) * mm, "end": v(0, 244.6) * mm});
            skPoint(sketch, "E223", {"position": v(-9.52, 304.92) * mm});
            skPoint(sketch, "E224", {"position": v(-9.53, 273.17) * mm});
            skSolve(sketch);
        }
        {
            var Q0;
            Q0=sQuery(id+"F154.wireOp",VERTEX,"E223");
            var Q1;
            Q1=sQuery(id+"F154.wireOp",VERTEX,"E224");
            var Q2;
            Q2=makeQuery(id+"F151.opExtrude","SWEPT_BODY",BODY,{"disambiguationData":[OSD([sQuery(id+"F150.wireOp",EDGE,"E215.bottom"),sQuery(id+"F150.wireOp",EDGE,"E215.top"),sQuery(id+"F150.wireOp",EDGE,"E215.left"),sQuery(id+"F150.wireOp",EDGE,"E215.right")])]});
            hole(context, id + "F155", {"style" : HoleStyle.SIMPLE, "endStyle" : HoleEndStyle.BLIND, "holeDiameter" : 6.35 * mm, "majorDiameter" : 6.35 * mm, "holeDepth" : 25.4 * mm, "isTappedThrough" : true, "tappedDepth" : 12.7 * mm, "tapClearance" : 3, "locations" : qUnion([Q0, Q1]), "scope" : qUnion([Q2])});
        }
        {
            var Q0;
            Q0=makeQuery(id+"F153.boolean.opBoolean","MERGE",FACE,{"derivedFrom":[makeQuery(id+"F152.boolean.opBoolean","MERGE",FACE,{"derivedFrom":[makeQuery(id+"F151.opExtrude","SWEPT_FACE",FACE,{"disambiguationData":[OSD([sQuery(id+"F150.wireOp",EDGE,"E215.left")])]}),makeQuery(id+"F152.opExtrude","SWEPT_FACE",FACE,{"disambiguationData":[OSD([sQuery(id+"F150.wireOp",EDGE,"E216")])]})]}),makeQuery(id+"F153.opExtrude","SWEPT_FACE",FACE,{"disambiguationData":[OSD([sQuery(id+"F150.wireOp",EDGE,"E219")])]})]});
            var sketch = newSketch(context, id + "F156", { "sketchPlane" : qUnion([Q0])});
            skLineSegment(sketch, "E225.0.0", {"start": v(0, 333.5) * mm, "end": v(0, 244.6) * mm});
            skLineSegment(sketch, "E225.0.1", {"start": v(0, 244.6) * mm, "end": v(12.7, 244.6) * mm});
            skLineSegment(sketch, "E225.0.2", {"start": v(12.7, 244.6) * mm, "end": v(12.7, 250.94) * mm});
            skLineSegment(sketch, "E225.0.3", {"start": v(12.7, 250.94) * mm, "end": v(19.05, 250.94) * mm});
            skLineSegment(sketch, "E225.0.4", {"start": v(19.05, 250.94) * mm, "end": v(19.05, 327.14) * mm});
            skLineSegment(sketch, "E225.0.5", {"start": v(19.05, 327.14) * mm, "end": v(12.7, 327.14) * mm});
            skLineSegment(sketch, "E225.0.6", {"start": v(12.7, 327.14) * mm, "end": v(12.7, 333.5) * mm});
            skLineSegment(sketch, "E225.0.7", {"start": v(12.7, 333.5) * mm, "end": v(0, 333.5) * mm});
            skPoint(sketch, "E226", {"position": v(9.53, 304.92) * mm});
            skPoint(sketch, "E227", {"position": v(9.53, 273.17) * mm});
            skSolve(sketch);
        }
        {
            var Q0;
            Q0=sQuery(id+"F156.wireOp",VERTEX,"E226");
            var Q1;
            Q1=sQuery(id+"F156.wireOp",VERTEX,"E227");
            var Q2;
            Q2=makeQuery(id+"F151.opExtrude","SWEPT_BODY",BODY,{"disambiguationData":[OSD([sQuery(id+"F150.wireOp",EDGE,"E215.bottom"),sQuery(id+"F150.wireOp",EDGE,"E215.top"),sQuery(id+"F150.wireOp",EDGE,"E215.left"),sQuery(id+"F150.wireOp",EDGE,"E215.right")])]});
            hole(context, id + "F157", {"style" : HoleStyle.SIMPLE, "endStyle" : HoleEndStyle.BLIND, "holeDiameter" : 6.35 * mm, "majorDiameter" : 6.35 * mm, "holeDepth" : 25.4 * mm, "isTappedThrough" : true, "tappedDepth" : 12.7 * mm, "tapClearance" : 3, "locations" : qUnion([Q0, Q1]), "scope" : qUnion([Q2])});
        }
        {
            var Q0;
            Q0=makeQuery(id+"F98.opExtrude","SWEPT_FACE",FACE,{"disambiguationData":[OSD([sQuery(id+"F97.wireOp",EDGE,"E146")])]});
            var sketch = newSketch(context, id + "F158", { "sketchPlane" : qUnion([Q0])});
            skLineSegment(sketch, "E228.0.0", {"start": v(-9.53, 21.13) * mm, "end": v(-9.53, -67.77) * mm});
            skLineSegment(sketch, "E228.0.1", {"start": v(-9.52, -67.77) * mm, "end": v(9.53, -67.77) * mm});
            skLineSegment(sketch, "E228.0.2", {"start": v(9.53, -67.77) * mm, "end": v(9.53, 21.13) * mm});
            skLineSegment(sketch, "E228.0.3", {"start": v(9.53, 21.13) * mm, "end": v(-9.52, 21.13) * mm});
            skPoint(sketch, "E229", {"position": v(0, -39.2) * mm});
            skPoint(sketch, "E229.positionSnap0", {"position": v(0, -67.77) * mm});
            skPoint(sketch, "E230", {"position": v(0, -7.45) * mm});
            skSolve(sketch);
        }
        {
            var Q0;
            Q0=sQuery(id+"F158.wireOp",VERTEX,"E230");
            var Q1;
            Q1=sQuery(id+"F158.wireOp",VERTEX,"E229");
            var Q2;
            Q2=makeQuery(id+"F98.opExtrude","SWEPT_BODY",BODY,{"disambiguationData":[OSD([sQuery(id+"F97.wireOp",EDGE,"E142.bottom"),sQuery(id+"F97.wireOp",EDGE,"E142.left"),sQuery(id+"F97.wireOp",EDGE,"E142.right"),sQuery(id+"F97.wireOp",EDGE,"E143"),sQuery(id+"F97.wireOp",EDGE,"E144"),sQuery(id+"F97.wireOp",EDGE,"E145"),sQuery(id+"F97.wireOp",EDGE,"E146"),sQuery(id+"F97.wireOp",EDGE,"E147"),sQuery(id+"F97.wireOp",EDGE,"E148.trimOffspring"),sQuery(id+"F97.wireOp",EDGE,"E149.trimOffspring"),sQuery(id+"F97.wireOp",EDGE,"E150"),sQuery(id+"F97.wireOp",EDGE,"E151"),sQuery(id+"F97.wireOp",EDGE,"E152"),sQuery(id+"F97.wireOp",EDGE,"E153")])]});
            hole(context, id + "F159", {"style" : HoleStyle.SIMPLE, "endStyle" : HoleEndStyle.BLIND, "holeDiameter" : 6.35 * mm, "majorDiameter" : 6.35 * mm, "holeDepth" : 25.4 * mm, "isTappedThrough" : true, "tappedDepth" : 12.7 * mm, "tapClearance" : 3, "locations" : qUnion([Q0, Q1]), "scope" : qUnion([Q2])});
        }
        {
            var Q0;
            Q0=makeQuery(id+"F98.opExtrude","SWEPT_FACE",FACE,{"disambiguationData":[OSD([sQuery(id+"F97.wireOp",EDGE,"E143")])]});
            var sketch = newSketch(context, id + "F160", { "sketchPlane" : qUnion([Q0])});
            skLineSegment(sketch, "E231.0.0", {"start": v(-9.53, -359.87) * mm, "end": v(-9.53, -448.77) * mm});
            skLineSegment(sketch, "E231.0.1", {"start": v(-9.52, -448.77) * mm, "end": v(9.53, -448.77) * mm});
            skLineSegment(sketch, "E231.0.2", {"start": v(9.53, -448.77) * mm, "end": v(9.53, -359.87) * mm});
            skLineSegment(sketch, "E231.0.3", {"start": v(9.53, -359.87) * mm, "end": v(-9.52, -359.87) * mm});
            skPoint(sketch, "E232", {"position": v(0, -420.2) * mm});
            skPoint(sketch, "E233", {"position": v(0, -388.45) * mm});
            skSolve(sketch);
        }
        {
            var Q0;
            Q0=sQuery(id+"F160.wireOp",VERTEX,"E233");
            var Q1;
            Q1=sQuery(id+"F160.wireOp",VERTEX,"E232");
            var Q2;
            Q2=makeQuery(id+"F98.opExtrude","SWEPT_BODY",BODY,{"disambiguationData":[OSD([sQuery(id+"F97.wireOp",EDGE,"E142.bottom"),sQuery(id+"F97.wireOp",EDGE,"E142.left"),sQuery(id+"F97.wireOp",EDGE,"E142.right"),sQuery(id+"F97.wireOp",EDGE,"E143"),sQuery(id+"F97.wireOp",EDGE,"E144"),sQuery(id+"F97.wireOp",EDGE,"E145"),sQuery(id+"F97.wireOp",EDGE,"E146"),sQuery(id+"F97.wireOp",EDGE,"E147"),sQuery(id+"F97.wireOp",EDGE,"E148.trimOffspring"),sQuery(id+"F97.wireOp",EDGE,"E149.trimOffspring"),sQuery(id+"F97.wireOp",EDGE,"E150"),sQuery(id+"F97.wireOp",EDGE,"E151"),sQuery(id+"F97.wireOp",EDGE,"E152"),sQuery(id+"F97.wireOp",EDGE,"E153")])]});
            hole(context, id + "F161", {"style" : HoleStyle.SIMPLE, "endStyle" : HoleEndStyle.BLIND, "holeDiameter" : 6.35 * mm, "majorDiameter" : 6.35 * mm, "holeDepth" : 25.4 * mm, "isTappedThrough" : true, "tappedDepth" : 12.7 * mm, "tapClearance" : 3, "locations" : qUnion([Q0, Q1]), "scope" : qUnion([Q2])});
        }
        {
            var Q0;
            Q0=qCreatedBy(makeId("Front.planeOp"),FACE);
            var sketch = newSketch(context, id + "F162", { "sketchPlane" : qUnion([Q0])});
            skLineSegment(sketch, "E234.bottom", {"start": v(997.14, 204.3) * mm, "end": v(1098.74, 204.3) * mm});
            skLineSegment(sketch, "E234.top", {"start": v(997.14, 121.75) * mm, "end": v(1098.74, 121.75) * mm});
            skLineSegment(sketch, "E234.left", {"start": v(997.14, 204.3) * mm, "end": v(997.14, 121.75) * mm});
            skLineSegment(sketch, "E234.right", {"start": v(1098.74, 204.3) * mm, "end": v(1098.74, 121.75) * mm});
            skLineSegment(sketch, "E235", {"start": v(997.14, 121.75) * mm, "end": v(997.14, 115.4) * mm});
            skLineSegment(sketch, "E236", {"start": v(997.14, 115.4) * mm, "end": v(1098.74, 115.4) * mm});
            skLineSegment(sketch, "E237", {"start": v(1098.74, 115.4) * mm, "end": v(1098.74, 121.75) * mm});
            skSolve(sketch);
        }
        {
            var Q0;
            Q0=makeQuery(id+"F162.imprint","IMPRINT",FACE,{"disambiguationData":[TD([[makeQuery(id+"F162.imprint","IMPRINT",EDGE,{"derivedFrom":sQuery(id+"F162.wireOp",EDGE,"E234.bottom")}),-1.0]])]});
            extrude(context, id + "F163", {"entities" : qUnion([Q0]), "depth" : 19.05 * mm, "offsetDistance" : 25.4 * mm});
        }
        {
            var Q0;
            Q0=makeQuery(id+"F162.imprint","IMPRINT",FACE,{"disambiguationData":[TD([[makeQuery(id+"F162.imprint","IMPRINT",EDGE,{"derivedFrom":sQuery(id+"F162.wireOp",EDGE,"E234.top")}),-1.0]])]});
            extrude(context, id + "F164", {"entities" : qUnion([Q0]), "operationType" : NewBodyOperationType.ADD, "depth" : 12.7 * mm, "offsetDistance" : 25.4 * mm});
        }
        {
            var Q0;
            Q0=makeQuery(id+"F164.boolean.opBoolean","MERGE",FACE,{"derivedFrom":[makeQuery(id+"F163.opExtrude","SWEPT_FACE",FACE,{"disambiguationData":[OSD([sQuery(id+"F162.wireOp",EDGE,"E234.right")])]}),makeQuery(id+"F164.opExtrude","SWEPT_FACE",FACE,{"disambiguationData":[OSD([sQuery(id+"F162.wireOp",EDGE,"E237")])]})]});
            var sketch = newSketch(context, id + "F165", { "sketchPlane" : qUnion([Q0])});
            skLineSegment(sketch, "E238.0.0", {"start": v(0, 115.4) * mm, "end": v(0, 204.3) * mm});
            skLineSegment(sketch, "E238.0.1", {"start": v(0, 204.3) * mm, "end": v(-19.05, 204.3) * mm});
            skLineSegment(sketch, "E238.0.2", {"start": v(-19.05, 204.3) * mm, "end": v(-19.05, 121.75) * mm});
            skLineSegment(sketch, "E238.0.3", {"start": v(-19.05, 121.75) * mm, "end": v(-12.7, 121.75) * mm});
            skLineSegment(sketch, "E238.0.4", {"start": v(-12.7, 121.75) * mm, "end": v(-12.7, 115.4) * mm});
            skLineSegment(sketch, "E238.0.5", {"start": v(-12.7, 115.4) * mm, "end": v(0, 115.4) * mm});
            skPoint(sketch, "E239", {"position": v(-9.53, 175.73) * mm});
            skPoint(sketch, "E239.positionSnap0", {"position": v(-9.53, 204.3) * mm});
            skPoint(sketch, "E240", {"position": v(-9.53, 143.98) * mm});
            skSolve(sketch);
        }
        {
            var Q0;
            Q0=sQuery(id+"F165.wireOp",VERTEX,"E239");
            var Q1;
            Q1=sQuery(id+"F165.wireOp",VERTEX,"E240");
            var Q2;
            Q2=makeQuery(id+"F163.opExtrude","SWEPT_BODY",BODY,{"disambiguationData":[OSD([sQuery(id+"F162.wireOp",EDGE,"E234.bottom"),sQuery(id+"F162.wireOp",EDGE,"E234.top"),sQuery(id+"F162.wireOp",EDGE,"E234.left"),sQuery(id+"F162.wireOp",EDGE,"E234.right")])]});
            hole(context, id + "F166", {"style" : HoleStyle.SIMPLE, "endStyle" : HoleEndStyle.BLIND, "holeDiameter" : 6.35 * mm, "majorDiameter" : 6.35 * mm, "holeDepth" : 25.4 * mm, "isTappedThrough" : true, "tappedDepth" : 12.7 * mm, "tapClearance" : 3, "locations" : qUnion([Q0, Q1]), "scope" : qUnion([Q2])});
        }
        {
            var Q0;
            Q0=makeQuery(id+"F164.boolean.opBoolean","MERGE",FACE,{"derivedFrom":[makeQuery(id+"F163.opExtrude","SWEPT_FACE",FACE,{"disambiguationData":[OSD([sQuery(id+"F162.wireOp",EDGE,"E234.left")])]}),makeQuery(id+"F164.opExtrude","SWEPT_FACE",FACE,{"disambiguationData":[OSD([sQuery(id+"F162.wireOp",EDGE,"E235")])]})]});
            var sketch = newSketch(context, id + "F167", { "sketchPlane" : qUnion([Q0])});
            skLineSegment(sketch, "E241.0.0", {"start": v(0, 204.3) * mm, "end": v(0, 115.4) * mm});
            skLineSegment(sketch, "E241.0.1", {"start": v(0, 115.4) * mm, "end": v(12.7, 115.4) * mm});
            skLineSegment(sketch, "E241.0.2", {"start": v(12.7, 115.4) * mm, "end": v(12.7, 121.75) * mm});
            skLineSegment(sketch, "E241.0.3", {"start": v(12.7, 121.75) * mm, "end": v(19.05, 121.75) * mm});
            skLineSegment(sketch, "E241.0.4", {"start": v(19.05, 121.75) * mm, "end": v(19.05, 204.3) * mm});
            skLineSegment(sketch, "E241.0.5", {"start": v(19.05, 204.3) * mm, "end": v(0, 204.3) * mm});
            skPoint(sketch, "E242", {"position": v(9.53, 175.73) * mm});
            skPoint(sketch, "E242.positionSnap0", {"position": v(9.53, 204.3) * mm});
            skPoint(sketch, "E243", {"position": v(9.53, 143.98) * mm});
            skSolve(sketch);
        }
        {
            var Q0;
            Q0=sQuery(id+"F167.wireOp",VERTEX,"E242");
            var Q1;
            Q1=sQuery(id+"F167.wireOp",VERTEX,"E243");
            var Q2;
            Q2=makeQuery(id+"F163.opExtrude","SWEPT_BODY",BODY,{"disambiguationData":[OSD([sQuery(id+"F162.wireOp",EDGE,"E234.bottom"),sQuery(id+"F162.wireOp",EDGE,"E234.top"),sQuery(id+"F162.wireOp",EDGE,"E234.left"),sQuery(id+"F162.wireOp",EDGE,"E234.right")])]});
            hole(context, id + "F168", {"style" : HoleStyle.SIMPLE, "endStyle" : HoleEndStyle.BLIND, "holeDiameter" : 6.35 * mm, "majorDiameter" : 6.35 * mm, "holeDepth" : 25.4 * mm, "isTappedThrough" : true, "tappedDepth" : 12.7 * mm, "tapClearance" : 3, "locations" : qUnion([Q0, Q1]), "scope" : qUnion([Q2])});
        }
        {
            var Q0;
            Q0=qCreatedBy(makeId("Front.planeOp"),FACE);
            var sketch = newSketch(context, id + "F169", { "sketchPlane" : qUnion([Q0])});
            skLineSegment(sketch, "E244.bottom", {"start": v(957.18, 587.92) * mm, "end": v(1563.6, 587.92) * mm});
            skLineSegment(sketch, "E244.top", {"start": v(957.18, 546.65) * mm, "end": v(1563.6, 546.65) * mm});
            skLineSegment(sketch, "E244.left", {"start": v(957.18, 587.92) * mm, "end": v(957.18, 546.65) * mm});
            skLineSegment(sketch, "E244.right", {"start": v(1563.6, 587.92) * mm, "end": v(1563.6, 546.65) * mm});
            skSolve(sketch);
        }
        {
            var Q0;
            Q0=makeQuery(id+"F169.imprint","IMPRINT",FACE,{"disambiguationData":[TD([[makeQuery(id+"F169.imprint","IMPRINT",EDGE,{"derivedFrom":sQuery(id+"F169.wireOp",EDGE,"E244.bottom")}),-1.0]])]});
            extrude(context, id + "F170", {"entities" : qUnion([Q0]), "depth" : 19.05 * mm, "offsetDistance" : 25.4 * mm});
        }
        {
            var Q0;
            Q0=makeQuery(id+"F170.opExtrude","SWEPT_FACE",FACE,{"disambiguationData":[OSD([sQuery(id+"F169.wireOp",EDGE,"E244.right")])]});
            var sketch = newSketch(context, id + "F171", { "sketchPlane" : qUnion([Q0])});
            skLineSegment(sketch, "E245.0.0", {"start": v(0, 546.65) * mm, "end": v(0, 587.92) * mm});
            skLineSegment(sketch, "E245.0.1", {"start": v(0, 587.92) * mm, "end": v(-19.05, 587.92) * mm});
            skLineSegment(sketch, "E245.0.2", {"start": v(-19.05, 587.92) * mm, "end": v(-19.05, 546.65) * mm});
            skLineSegment(sketch, "E245.0.3", {"start": v(-19.05, 546.65) * mm, "end": v(0, 546.65) * mm});
            skPoint(sketch, "E246", {"position": v(-9.53, 575.22) * mm});
            skPoint(sketch, "E246.positionSnap0", {"position": v(-9.53, 587.92) * mm});
            skPoint(sketch, "E247", {"position": v(-9.53, 559.35) * mm});
            skPoint(sketch, "E247.positionSnap0", {"position": v(-9.53, 546.65) * mm});
            skSolve(sketch);
        }
        {
            var Q0;
            Q0=sQuery(id+"F171.wireOp",VERTEX,"E246");
            var Q1;
            Q1=sQuery(id+"F171.wireOp",VERTEX,"E247");
            var Q2;
            Q2=makeQuery(id+"F170.opExtrude","SWEPT_BODY",BODY,{"disambiguationData":[OSD([sQuery(id+"F169.wireOp",EDGE,"E244.bottom"),sQuery(id+"F169.wireOp",EDGE,"E244.top"),sQuery(id+"F169.wireOp",EDGE,"E244.left"),sQuery(id+"F169.wireOp",EDGE,"E244.right")])]});
            hole(context, id + "F172", {"style" : HoleStyle.SIMPLE, "endStyle" : HoleEndStyle.BLIND, "holeDiameter" : 6.35 * mm, "majorDiameter" : 6.35 * mm, "holeDepth" : 25.4 * mm, "isTappedThrough" : true, "tappedDepth" : 12.7 * mm, "tapClearance" : 3, "locations" : qUnion([Q0, Q1]), "scope" : qUnion([Q2])});
        }
        {
            var Q0;
            Q0=makeQuery(id+"F170.opExtrude","SWEPT_FACE",FACE,{"disambiguationData":[OSD([sQuery(id+"F169.wireOp",EDGE,"E244.left")])]});
            var sketch = newSketch(context, id + "F173", { "sketchPlane" : qUnion([Q0])});
            skLineSegment(sketch, "E248.0.0", {"start": v(0, 587.92) * mm, "end": v(0, 546.65) * mm});
            skLineSegment(sketch, "E248.0.1", {"start": v(0, 546.65) * mm, "end": v(19.05, 546.65) * mm});
            skLineSegment(sketch, "E248.0.2", {"start": v(19.05, 546.65) * mm, "end": v(19.05, 587.92) * mm});
            skLineSegment(sketch, "E248.0.3", {"start": v(19.05, 587.92) * mm, "end": v(0, 587.92) * mm});
            skPoint(sketch, "E249", {"position": v(9.53, 575.22) * mm});
            skPoint(sketch, "E249.positionSnap0", {"position": v(9.53, 587.92) * mm});
            skPoint(sketch, "E250", {"position": v(9.53, 546.65) * mm});
            skPoint(sketch, "E251", {"position": v(9.53, 559.35) * mm});
            skSolve(sketch);
        }
        {
            var Q0;
            Q0=sQuery(id+"F173.wireOp",VERTEX,"E249");
            var Q1;
            Q1=sQuery(id+"F173.wireOp",VERTEX,"E251");
            var Q2;
            Q2=makeQuery(id+"F170.opExtrude","SWEPT_BODY",BODY,{"disambiguationData":[OSD([sQuery(id+"F169.wireOp",EDGE,"E244.bottom"),sQuery(id+"F169.wireOp",EDGE,"E244.top"),sQuery(id+"F169.wireOp",EDGE,"E244.left"),sQuery(id+"F169.wireOp",EDGE,"E244.right")])]});
            hole(context, id + "F174", {"style" : HoleStyle.SIMPLE, "endStyle" : HoleEndStyle.BLIND, "holeDiameter" : 6.35 * mm, "majorDiameter" : 6.35 * mm, "holeDepth" : 25.4 * mm, "isTappedThrough" : true, "tappedDepth" : 12.7 * mm, "tapClearance" : 3, "locations" : qUnion([Q0, Q1]), "scope" : qUnion([Q2])});
        }
        {
            var Q0;
            Q0=makeQuery(id+"F170.opExtrude","CAP_FACE",FACE,{"disambiguationData":[OSD([sQuery(id+"F169.wireOp",EDGE,"E244.bottom"),sQuery(id+"F169.wireOp",EDGE,"E244.top"),sQuery(id+"F169.wireOp",EDGE,"E244.left"),sQuery(id+"F169.wireOp",EDGE,"E244.right")])],"isStart":false});
            var sketch = newSketch(context, id + "F175", { "sketchPlane" : qUnion([Q0])});
            skLineSegment(sketch, "E252.bottom", {"start": v(950.24, 901.97) * mm, "end": v(1556.67, 901.97) * mm});
            skLineSegment(sketch, "E252.top", {"start": v(950.24, 635.27) * mm, "end": v(1556.67, 635.27) * mm});
            skLineSegment(sketch, "E252.left", {"start": v(950.24, 901.97) * mm, "end": v(950.24, 635.27) * mm});
            skLineSegment(sketch, "E252.right", {"start": v(1556.67, 901.97) * mm, "end": v(1556.67, 635.27) * mm});
            skSolve(sketch);
        }
        {
            var Q0;
            Q0=makeQuery(id+"F175.imprint","IMPRINT",FACE,{"disambiguationData":[TD([[makeQuery(id+"F175.imprint","IMPRINT",EDGE,{"derivedFrom":sQuery(id+"F175.wireOp",EDGE,"E252.bottom")}),-1.0]])]});
            extrude(context, id + "F176", {"entities" : qUnion([Q0]), "depth" : 6.35 * mm, "offsetDistance" : 25.4 * mm});
        }
        {
            var Q0;
            Q0=makeQuery(id+"F176.opExtrude","CAP_FACE",FACE,{"disambiguationData":[OSD([sQuery(id+"F175.wireOp",EDGE,"E252.bottom"),sQuery(id+"F175.wireOp",EDGE,"E252.top"),sQuery(id+"F175.wireOp",EDGE,"E252.left"),sQuery(id+"F175.wireOp",EDGE,"E252.right")])],"isStart":false});
            var sketch = newSketch(context, id + "F177", { "sketchPlane" : qUnion([Q0])});
            skLineSegment(sketch, "E253.bottom", {"start": v(1200.99, 472.27) * mm, "end": v(1302.59, 472.27) * mm});
            skLineSegment(sketch, "E253.top", {"start": v(1200.99, 167.47) * mm, "end": v(1302.59, 167.47) * mm});
            skLineSegment(sketch, "E253.left", {"start": v(1200.99, 472.27) * mm, "end": v(1200.99, 167.47) * mm});
            skLineSegment(sketch, "E253.right", {"start": v(1302.59, 472.27) * mm, "end": v(1302.59, 167.47) * mm});
            skSolve(sketch);
        }
        {
            var Q0;
            Q0=makeQuery(id+"F177.imprint","IMPRINT",FACE,{"disambiguationData":[TD([[makeQuery(id+"F177.imprint","IMPRINT",EDGE,{"derivedFrom":sQuery(id+"F177.wireOp",EDGE,"E253.bottom")}),-1.0]])]});
            extrude(context, id + "F178", {"entities" : qUnion([Q0]), "depth" : 6.35 * mm, "offsetDistance" : 25.4 * mm});
        }
        {
            var Q0;
            Q0=makeQuery(id+"F178.opExtrude","CAP_FACE",FACE,{"disambiguationData":[OSD([sQuery(id+"F177.wireOp",EDGE,"E253.bottom"),sQuery(id+"F177.wireOp",EDGE,"E253.top"),sQuery(id+"F177.wireOp",EDGE,"E253.left"),sQuery(id+"F177.wireOp",EDGE,"E253.right")])],"isStart":false});
            var sketch = newSketch(context, id + "F179", { "sketchPlane" : qUnion([Q0])});
            skLineSegment(sketch, "E254.bottom", {"start": v(1401.27, 414.03) * mm, "end": v(1502.87, 414.03) * mm});
            skLineSegment(sketch, "E254.top", {"start": v(1401.27, -157.47) * mm, "end": v(1502.87, -157.47) * mm});
            skLineSegment(sketch, "E254.left", {"start": v(1401.27, 414.03) * mm, "end": v(1401.27, -157.47) * mm});
            skLineSegment(sketch, "E254.right", {"start": v(1502.87, 414.03) * mm, "end": v(1502.87, -157.47) * mm});
            skSolve(sketch);
        }
        {
            var Q0;
            Q0=makeQuery(id+"F179.imprint","IMPRINT",FACE,{"disambiguationData":[TD([[makeQuery(id+"F179.imprint","IMPRINT",EDGE,{"derivedFrom":sQuery(id+"F179.wireOp",EDGE,"E254.bottom")}),-1.0]])]});
            extrude(context, id + "F180", {"entities" : qUnion([Q0]), "depth" : 6.35 * mm, "offsetDistance" : 25.4 * mm});
        }
        {
            var Q0;
            Q0=makeQuery(id+"F90.opExtrude","CAP_FACE",FACE,{"disambiguationData":[OSD([sQuery(id+"F89.wireOp",EDGE,"E113.bottom"),sQuery(id+"F89.wireOp",EDGE,"E113.top"),sQuery(id+"F89.wireOp",EDGE,"E113.left"),sQuery(id+"F89.wireOp",EDGE,"E113.right"),sQuery(id+"F89.wireOp",EDGE,"E114"),sQuery(id+"F89.wireOp",EDGE,"E115"),sQuery(id+"F89.wireOp",EDGE,"E116"),sQuery(id+"F89.wireOp",EDGE,"E117"),sQuery(id+"F89.wireOp",EDGE,"E118"),sQuery(id+"F89.wireOp",EDGE,"E119"),sQuery(id+"F89.wireOp",EDGE,"E120"),sQuery(id+"F89.wireOp",EDGE,"E121.trimOffspring"),sQuery(id+"F89.wireOp",EDGE,"E122.trimOffspring"),sQuery(id+"F89.wireOp",EDGE,"E124"),sQuery(id+"F89.wireOp",EDGE,"E125"),sQuery(id+"F89.wireOp",EDGE,"E126"),sQuery(id+"F89.wireOp",EDGE,"E127.trimOffspring"),sQuery(id+"F89.wireOp",EDGE,"E128.trimOffspring"),sQuery(id+"F89.wireOp",EDGE,"E129"),sQuery(id+"F89.wireOp",EDGE,"E130"),sQuery(id+"F89.wireOp",EDGE,"E131"),sQuery(id+"F89.wireOp",EDGE,"E132"),sQuery(id+"F89.wireOp",EDGE,"E133"),sQuery(id+"F89.wireOp",EDGE,"E134"),sQuery(id+"F89.wireOp",EDGE,"E135"),sQuery(id+"F89.wireOp",EDGE,"E136"),sQuery(id+"F89.wireOp",EDGE,"E137"),sQuery(id+"F89.wireOp",EDGE,"E138")])],"isStart":false});
            var sketch = newSketch(context, id + "F181", { "sketchPlane" : qUnion([Q0])});
            skLineSegment(sketch, "E255.bottom", {"start": v(-2192.61, 1564.22) * mm, "end": v(-4110.31, 1564.22) * mm});
            skLineSegment(sketch, "E255.top", {"start": v(-2192.61, 916.52) * mm, "end": v(-4110.31, 916.52) * mm});
            skLineSegment(sketch, "E255.left", {"start": v(-2192.61, 1564.22) * mm, "end": v(-2192.61, 916.52) * mm});
            skLineSegment(sketch, "E255.right", {"start": v(-4110.31, 1564.22) * mm, "end": v(-4110.31, 916.52) * mm});
            skSolve(sketch);
        }
        {
            var Q0;
            Q0=makeQuery(id+"F181.imprint","IMPRINT",FACE,{"disambiguationData":[TD([[makeQuery(id+"F181.imprint","IMPRINT",EDGE,{"derivedFrom":sQuery(id+"F181.wireOp",EDGE,"E255.bottom")}),1.0]])]});
            extrude(context, id + "F182", {"entities" : qUnion([Q0]), "depth" : 6.35 * mm, "offsetDistance" : 25.4 * mm});
        }
    });
